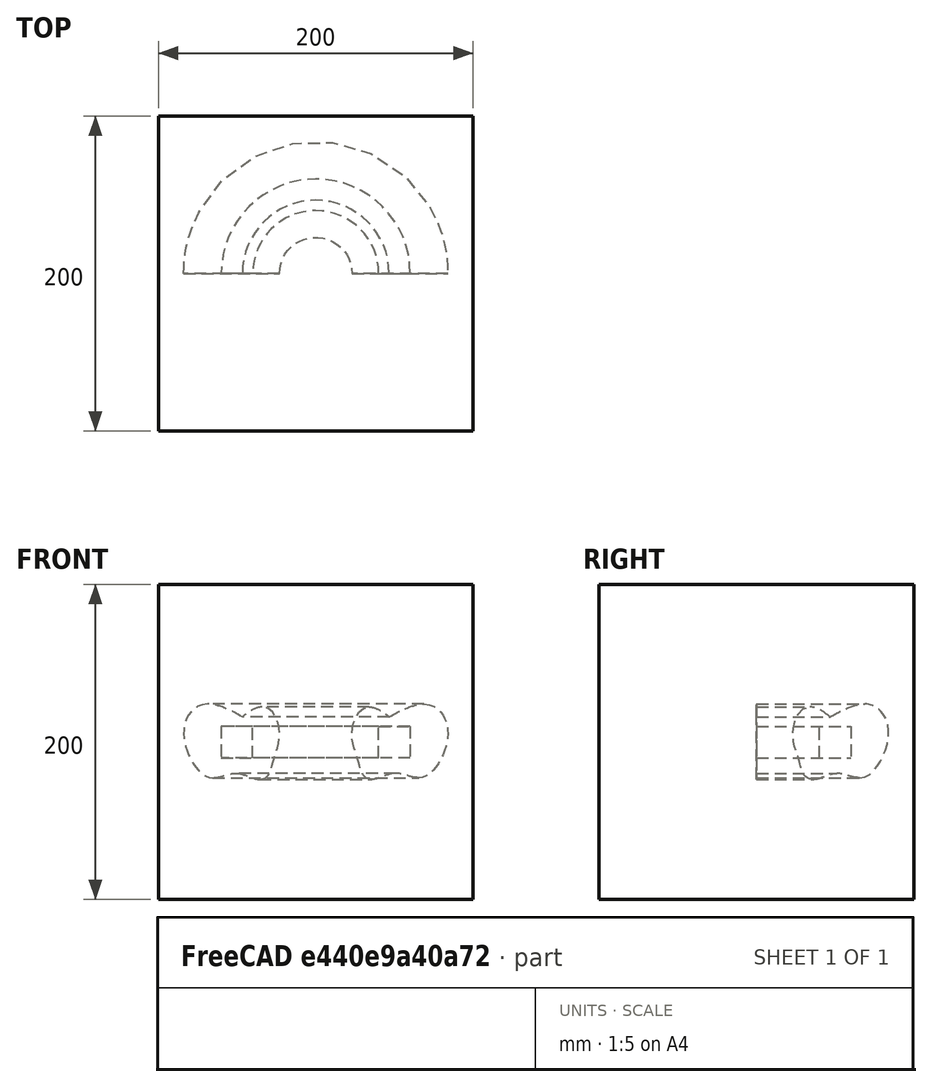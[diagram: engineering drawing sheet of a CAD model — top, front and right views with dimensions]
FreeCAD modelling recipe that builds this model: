
FCSTD DOCUMENT  (FreeCAD 0.19RUnknown)
Label: revolve
License: All rights reserved
LicenseURL: http://en.wikipedia.org/wiki/All_rights_reserved
objects: App::DocumentObjectGroupPython×1248, App::Part×2, Part::FeaturePython×1, Sketcher::SketchObject×1, Part::Revolution×1
note: 3 computed .brp shape members not serialized (recipe doc carries the construction recipe); baked Part::Feature solids carry a one-line shape summary decoded from their .brp

FEATURE [App::DocumentObjectGroupPython] HALFPI  # scripted group (container) (typed FeaturePython)
  name = HALFPI
  value = pi/2.
FEATURE [App::DocumentObjectGroupPython] PI  # scripted group (container) (typed FeaturePython)
  name = PI
  value = 1.*pi
FEATURE [App::DocumentObjectGroupPython] TWOPI  # scripted group (container) (typed FeaturePython)
  name = TWOPI
  value = 2.*pi
FEATURE [App::DocumentObjectGroupPython] Constants  # scripted group (container) (typed FeaturePython)
  Group = -> [HALFPI,PI,TWOPI]
FEATURE [App::DocumentObjectGroupPython] Variables  # scripted group (container) (typed FeaturePython)
FEATURE [App::DocumentObjectGroupPython] Quantities  # scripted group (container) (typed FeaturePython)
FEATURE [App::DocumentObjectGroupPython] Isotopes  # scripted group (container) (typed FeaturePython)
FEATURE [App::DocumentObjectGroupPython] Elements  # scripted group (container) (typed FeaturePython)
FEATURE [App::DocumentObjectGroupPython] G4Isotopes  # scripted group (container) (typed FeaturePython)
FEATURE [App::DocumentObjectGroupPython] H_element  # scripted group (container) (typed FeaturePython)
  Z = 1
  atom_value = 1.008
  formula = H
  name = H_element
FEATURE [App::DocumentObjectGroupPython] He_element  # scripted group (container) (typed FeaturePython)
  Z = 2
  atom_value = 4.0026
  formula = He
  name = He_element
FEATURE [App::DocumentObjectGroupPython] Li_element  # scripted group (container) (typed FeaturePython)
  Z = 3
  atom_value = 6.94
  formula = Li
  name = Li_element
FEATURE [App::DocumentObjectGroupPython] Be_element  # scripted group (container) (typed FeaturePython)
  Z = 4
  atom_value = 9.01218
  formula = Be
  name = Be_element
FEATURE [App::DocumentObjectGroupPython] B_element  # scripted group (container) (typed FeaturePython)
  Z = 5
  atom_value = 10.81
  formula = B
  name = B_element
FEATURE [App::DocumentObjectGroupPython] C_element  # scripted group (container) (typed FeaturePython)
  Z = 6
  atom_value = 12.011
  formula = C
  name = C_element
FEATURE [App::DocumentObjectGroupPython] N_element  # scripted group (container) (typed FeaturePython)
  Z = 7
  atom_value = 14.007
  formula = N
  name = N_element
FEATURE [App::DocumentObjectGroupPython] O_element  # scripted group (container) (typed FeaturePython)
  Z = 8
  atom_value = 15.999
  formula = O
  name = O_element
FEATURE [App::DocumentObjectGroupPython] F_element  # scripted group (container) (typed FeaturePython)
  Z = 9
  atom_value = 18.9984
  formula = F
  name = F_element
FEATURE [App::DocumentObjectGroupPython] Ne_element  # scripted group (container) (typed FeaturePython)
  Z = 10
  atom_value = 20.1797
  formula = Ne
  name = Ne_element
FEATURE [App::DocumentObjectGroupPython] Na_element  # scripted group (container) (typed FeaturePython)
  Z = 11
  atom_value = 22.9898
  formula = Na
  name = Na_element
FEATURE [App::DocumentObjectGroupPython] Mg_element  # scripted group (container) (typed FeaturePython)
  Z = 12
  atom_value = 24.305
  formula = Mg
  name = Mg_element
FEATURE [App::DocumentObjectGroupPython] Al_element  # scripted group (container) (typed FeaturePython)
  Z = 13
  atom_value = 26.9815
  formula = Al
  name = Al_element
FEATURE [App::DocumentObjectGroupPython] Si_element  # scripted group (container) (typed FeaturePython)
  Z = 14
  atom_value = 28.085
  formula = Si
  name = Si_element
FEATURE [App::DocumentObjectGroupPython] P_element  # scripted group (container) (typed FeaturePython)
  Z = 15
  atom_value = 30.9738
  formula = P
  name = P_element
FEATURE [App::DocumentObjectGroupPython] S_element  # scripted group (container) (typed FeaturePython)
  Z = 16
  atom_value = 32.06
  formula = S
  name = S_element
FEATURE [App::DocumentObjectGroupPython] Cl_element  # scripted group (container) (typed FeaturePython)
  Z = 17
  atom_value = 35.45
  formula = Cl
  name = Cl_element
FEATURE [App::DocumentObjectGroupPython] Ar_element  # scripted group (container) (typed FeaturePython)
  Z = 18
  atom_value = 39.95
  formula = Ar
  name = Ar_element
FEATURE [App::DocumentObjectGroupPython] K_element  # scripted group (container) (typed FeaturePython)
  Z = 19
  atom_value = 39.0983
  formula = K
  name = K_element
FEATURE [App::DocumentObjectGroupPython] Ca_element  # scripted group (container) (typed FeaturePython)
  Z = 20
  atom_value = 40.078
  formula = Ca
  name = Ca_element
FEATURE [App::DocumentObjectGroupPython] Sc_element  # scripted group (container) (typed FeaturePython)
  Z = 21
  atom_value = 44.9559
  formula = Sc
  name = Sc_element
FEATURE [App::DocumentObjectGroupPython] Ti_element  # scripted group (container) (typed FeaturePython)
  Z = 22
  atom_value = 47.867
  formula = Ti
  name = Ti_element
FEATURE [App::DocumentObjectGroupPython] V_element  # scripted group (container) (typed FeaturePython)
  Z = 23
  atom_value = 50.9415
  formula = V
  name = V_element
FEATURE [App::DocumentObjectGroupPython] Cr_element  # scripted group (container) (typed FeaturePython)
  Z = 24
  atom_value = 51.9961
  formula = Cr
  name = Cr_element
FEATURE [App::DocumentObjectGroupPython] Mn_element  # scripted group (container) (typed FeaturePython)
  Z = 25
  atom_value = 54.938
  formula = Mn
  name = Mn_element
FEATURE [App::DocumentObjectGroupPython] Fe_element  # scripted group (container) (typed FeaturePython)
  Z = 26
  atom_value = 55.845
  formula = Fe
  name = Fe_element
FEATURE [App::DocumentObjectGroupPython] Co_element  # scripted group (container) (typed FeaturePython)
  Z = 27
  atom_value = 58.9332
  formula = Co
  name = Co_element
FEATURE [App::DocumentObjectGroupPython] Ni_element  # scripted group (container) (typed FeaturePython)
  Z = 28
  atom_value = 58.6934
  formula = Ni
  name = Ni_element
FEATURE [App::DocumentObjectGroupPython] Cu_element  # scripted group (container) (typed FeaturePython)
  Z = 29
  atom_value = 63.546
  formula = Cu
  name = Cu_element
FEATURE [App::DocumentObjectGroupPython] Zn_element  # scripted group (container) (typed FeaturePython)
  Z = 30
  atom_value = 65.38
  formula = Zn
  name = Zn_element
FEATURE [App::DocumentObjectGroupPython] Ga_element  # scripted group (container) (typed FeaturePython)
  Z = 31
  atom_value = 69.723
  formula = Ga
  name = Ga_element
FEATURE [App::DocumentObjectGroupPython] Ge_element  # scripted group (container) (typed FeaturePython)
  Z = 32
  atom_value = 72.63
  formula = Ge
  name = Ge_element
FEATURE [App::DocumentObjectGroupPython] As_element  # scripted group (container) (typed FeaturePython)
  Z = 33
  atom_value = 74.9216
  formula = As
  name = As_element
FEATURE [App::DocumentObjectGroupPython] Se_element  # scripted group (container) (typed FeaturePython)
  Z = 34
  atom_value = 78.971
  formula = Se
  name = Se_element
FEATURE [App::DocumentObjectGroupPython] Br_element  # scripted group (container) (typed FeaturePython)
  Z = 35
  atom_value = 79.904
  formula = Br
  name = Br_element
FEATURE [App::DocumentObjectGroupPython] Kr_element  # scripted group (container) (typed FeaturePython)
  Z = 36
  atom_value = 83.798
  formula = Kr
  name = Kr_element
FEATURE [App::DocumentObjectGroupPython] Rb_element  # scripted group (container) (typed FeaturePython)
  Z = 37
  atom_value = 85.4678
  formula = Rb
  name = Rb_element
FEATURE [App::DocumentObjectGroupPython] Sr_element  # scripted group (container) (typed FeaturePython)
  Z = 38
  atom_value = 87.62
  formula = Sr
  name = Sr_element
FEATURE [App::DocumentObjectGroupPython] Y_element  # scripted group (container) (typed FeaturePython)
  Z = 39
  atom_value = 88.9058
  formula = Y
  name = Y_element
FEATURE [App::DocumentObjectGroupPython] Zr_element  # scripted group (container) (typed FeaturePython)
  Z = 40
  atom_value = 91.224
  formula = Zr
  name = Zr_element
FEATURE [App::DocumentObjectGroupPython] Nb_element  # scripted group (container) (typed FeaturePython)
  Z = 41
  atom_value = 92.9064
  formula = Nb
  name = Nb_element
FEATURE [App::DocumentObjectGroupPython] Mo_element  # scripted group (container) (typed FeaturePython)
  Z = 42
  atom_value = 95.95
  formula = Mo
  name = Mo_element
FEATURE [App::DocumentObjectGroupPython] Tc_element  # scripted group (container) (typed FeaturePython)
  Z = 43
  atom_value = 97
  formula = Tc
  name = Tc_element
FEATURE [App::DocumentObjectGroupPython] Ru_element  # scripted group (container) (typed FeaturePython)
  Z = 44
  atom_value = 101.07
  formula = Ru
  name = Ru_element
FEATURE [App::DocumentObjectGroupPython] Rh_element  # scripted group (container) (typed FeaturePython)
  Z = 45
  atom_value = 102.905
  formula = Rh
  name = Rh_element
FEATURE [App::DocumentObjectGroupPython] Pd_element  # scripted group (container) (typed FeaturePython)
  Z = 46
  atom_value = 106.42
  formula = Pd
  name = Pd_element
FEATURE [App::DocumentObjectGroupPython] Ag_element  # scripted group (container) (typed FeaturePython)
  Z = 47
  atom_value = 107.868
  formula = Ag
  name = Ag_element
FEATURE [App::DocumentObjectGroupPython] Cd_element  # scripted group (container) (typed FeaturePython)
  Z = 48
  atom_value = 112.414
  formula = Cd
  name = Cd_element
FEATURE [App::DocumentObjectGroupPython] In_element  # scripted group (container) (typed FeaturePython)
  Z = 49
  atom_value = 114.818
  formula = In
  name = In_element
FEATURE [App::DocumentObjectGroupPython] Sn_element  # scripted group (container) (typed FeaturePython)
  Z = 50
  atom_value = 118.71
  formula = Sn
  name = Sn_element
FEATURE [App::DocumentObjectGroupPython] Sb_element  # scripted group (container) (typed FeaturePython)
  Z = 51
  atom_value = 121.76
  formula = Sb
  name = Sb_element
FEATURE [App::DocumentObjectGroupPython] Te_element  # scripted group (container) (typed FeaturePython)
  Z = 52
  atom_value = 127.6
  formula = Te
  name = Te_element
FEATURE [App::DocumentObjectGroupPython] I_element  # scripted group (container) (typed FeaturePython)
  Z = 53
  atom_value = 126.904
  formula = I
  name = I_element
FEATURE [App::DocumentObjectGroupPython] Xe_element  # scripted group (container) (typed FeaturePython)
  Z = 54
  atom_value = 131.293
  formula = Xe
  name = Xe_element
FEATURE [App::DocumentObjectGroupPython] Cs_element  # scripted group (container) (typed FeaturePython)
  Z = 55
  atom_value = 132.905
  formula = Cs
  name = Cs_element
FEATURE [App::DocumentObjectGroupPython] Ba_element  # scripted group (container) (typed FeaturePython)
  Z = 56
  atom_value = 137.327
  formula = Ba
  name = Ba_element
FEATURE [App::DocumentObjectGroupPython] La_element  # scripted group (container) (typed FeaturePython)
  Z = 57
  atom_value = 138.905
  formula = La
  name = La_element
FEATURE [App::DocumentObjectGroupPython] Ce_element  # scripted group (container) (typed FeaturePython)
  Z = 58
  atom_value = 140.116
  formula = Ce
  name = Ce_element
FEATURE [App::DocumentObjectGroupPython] Pr_element  # scripted group (container) (typed FeaturePython)
  Z = 59
  atom_value = 140.908
  formula = Pr
  name = Pr_element
FEATURE [App::DocumentObjectGroupPython] Nd_element  # scripted group (container) (typed FeaturePython)
  Z = 60
  atom_value = 144.242
  formula = Nd
  name = Nd_element
FEATURE [App::DocumentObjectGroupPython] Pm_element  # scripted group (container) (typed FeaturePython)
  Z = 61
  atom_value = 145
  formula = Pm
  name = Pm_element
FEATURE [App::DocumentObjectGroupPython] Sm_element  # scripted group (container) (typed FeaturePython)
  Z = 62
  atom_value = 150.36
  formula = Sm
  name = Sm_element
FEATURE [App::DocumentObjectGroupPython] Eu_element  # scripted group (container) (typed FeaturePython)
  Z = 63
  atom_value = 151.964
  formula = Eu
  name = Eu_element
FEATURE [App::DocumentObjectGroupPython] Gd_element  # scripted group (container) (typed FeaturePython)
  Z = 64
  atom_value = 157.25
  formula = Gd
  name = Gd_element
FEATURE [App::DocumentObjectGroupPython] Tb_element  # scripted group (container) (typed FeaturePython)
  Z = 65
  atom_value = 158.925
  formula = Tb
  name = Tb_element
FEATURE [App::DocumentObjectGroupPython] Dy_element  # scripted group (container) (typed FeaturePython)
  Z = 66
  atom_value = 162.5
  formula = Dy
  name = Dy_element
FEATURE [App::DocumentObjectGroupPython] Ho_element  # scripted group (container) (typed FeaturePython)
  Z = 67
  atom_value = 164.93
  formula = Ho
  name = Ho_element
FEATURE [App::DocumentObjectGroupPython] Er_element  # scripted group (container) (typed FeaturePython)
  Z = 68
  atom_value = 167.259
  formula = Er
  name = Er_element
FEATURE [App::DocumentObjectGroupPython] Tm_element  # scripted group (container) (typed FeaturePython)
  Z = 69
  atom_value = 168.934
  formula = Tm
  name = Tm_element
FEATURE [App::DocumentObjectGroupPython] Yb_element  # scripted group (container) (typed FeaturePython)
  Z = 70
  atom_value = 173.045
  formula = Yb
  name = Yb_element
FEATURE [App::DocumentObjectGroupPython] Lu_element  # scripted group (container) (typed FeaturePython)
  Z = 71
  atom_value = 174.967
  formula = Lu
  name = Lu_element
FEATURE [App::DocumentObjectGroupPython] Hf_element  # scripted group (container) (typed FeaturePython)
  Z = 72
  atom_value = 178.49
  formula = Hf
  name = Hf_element
FEATURE [App::DocumentObjectGroupPython] Ta_element  # scripted group (container) (typed FeaturePython)
  Z = 73
  atom_value = 180.948
  formula = Ta
  name = Ta_element
FEATURE [App::DocumentObjectGroupPython] W_element  # scripted group (container) (typed FeaturePython)
  Z = 74
  atom_value = 183.84
  formula = W
  name = W_element
FEATURE [App::DocumentObjectGroupPython] Re_element  # scripted group (container) (typed FeaturePython)
  Z = 75
  atom_value = 186.207
  formula = Re
  name = Re_element
FEATURE [App::DocumentObjectGroupPython] Os_element  # scripted group (container) (typed FeaturePython)
  Z = 76
  atom_value = 190.23
  formula = Os
  name = Os_element
FEATURE [App::DocumentObjectGroupPython] Ir_element  # scripted group (container) (typed FeaturePython)
  Z = 77
  atom_value = 192.217
  formula = Ir
  name = Ir_element
FEATURE [App::DocumentObjectGroupPython] Pt_element  # scripted group (container) (typed FeaturePython)
  Z = 78
  atom_value = 195.084
  formula = Pt
  name = Pt_element
FEATURE [App::DocumentObjectGroupPython] Au_element  # scripted group (container) (typed FeaturePython)
  Z = 79
  atom_value = 196.967
  formula = Au
  name = Au_element
FEATURE [App::DocumentObjectGroupPython] Hg_element  # scripted group (container) (typed FeaturePython)
  Z = 80
  atom_value = 200.592
  formula = Hg
  name = Hg_element
FEATURE [App::DocumentObjectGroupPython] Tl_element  # scripted group (container) (typed FeaturePython)
  Z = 81
  atom_value = 204.38
  formula = Tl
  name = Tl_element
FEATURE [App::DocumentObjectGroupPython] Pb_element  # scripted group (container) (typed FeaturePython)
  Z = 82
  atom_value = 207.2
  formula = Pb
  name = Pb_element
FEATURE [App::DocumentObjectGroupPython] Bi_element  # scripted group (container) (typed FeaturePython)
  Z = 83
  atom_value = 208.98
  formula = Bi
  name = Bi_element
FEATURE [App::DocumentObjectGroupPython] Po_element  # scripted group (container) (typed FeaturePython)
  Z = 84
  atom_value = 209
  formula = Po
  name = Po_element
FEATURE [App::DocumentObjectGroupPython] At_element  # scripted group (container) (typed FeaturePython)
  Z = 85
  atom_value = 210
  formula = At
  name = At_element
FEATURE [App::DocumentObjectGroupPython] Rn_element  # scripted group (container) (typed FeaturePython)
  Z = 86
  atom_value = 222
  formula = Rn
  name = Rn_element
FEATURE [App::DocumentObjectGroupPython] Fr_element  # scripted group (container) (typed FeaturePython)
  Z = 87
  atom_value = 223
  formula = Fr
  name = Fr_element
FEATURE [App::DocumentObjectGroupPython] Ra_element  # scripted group (container) (typed FeaturePython)
  Z = 88
  atom_value = 226
  formula = Ra
  name = Ra_element
FEATURE [App::DocumentObjectGroupPython] Ac_element  # scripted group (container) (typed FeaturePython)
  Z = 89
  atom_value = 227
  formula = Ac
  name = Ac_element
FEATURE [App::DocumentObjectGroupPython] Th_element  # scripted group (container) (typed FeaturePython)
  Z = 90
  atom_value = 232.038
  formula = Th
  name = Th_element
FEATURE [App::DocumentObjectGroupPython] Pa_element  # scripted group (container) (typed FeaturePython)
  Z = 91
  atom_value = 231.036
  formula = Pa
  name = Pa_element
FEATURE [App::DocumentObjectGroupPython] U_element  # scripted group (container) (typed FeaturePython)
  Z = 92
  atom_value = 238.029
  formula = U
  name = U_element
FEATURE [App::DocumentObjectGroupPython] Np_element  # scripted group (container) (typed FeaturePython)
  Z = 93
  atom_value = 237
  formula = Np
  name = Np_element
FEATURE [App::DocumentObjectGroupPython] Pu_element  # scripted group (container) (typed FeaturePython)
  Z = 94
  atom_value = 244
  formula = Pu
  name = Pu_element
FEATURE [App::DocumentObjectGroupPython] Am_element  # scripted group (container) (typed FeaturePython)
  Z = 95
  atom_value = 243
  formula = Am
  name = Am_element
FEATURE [App::DocumentObjectGroupPython] Cm_element  # scripted group (container) (typed FeaturePython)
  Z = 96
  atom_value = 247
  formula = Cm
  name = Cm_element
FEATURE [App::DocumentObjectGroupPython] Bk_element  # scripted group (container) (typed FeaturePython)
  Z = 97
  atom_value = 247
  formula = Bk
  name = Bk_element
FEATURE [App::DocumentObjectGroupPython] Cf_element  # scripted group (container) (typed FeaturePython)
  Z = 98
  atom_value = 251
  formula = Cf
  name = Cf_element
FEATURE [App::DocumentObjectGroupPython] G4Elements  # scripted group (container) (typed FeaturePython)
  Group = -> [H_element,He_element,Li_element,Be_element,B_element,C_element,N_element,O_element,F_element,Ne_element,Na_element,Mg_element,Al_element,Si_element,P_element,S_element,Cl_element,Ar_element,K_element,Ca_element,Sc_element,Ti_element,V_element,Cr_element,Mn_element,Fe_element,Co_element,Ni_element,Cu_element,Zn_element,Ga_element,Ge_element,As_element,Se_element,Br_element,Kr_element,Rb_element,+61 more]
FEATURE [App::DocumentObjectGroupPython] H_element001  label="H_element : 0.101"  # scripted group (container) (typed FeaturePython)
  n = 0.101327
FEATURE [App::DocumentObjectGroupPython] C_element001  label="C_element : 0.775"  # scripted group (container) (typed FeaturePython)
  n = 0.7755
FEATURE [App::DocumentObjectGroupPython] N_element001  label="N_element : 0.035"  # scripted group (container) (typed FeaturePython)
  n = 0.035057
FEATURE [App::DocumentObjectGroupPython] O_element001  label="O_element : 0.052"  # scripted group (container) (typed FeaturePython)
  n = 0.0523159
FEATURE [App::DocumentObjectGroupPython] F_element001  label="F_element : 0.017"  # scripted group (container) (typed FeaturePython)
  n = 0.017422
FEATURE [App::DocumentObjectGroupPython] Ca_element001  label="Ca_element : 0.018"  # scripted group (container) (typed FeaturePython)
  n = 0.018378
FEATURE [App::DocumentObjectGroupPython] G4_A_150_TISSUE  label="G4_A-150_TISSUE"  # scripted group (container) (typed FeaturePython)
  Dunit = g/cm3
  Dvalue = 1.127
  Group = -> [H_element001,C_element001,N_element001,O_element001,F_element001,Ca_element001]
  conduct = 2
  density = 1
  expand = 3
  formula = G4_A-150_TISSUE
  name = G4_A-150_TISSUE
  specific = 4
FEATURE [App::DocumentObjectGroupPython] C_element002  label="C_element : 3"  # scripted group (container) (typed FeaturePython)
  n = 3
  ref = C_element
FEATURE [App::DocumentObjectGroupPython] H_element002  label="H_element : 6"  # scripted group (container) (typed FeaturePython)
  n = 6
  ref = H_element
FEATURE [App::DocumentObjectGroupPython] O_element002  label="O_element : 1"  # scripted group (container) (typed FeaturePython)
  n = 1
  ref = O_element
FEATURE [App::DocumentObjectGroupPython] G4_ACETONE  # scripted group (container) (typed FeaturePython)
  Dunit = g/cm3
  Dvalue = 0.7899
  Group = -> [C_element002,H_element002,O_element002]
  conduct = 2
  density = 1
  expand = 3
  formula = G4_ACETONE
  name = G4_ACETONE
  specific = 4
FEATURE [App::DocumentObjectGroupPython] C_element003  label="C_element : 2"  # scripted group (container) (typed FeaturePython)
  n = 2
  ref = C_element
FEATURE [App::DocumentObjectGroupPython] H_element003  label="H_element : 2"  # scripted group (container) (typed FeaturePython)
  n = 2
  ref = H_element
FEATURE [App::DocumentObjectGroupPython] G4_ACETYLENE  # scripted group (container) (typed FeaturePython)
  Dunit = g/cm3
  Dvalue = 0.0010967
  Group = -> [C_element003,H_element003]
  conduct = 2
  density = 1
  expand = 3
  formula = G4_ACETYLENE
  name = G4_ACETYLENE
  specific = 4
FEATURE [App::DocumentObjectGroupPython] C_element004  label="C_element : 5"  # scripted group (container) (typed FeaturePython)
  n = 5
  ref = C_element
FEATURE [App::DocumentObjectGroupPython] H_element004  label="H_element : 5"  # scripted group (container) (typed FeaturePython)
  n = 5
  ref = H_element
FEATURE [App::DocumentObjectGroupPython] N_element002  label="N_element : 5"  # scripted group (container) (typed FeaturePython)
  n = 5
  ref = N_element
FEATURE [App::DocumentObjectGroupPython] G4_ADENINE  # scripted group (container) (typed FeaturePython)
  Dunit = g/cm3
  Dvalue = 1.6
  Group = -> [C_element004,H_element004,N_element002]
  conduct = 2
  density = 1
  expand = 3
  formula = G4_ADENINE
  name = G4_ADENINE
  specific = 4
FEATURE [App::DocumentObjectGroupPython] H_element005  label="H_element : 0.114"  # scripted group (container) (typed FeaturePython)
  n = 0.114
FEATURE [App::DocumentObjectGroupPython] C_element005  label="C_element : 0.598"  # scripted group (container) (typed FeaturePython)
  n = 0.598
FEATURE [App::DocumentObjectGroupPython] N_element003  label="N_element : 0.007"  # scripted group (container) (typed FeaturePython)
  n = 0.007
FEATURE [App::DocumentObjectGroupPython] O_element003  label="O_element : 0.278"  # scripted group (container) (typed FeaturePython)
  n = 0.278
FEATURE [App::DocumentObjectGroupPython] Na_element001  label="Na_element : 0.001"  # scripted group (container) (typed FeaturePython)
  n = 0.001
FEATURE [App::DocumentObjectGroupPython] S_element001  label="S_element : 0.001"  # scripted group (container) (typed FeaturePython)
  n = 0.001
FEATURE [App::DocumentObjectGroupPython] Cl_element001  label="Cl_element : 0.001"  # scripted group (container) (typed FeaturePython)
  n = 0.001
FEATURE [App::DocumentObjectGroupPython] G4_ADIPOSE_TISSUE_ICRP  # scripted group (container) (typed FeaturePython)
  Dunit = g/cm3
  Dvalue = 0.95
  Group = -> [H_element005,C_element005,N_element003,O_element003,Na_element001,S_element001,Cl_element001]
  conduct = 2
  density = 1
  expand = 3
  formula = G4_ADIPOSE_TISSUE_ICRP
  name = G4_ADIPOSE_TISSUE_ICRP
  specific = 4
FEATURE [App::DocumentObjectGroupPython] C_element006  label="C_element : 0.000"  # scripted group (container) (typed FeaturePython)
  n = 0.000124
FEATURE [App::DocumentObjectGroupPython] N_element004  label="N_element : 0.755"  # scripted group (container) (typed FeaturePython)
  n = 0.755268
FEATURE [App::DocumentObjectGroupPython] O_element004  label="O_element : 0.232"  # scripted group (container) (typed FeaturePython)
  n = 0.231781
FEATURE [App::DocumentObjectGroupPython] Ar_element001  label="Ar_element : 0.013"  # scripted group (container) (typed FeaturePython)
  n = 0.012827
FEATURE [App::DocumentObjectGroupPython] G4_AIR  # scripted group (container) (typed FeaturePython)
  Dunit = g/cm3
  Dvalue = 0.00120479
  Group = -> [C_element006,N_element004,O_element004,Ar_element001]
  conduct = 2
  density = 1
  expand = 3
  formula = G4_AIR
  name = G4_AIR
  specific = 4
FEATURE [App::DocumentObjectGroupPython] C_element007  label="C_element : 006"  # scripted group (container) (typed FeaturePython)
  n = 3
  ref = C_element
FEATURE [App::DocumentObjectGroupPython] H_element006  label="H_element : 7"  # scripted group (container) (typed FeaturePython)
  n = 7
  ref = H_element
FEATURE [App::DocumentObjectGroupPython] N_element005  label="N_element : 1"  # scripted group (container) (typed FeaturePython)
  n = 1
  ref = N_element
FEATURE [App::DocumentObjectGroupPython] O_element005  label="O_element : 2"  # scripted group (container) (typed FeaturePython)
  n = 2
  ref = O_element
FEATURE [App::DocumentObjectGroupPython] G4_ALANINE  # scripted group (container) (typed FeaturePython)
  Dunit = g/cm3
  Dvalue = 1.42
  Group = -> [C_element007,H_element006,N_element005,O_element005]
  conduct = 2
  density = 1
  expand = 3
  formula = G4_ALANINE
  name = G4_ALANINE
  specific = 4
FEATURE [App::DocumentObjectGroupPython] Al_element001  label="Al_element : 2"  # scripted group (container) (typed FeaturePython)
  n = 2
  ref = Al_element
FEATURE [App::DocumentObjectGroupPython] O_element006  label="O_element : 3"  # scripted group (container) (typed FeaturePython)
  n = 3
  ref = O_element
FEATURE [App::DocumentObjectGroupPython] G4_ALUMINUM_OXIDE  # scripted group (container) (typed FeaturePython)
  Dunit = g/cm3
  Dvalue = 3.97
  Group = -> [Al_element001,O_element006]
  conduct = 2
  density = 1
  expand = 3
  formula = G4_ALUMINUM_OXIDE
  name = G4_ALUMINUM_OXIDE
  specific = 4
FEATURE [App::DocumentObjectGroupPython] H_element007  label="H_element : 0.106"  # scripted group (container) (typed FeaturePython)
  n = 0.10593
FEATURE [App::DocumentObjectGroupPython] C_element008  label="C_element : 0.789"  # scripted group (container) (typed FeaturePython)
  n = 0.788974
FEATURE [App::DocumentObjectGroupPython] O_element007  label="O_element : 0.105"  # scripted group (container) (typed FeaturePython)
  n = 0.105096
FEATURE [App::DocumentObjectGroupPython] G4_AMBER  # scripted group (container) (typed FeaturePython)
  Dunit = g/cm3
  Dvalue = 1.1
  Group = -> [H_element007,C_element008,O_element007]
  conduct = 2
  density = 1
  expand = 3
  formula = G4_AMBER
  name = G4_AMBER
  specific = 4
FEATURE [App::DocumentObjectGroupPython] N_element006  label="N_element : 006"  # scripted group (container) (typed FeaturePython)
  n = 1
  ref = N_element
FEATURE [App::DocumentObjectGroupPython] H_element008  label="H_element : 3"  # scripted group (container) (typed FeaturePython)
  n = 3
  ref = H_element
FEATURE [App::DocumentObjectGroupPython] G4_AMMONIA  # scripted group (container) (typed FeaturePython)
  Dunit = g/cm3
  Dvalue = 0.000826019
  Group = -> [N_element006,H_element008]
  conduct = 2
  density = 1
  expand = 3
  formula = G4_AMMONIA
  name = G4_AMMONIA
  specific = 4
FEATURE [App::DocumentObjectGroupPython] C_element009  label="C_element : 6"  # scripted group (container) (typed FeaturePython)
  n = 6
  ref = C_element
FEATURE [App::DocumentObjectGroupPython] H_element009  label="H_element : 008"  # scripted group (container) (typed FeaturePython)
  n = 7
  ref = H_element
FEATURE [App::DocumentObjectGroupPython] N_element007  label="N_element : 007"  # scripted group (container) (typed FeaturePython)
  n = 1
  ref = N_element
FEATURE [App::DocumentObjectGroupPython] G4_ANILINE  # scripted group (container) (typed FeaturePython)
  Dunit = g/cm3
  Dvalue = 1.0235
  Group = -> [C_element009,H_element009,N_element007]
  conduct = 2
  density = 1
  expand = 3
  formula = G4_ANILINE
  name = G4_ANILINE
  specific = 4
FEATURE [App::DocumentObjectGroupPython] C_element010  label="C_element : 14"  # scripted group (container) (typed FeaturePython)
  n = 14
  ref = C_element
FEATURE [App::DocumentObjectGroupPython] H_element010  label="H_element : 10"  # scripted group (container) (typed FeaturePython)
  n = 10
  ref = H_element
FEATURE [App::DocumentObjectGroupPython] G4_ANTHRACENE  # scripted group (container) (typed FeaturePython)
  Dunit = g/cm3
  Dvalue = 1.283
  Group = -> [C_element010,H_element010]
  conduct = 2
  density = 1
  expand = 3
  formula = G4_ANTHRACENE
  name = G4_ANTHRACENE
  specific = 4
FEATURE [App::DocumentObjectGroupPython] H_element011  label="H_element : 0.065"  # scripted group (container) (typed FeaturePython)
  n = 0.0654709
FEATURE [App::DocumentObjectGroupPython] C_element011  label="C_element : 0.537"  # scripted group (container) (typed FeaturePython)
  n = 0.536944
FEATURE [App::DocumentObjectGroupPython] N_element008  label="N_element : 0.021"  # scripted group (container) (typed FeaturePython)
  n = 0.0215
FEATURE [App::DocumentObjectGroupPython] O_element008  label="O_element : 0.032"  # scripted group (container) (typed FeaturePython)
  n = 0.032085
FEATURE [App::DocumentObjectGroupPython] F_element002  label="F_element : 0.167"  # scripted group (container) (typed FeaturePython)
  n = 0.167411
FEATURE [App::DocumentObjectGroupPython] Ca_element002  label="Ca_element : 0.177"  # scripted group (container) (typed FeaturePython)
  n = 0.176589
FEATURE [App::DocumentObjectGroupPython] G4_B_100_BONE  label="G4_B-100_BONE"  # scripted group (container) (typed FeaturePython)
  Dunit = g/cm3
  Dvalue = 1.45
  Group = -> [H_element011,C_element011,N_element008,O_element008,F_element002,Ca_element002]
  conduct = 2
  density = 1
  expand = 3
  formula = G4_B-100_BONE
  name = G4_B-100_BONE
  specific = 4
FEATURE [App::DocumentObjectGroupPython] H_element012  label="H_element : 0.057"  # scripted group (container) (typed FeaturePython)
  n = 0.057441
FEATURE [App::DocumentObjectGroupPython] C_element012  label="C_element : 0.790"  # scripted group (container) (typed FeaturePython)
  n = 0.774591
FEATURE [App::DocumentObjectGroupPython] O_element009  label="O_element : 0.168"  # scripted group (container) (typed FeaturePython)
  n = 0.167968
FEATURE [App::DocumentObjectGroupPython] G4_BAKELITE  # scripted group (container) (typed FeaturePython)
  Dunit = g/cm3
  Dvalue = 1.25
  Group = -> [H_element012,C_element012,O_element009]
  conduct = 2
  density = 1
  expand = 3
  formula = G4_BAKELITE
  name = G4_BAKELITE
  specific = 4
FEATURE [App::DocumentObjectGroupPython] Ba_element001  label="Ba_element : 1"  # scripted group (container) (typed FeaturePython)
  n = 1
  ref = Ba_element
FEATURE [App::DocumentObjectGroupPython] F_element003  label="F_element : 2"  # scripted group (container) (typed FeaturePython)
  n = 2
  ref = F_element
FEATURE [App::DocumentObjectGroupPython] G4_BARIUM_FLUORIDE  # scripted group (container) (typed FeaturePython)
  Dunit = g/cm3
  Dvalue = 4.89
  Group = -> [Ba_element001,F_element003]
  conduct = 2
  density = 1
  expand = 3
  formula = G4_BARIUM_FLUORIDE
  name = G4_BARIUM_FLUORIDE
  specific = 4
FEATURE [App::DocumentObjectGroupPython] Ba_element002  label="Ba_element : 002"  # scripted group (container) (typed FeaturePython)
  n = 1
  ref = Ba_element
FEATURE [App::DocumentObjectGroupPython] S_element002  label="S_element : 1"  # scripted group (container) (typed FeaturePython)
  n = 1
  ref = S_element
FEATURE [App::DocumentObjectGroupPython] O_element010  label="O_element : 4"  # scripted group (container) (typed FeaturePython)
  n = 4
  ref = O_element
FEATURE [App::DocumentObjectGroupPython] G4_BARIUM_SULFATE  # scripted group (container) (typed FeaturePython)
  Dunit = g/cm3
  Dvalue = 4.5
  Group = -> [Ba_element002,S_element002,O_element010]
  conduct = 2
  density = 1
  expand = 3
  formula = G4_BARIUM_SULFATE
  name = G4_BARIUM_SULFATE
  specific = 4
FEATURE [App::DocumentObjectGroupPython] C_element013  label="C_element : 007"  # scripted group (container) (typed FeaturePython)
  n = 6
  ref = C_element
FEATURE [App::DocumentObjectGroupPython] H_element013  label="H_element : 009"  # scripted group (container) (typed FeaturePython)
  n = 6
  ref = H_element
FEATURE [App::DocumentObjectGroupPython] G4_BENZENE  # scripted group (container) (typed FeaturePython)
  Dunit = g/cm3
  Dvalue = 0.87865
  Group = -> [C_element013,H_element013]
  conduct = 2
  density = 1
  expand = 3
  formula = G4_BENZENE
  name = G4_BENZENE
  specific = 4
FEATURE [App::DocumentObjectGroupPython] Be_element001  label="Be_element : 1"  # scripted group (container) (typed FeaturePython)
  n = 1
  ref = Be_element
FEATURE [App::DocumentObjectGroupPython] O_element011  label="O_element : 005"  # scripted group (container) (typed FeaturePython)
  n = 1
  ref = O_element
FEATURE [App::DocumentObjectGroupPython] G4_BERYLLIUM_OXIDE  # scripted group (container) (typed FeaturePython)
  Dunit = g/cm3
  Dvalue = 3.01
  Group = -> [Be_element001,O_element011]
  conduct = 2
  density = 1
  expand = 3
  formula = G4_BERYLLIUM_OXIDE
  name = G4_BERYLLIUM_OXIDE
  specific = 4
FEATURE [App::DocumentObjectGroupPython] Bi_element001  label="Bi_element : 4"  # scripted group (container) (typed FeaturePython)
  n = 4
  ref = Bi_element
FEATURE [App::DocumentObjectGroupPython] Ge_element001  label="Ge_element : 3"  # scripted group (container) (typed FeaturePython)
  n = 3
  ref = Ge_element
FEATURE [App::DocumentObjectGroupPython] O_element012  label="O_element : 12"  # scripted group (container) (typed FeaturePython)
  n = 12
  ref = O_element
FEATURE [App::DocumentObjectGroupPython] G4_BGO  # scripted group (container) (typed FeaturePython)
  Dunit = g/cm3
  Dvalue = 7.13
  Group = -> [Bi_element001,Ge_element001,O_element012]
  conduct = 2
  density = 1
  expand = 3
  formula = G4_BGO
  name = G4_BGO
  specific = 4
FEATURE [App::DocumentObjectGroupPython] H_element014  label="H_element : 0.102"  # scripted group (container) (typed FeaturePython)
  n = 0.102
FEATURE [App::DocumentObjectGroupPython] C_element014  label="C_element : 0.110"  # scripted group (container) (typed FeaturePython)
  n = 0.11
FEATURE [App::DocumentObjectGroupPython] N_element009  label="N_element : 0.033"  # scripted group (container) (typed FeaturePython)
  n = 0.033
FEATURE [App::DocumentObjectGroupPython] O_element013  label="O_element : 0.745"  # scripted group (container) (typed FeaturePython)
  n = 0.745
FEATURE [App::DocumentObjectGroupPython] Na_element002  label="Na_element : 0.002"  # scripted group (container) (typed FeaturePython)
  n = 0.001
FEATURE [App::DocumentObjectGroupPython] P_element001  label="P_element : 0.001"  # scripted group (container) (typed FeaturePython)
  n = 0.001
FEATURE [App::DocumentObjectGroupPython] S_element003  label="S_element : 0.002"  # scripted group (container) (typed FeaturePython)
  n = 0.002
FEATURE [App::DocumentObjectGroupPython] Cl_element002  label="Cl_element : 0.003"  # scripted group (container) (typed FeaturePython)
  n = 0.003
FEATURE [App::DocumentObjectGroupPython] K_element001  label="K_element : 0.002"  # scripted group (container) (typed FeaturePython)
  n = 0.002
FEATURE [App::DocumentObjectGroupPython] Fe_element001  label="Fe_element : 0.001"  # scripted group (container) (typed FeaturePython)
  n = 0.001
FEATURE [App::DocumentObjectGroupPython] G4_BLOOD_ICRP  # scripted group (container) (typed FeaturePython)
  Dunit = g/cm3
  Dvalue = 1.06
  Group = -> [H_element014,C_element014,N_element009,O_element013,Na_element002,P_element001,S_element003,Cl_element002,K_element001,Fe_element001]
  conduct = 2
  density = 1
  expand = 3
  formula = G4_BLOOD_ICRP
  name = G4_BLOOD_ICRP
  specific = 4
FEATURE [App::DocumentObjectGroupPython] H_element015  label="H_element : 0.064"  # scripted group (container) (typed FeaturePython)
  n = 0.064
FEATURE [App::DocumentObjectGroupPython] C_element015  label="C_element : 0.278"  # scripted group (container) (typed FeaturePython)
  n = 0.278
FEATURE [App::DocumentObjectGroupPython] N_element010  label="N_element : 0.027"  # scripted group (container) (typed FeaturePython)
  n = 0.027
FEATURE [App::DocumentObjectGroupPython] O_element014  label="O_element : 0.410"  # scripted group (container) (typed FeaturePython)
  n = 0.41
FEATURE [App::DocumentObjectGroupPython] Mg_element001  label="Mg_element : 0.002"  # scripted group (container) (typed FeaturePython)
  n = 0.002
FEATURE [App::DocumentObjectGroupPython] P_element002  label="P_element : 0.070"  # scripted group (container) (typed FeaturePython)
  n = 0.07
FEATURE [App::DocumentObjectGroupPython] S_element004  label="S_element : 0.003"  # scripted group (container) (typed FeaturePython)
  n = 0.002
FEATURE [App::DocumentObjectGroupPython] Ca_element003  label="Ca_element : 0.147"  # scripted group (container) (typed FeaturePython)
  n = 0.147
FEATURE [App::DocumentObjectGroupPython] G4_BONE_COMPACT_ICRU  # scripted group (container) (typed FeaturePython)
  Dunit = g/cm3
  Dvalue = 1.85
  Group = -> [H_element015,C_element015,N_element010,O_element014,Mg_element001,P_element002,S_element004,Ca_element003]
  conduct = 2
  density = 1
  expand = 3
  formula = G4_BONE_COMPACT_ICRU
  name = G4_BONE_COMPACT_ICRU
  specific = 4
FEATURE [App::DocumentObjectGroupPython] H_element016  label="H_element : 0.034"  # scripted group (container) (typed FeaturePython)
  n = 0.034
FEATURE [App::DocumentObjectGroupPython] C_element016  label="C_element : 0.155"  # scripted group (container) (typed FeaturePython)
  n = 0.155
FEATURE [App::DocumentObjectGroupPython] N_element011  label="N_element : 0.042"  # scripted group (container) (typed FeaturePython)
  n = 0.042
FEATURE [App::DocumentObjectGroupPython] O_element015  label="O_element : 0.435"  # scripted group (container) (typed FeaturePython)
  n = 0.435
FEATURE [App::DocumentObjectGroupPython] Na_element003  label="Na_element : 0.003"  # scripted group (container) (typed FeaturePython)
  n = 0.001
FEATURE [App::DocumentObjectGroupPython] Mg_element002  label="Mg_element : 0.003"  # scripted group (container) (typed FeaturePython)
  n = 0.002
FEATURE [App::DocumentObjectGroupPython] P_element003  label="P_element : 0.103"  # scripted group (container) (typed FeaturePython)
  n = 0.103
FEATURE [App::DocumentObjectGroupPython] S_element005  label="S_element : 0.004"  # scripted group (container) (typed FeaturePython)
  n = 0.003
FEATURE [App::DocumentObjectGroupPython] Ca_element004  label="Ca_element : 0.225"  # scripted group (container) (typed FeaturePython)
  n = 0.225
FEATURE [App::DocumentObjectGroupPython] G4_BONE_CORTICAL_ICRP  # scripted group (container) (typed FeaturePython)
  Dunit = g/cm3
  Dvalue = 1.92
  Group = -> [H_element016,C_element016,N_element011,O_element015,Na_element003,Mg_element002,P_element003,S_element005,Ca_element004]
  conduct = 2
  density = 1
  expand = 3
  formula = G4_BONE_CORTICAL_ICRP
  name = G4_BONE_CORTICAL_ICRP
  specific = 4
FEATURE [App::DocumentObjectGroupPython] B_element001  label="B_element : 4"  # scripted group (container) (typed FeaturePython)
  n = 4
  ref = B_element
FEATURE [App::DocumentObjectGroupPython] C_element017  label="C_element : 1"  # scripted group (container) (typed FeaturePython)
  n = 1
  ref = C_element
FEATURE [App::DocumentObjectGroupPython] G4_BORON_CARBIDE  # scripted group (container) (typed FeaturePython)
  Dunit = g/cm3
  Dvalue = 2.52
  Group = -> [B_element001,C_element017]
  conduct = 2
  density = 1
  expand = 3
  formula = G4_BORON_CARBIDE
  name = G4_BORON_CARBIDE
  specific = 4
FEATURE [App::DocumentObjectGroupPython] B_element002  label="B_element : 2"  # scripted group (container) (typed FeaturePython)
  n = 2
  ref = B_element
FEATURE [App::DocumentObjectGroupPython] O_element016  label="O_element : 006"  # scripted group (container) (typed FeaturePython)
  n = 3
  ref = O_element
FEATURE [App::DocumentObjectGroupPython] G4_BORON_OXIDE  # scripted group (container) (typed FeaturePython)
  Dunit = g/cm3
  Dvalue = 1.812
  Group = -> [B_element002,O_element016]
  conduct = 2
  density = 1
  expand = 3
  formula = G4_BORON_OXIDE
  name = G4_BORON_OXIDE
  specific = 4
FEATURE [App::DocumentObjectGroupPython] H_element017  label="H_element : 0.107"  # scripted group (container) (typed FeaturePython)
  n = 0.107
FEATURE [App::DocumentObjectGroupPython] C_element018  label="C_element : 0.145"  # scripted group (container) (typed FeaturePython)
  n = 0.145
FEATURE [App::DocumentObjectGroupPython] N_element012  label="N_element : 0.022"  # scripted group (container) (typed FeaturePython)
  n = 0.022
FEATURE [App::DocumentObjectGroupPython] O_element017  label="O_element : 0.712"  # scripted group (container) (typed FeaturePython)
  n = 0.712
FEATURE [App::DocumentObjectGroupPython] Na_element004  label="Na_element : 0.004"  # scripted group (container) (typed FeaturePython)
  n = 0.002
FEATURE [App::DocumentObjectGroupPython] P_element004  label="P_element : 0.004"  # scripted group (container) (typed FeaturePython)
  n = 0.004
FEATURE [App::DocumentObjectGroupPython] S_element006  label="S_element : 0.005"  # scripted group (container) (typed FeaturePython)
  n = 0.002
FEATURE [App::DocumentObjectGroupPython] Cl_element003  label="Cl_element : 0.004"  # scripted group (container) (typed FeaturePython)
  n = 0.003
FEATURE [App::DocumentObjectGroupPython] K_element002  label="K_element : 0.003"  # scripted group (container) (typed FeaturePython)
  n = 0.003
FEATURE [App::DocumentObjectGroupPython] G4_BRAIN_ICRP  # scripted group (container) (typed FeaturePython)
  Dunit = g/cm3
  Dvalue = 1.04
  Group = -> [H_element017,C_element018,N_element012,O_element017,Na_element004,P_element004,S_element006,Cl_element003,K_element002]
  conduct = 2
  density = 1
  expand = 3
  formula = G4_BRAIN_ICRP
  name = G4_BRAIN_ICRP
  specific = 4
FEATURE [App::DocumentObjectGroupPython] C_element019  label="C_element : 4"  # scripted group (container) (typed FeaturePython)
  n = 4
  ref = C_element
FEATURE [App::DocumentObjectGroupPython] H_element018  label="H_element : 010"  # scripted group (container) (typed FeaturePython)
  n = 10
  ref = H_element
FEATURE [App::DocumentObjectGroupPython] G4_BUTANE  # scripted group (container) (typed FeaturePython)
  Dunit = g/cm3
  Dvalue = 0.00249343
  Group = -> [C_element019,H_element018]
  conduct = 2
  density = 1
  expand = 3
  formula = G4_BUTANE
  name = G4_BUTANE
  specific = 4
FEATURE [App::DocumentObjectGroupPython] C_element020  label="C_element : 008"  # scripted group (container) (typed FeaturePython)
  n = 4
  ref = C_element
FEATURE [App::DocumentObjectGroupPython] H_element019  label="H_element : 011"  # scripted group (container) (typed FeaturePython)
  n = 10
  ref = H_element
FEATURE [App::DocumentObjectGroupPython] O_element018  label="O_element : 007"  # scripted group (container) (typed FeaturePython)
  n = 1
  ref = O_element
FEATURE [App::DocumentObjectGroupPython] G4_N_BUTYL_ALCOHOL  label="G4_N-BUTYL_ALCOHOL"  # scripted group (container) (typed FeaturePython)
  Dunit = g/cm3
  Dvalue = 0.8098
  Group = -> [C_element020,H_element019,O_element018]
  conduct = 2
  density = 1
  expand = 3
  formula = G4_N-BUTYL_ALCOHOL
  name = G4_N-BUTYL_ALCOHOL
  specific = 4
FEATURE [App::DocumentObjectGroupPython] H_element020  label="H_element : 0.025"  # scripted group (container) (typed FeaturePython)
  n = 0.02468
FEATURE [App::DocumentObjectGroupPython] C_element021  label="C_element : 0.502"  # scripted group (container) (typed FeaturePython)
  n = 0.501611
FEATURE [App::DocumentObjectGroupPython] O_element019  label="O_element : 0.005"  # scripted group (container) (typed FeaturePython)
  n = 0.004527
FEATURE [App::DocumentObjectGroupPython] F_element004  label="F_element : 0.465"  # scripted group (container) (typed FeaturePython)
  n = 0.465209
FEATURE [App::DocumentObjectGroupPython] Si_element001  label="Si_element : 0.004"  # scripted group (container) (typed FeaturePython)
  n = 0.003973
FEATURE [App::DocumentObjectGroupPython] G4_C_552  label="G4_C-552"  # scripted group (container) (typed FeaturePython)
  Dunit = g/cm3
  Dvalue = 1.76
  Group = -> [H_element020,C_element021,O_element019,F_element004,Si_element001]
  conduct = 2
  density = 1
  expand = 3
  formula = G4_C-552
  name = G4_C-552
  specific = 4
FEATURE [App::DocumentObjectGroupPython] Cd_element001  label="Cd_element : 1"  # scripted group (container) (typed FeaturePython)
  n = 1
  ref = Cd_element
FEATURE [App::DocumentObjectGroupPython] Te_element001  label="Te_element : 1"  # scripted group (container) (typed FeaturePython)
  n = 1
  ref = Te_element
FEATURE [App::DocumentObjectGroupPython] G4_CADMIUM_TELLURIDE  # scripted group (container) (typed FeaturePython)
  Dunit = g/cm3
  Dvalue = 6.2
  Group = -> [Cd_element001,Te_element001]
  conduct = 2
  density = 1
  expand = 3
  formula = G4_CADMIUM_TELLURIDE
  name = G4_CADMIUM_TELLURIDE
  specific = 4
FEATURE [App::DocumentObjectGroupPython] Cd_element002  label="Cd_element : 002"  # scripted group (container) (typed FeaturePython)
  n = 1
  ref = Cd_element
FEATURE [App::DocumentObjectGroupPython] W_element001  label="W_element : 1"  # scripted group (container) (typed FeaturePython)
  n = 1
  ref = W_element
FEATURE [App::DocumentObjectGroupPython] O_element020  label="O_element : 008"  # scripted group (container) (typed FeaturePython)
  n = 4
  ref = O_element
FEATURE [App::DocumentObjectGroupPython] G4_CADMIUM_TUNGSTATE  # scripted group (container) (typed FeaturePython)
  Dunit = g/cm3
  Dvalue = 7.9
  Group = -> [Cd_element002,W_element001,O_element020]
  conduct = 2
  density = 1
  expand = 3
  formula = G4_CADMIUM_TUNGSTATE
  name = G4_CADMIUM_TUNGSTATE
  specific = 4
FEATURE [App::DocumentObjectGroupPython] Ca_element005  label="Ca_element : 1"  # scripted group (container) (typed FeaturePython)
  n = 1
  ref = Ca_element
FEATURE [App::DocumentObjectGroupPython] C_element022  label="C_element : 009"  # scripted group (container) (typed FeaturePython)
  n = 1
  ref = C_element
FEATURE [App::DocumentObjectGroupPython] O_element021  label="O_element : 009"  # scripted group (container) (typed FeaturePython)
  n = 3
  ref = O_element
FEATURE [App::DocumentObjectGroupPython] G4_CALCIUM_CARBONATE  # scripted group (container) (typed FeaturePython)
  Dunit = g/cm3
  Dvalue = 2.8
  Group = -> [Ca_element005,C_element022,O_element021]
  conduct = 2
  density = 1
  expand = 3
  formula = G4_CALCIUM_CARBONATE
  name = G4_CALCIUM_CARBONATE
  specific = 4
FEATURE [App::DocumentObjectGroupPython] Ca_element006  label="Ca_element : 002"  # scripted group (container) (typed FeaturePython)
  n = 1
  ref = Ca_element
FEATURE [App::DocumentObjectGroupPython] F_element005  label="F_element : 003"  # scripted group (container) (typed FeaturePython)
  n = 2
  ref = F_element
FEATURE [App::DocumentObjectGroupPython] G4_CALCIUM_FLUORIDE  # scripted group (container) (typed FeaturePython)
  Dunit = g/cm3
  Dvalue = 3.18
  Group = -> [Ca_element006,F_element005]
  conduct = 2
  density = 1
  expand = 3
  formula = G4_CALCIUM_FLUORIDE
  name = G4_CALCIUM_FLUORIDE
  specific = 4
FEATURE [App::DocumentObjectGroupPython] Ca_element007  label="Ca_element : 003"  # scripted group (container) (typed FeaturePython)
  n = 1
  ref = Ca_element
FEATURE [App::DocumentObjectGroupPython] O_element022  label="O_element : 010"  # scripted group (container) (typed FeaturePython)
  n = 1
  ref = O_element
FEATURE [App::DocumentObjectGroupPython] G4_CALCIUM_OXIDE  # scripted group (container) (typed FeaturePython)
  Dunit = g/cm3
  Dvalue = 3.3
  Group = -> [Ca_element007,O_element022]
  conduct = 2
  density = 1
  expand = 3
  formula = G4_CALCIUM_OXIDE
  name = G4_CALCIUM_OXIDE
  specific = 4
FEATURE [App::DocumentObjectGroupPython] Ca_element008  label="Ca_element : 004"  # scripted group (container) (typed FeaturePython)
  n = 1
  ref = Ca_element
FEATURE [App::DocumentObjectGroupPython] S_element007  label="S_element : 002"  # scripted group (container) (typed FeaturePython)
  n = 1
  ref = S_element
FEATURE [App::DocumentObjectGroupPython] O_element023  label="O_element : 011"  # scripted group (container) (typed FeaturePython)
  n = 4
  ref = O_element
FEATURE [App::DocumentObjectGroupPython] G4_CALCIUM_SULFATE  # scripted group (container) (typed FeaturePython)
  Dunit = g/cm3
  Dvalue = 2.96
  Group = -> [Ca_element008,S_element007,O_element023]
  conduct = 2
  density = 1
  expand = 3
  formula = G4_CALCIUM_SULFATE
  name = G4_CALCIUM_SULFATE
  specific = 4
FEATURE [App::DocumentObjectGroupPython] Ca_element009  label="Ca_element : 005"  # scripted group (container) (typed FeaturePython)
  n = 1
  ref = Ca_element
FEATURE [App::DocumentObjectGroupPython] W_element002  label="W_element : 002"  # scripted group (container) (typed FeaturePython)
  n = 1
  ref = W_element
FEATURE [App::DocumentObjectGroupPython] O_element024  label="O_element : 012"  # scripted group (container) (typed FeaturePython)
  n = 4
  ref = O_element
FEATURE [App::DocumentObjectGroupPython] G4_CALCIUM_TUNGSTATE  # scripted group (container) (typed FeaturePython)
  Dunit = g/cm3
  Dvalue = 6.062
  Group = -> [Ca_element009,W_element002,O_element024]
  conduct = 2
  density = 1
  expand = 3
  formula = G4_CALCIUM_TUNGSTATE
  name = G4_CALCIUM_TUNGSTATE
  specific = 4
FEATURE [App::DocumentObjectGroupPython] C_element023  label="C_element : 010"  # scripted group (container) (typed FeaturePython)
  n = 1
  ref = C_element
FEATURE [App::DocumentObjectGroupPython] O_element025  label="O_element : 013"  # scripted group (container) (typed FeaturePython)
  n = 2
  ref = O_element
FEATURE [App::DocumentObjectGroupPython] G4_CARBON_DIOXIDE  # scripted group (container) (typed FeaturePython)
  Dunit = g/cm3
  Dvalue = 0.00184212
  Group = -> [C_element023,O_element025]
  conduct = 2
  density = 1
  expand = 3
  formula = G4_CARBON_DIOXIDE
  name = G4_CARBON_DIOXIDE
  specific = 4
FEATURE [App::DocumentObjectGroupPython] C_element024  label="C_element : 011"  # scripted group (container) (typed FeaturePython)
  n = 1
  ref = C_element
FEATURE [App::DocumentObjectGroupPython] Cl_element004  label="Cl_element : 4"  # scripted group (container) (typed FeaturePython)
  n = 4
  ref = Cl_element
FEATURE [App::DocumentObjectGroupPython] G4_CARBON_TETRACHLORIDE  # scripted group (container) (typed FeaturePython)
  Dunit = g/cm3
  Dvalue = 1.594
  Group = -> [C_element024,Cl_element004]
  conduct = 2
  density = 1
  expand = 3
  formula = G4_CARBON_TETRACHLORIDE
  name = G4_CARBON_TETRACHLORIDE
  specific = 4
FEATURE [App::DocumentObjectGroupPython] C_element025  label="C_element : 012"  # scripted group (container) (typed FeaturePython)
  n = 6
  ref = C_element
FEATURE [App::DocumentObjectGroupPython] H_element021  label="H_element : 012"  # scripted group (container) (typed FeaturePython)
  n = 10
  ref = H_element
FEATURE [App::DocumentObjectGroupPython] O_element026  label="O_element : 5"  # scripted group (container) (typed FeaturePython)
  n = 5
  ref = O_element
FEATURE [App::DocumentObjectGroupPython] G4_CELLULOSE_CELLOPHANE  # scripted group (container) (typed FeaturePython)
  Dunit = g/cm3
  Dvalue = 1.42
  Group = -> [C_element025,H_element021,O_element026]
  conduct = 2
  density = 1
  expand = 3
  formula = G4_CELLULOSE_CELLOPHANE
  name = G4_CELLULOSE_CELLOPHANE
  specific = 4
FEATURE [App::DocumentObjectGroupPython] H_element022  label="H_element : 0.067"  # scripted group (container) (typed FeaturePython)
  n = 0.067125
FEATURE [App::DocumentObjectGroupPython] C_element026  label="C_element : 0.545"  # scripted group (container) (typed FeaturePython)
  n = 0.545403
FEATURE [App::DocumentObjectGroupPython] O_element027  label="O_element : 0.387"  # scripted group (container) (typed FeaturePython)
  n = 0.387472
FEATURE [App::DocumentObjectGroupPython] G4_CELLULOSE_BUTYRATE  # scripted group (container) (typed FeaturePython)
  Dunit = g/cm3
  Dvalue = 1.2
  Group = -> [H_element022,C_element026,O_element027]
  conduct = 2
  density = 1
  expand = 3
  formula = G4_CELLULOSE_BUTYRATE
  name = G4_CELLULOSE_BUTYRATE
  specific = 4
FEATURE [App::DocumentObjectGroupPython] H_element023  label="H_element : 0.029"  # scripted group (container) (typed FeaturePython)
  n = 0.029216
FEATURE [App::DocumentObjectGroupPython] C_element027  label="C_element : 0.271"  # scripted group (container) (typed FeaturePython)
  n = 0.271296
FEATURE [App::DocumentObjectGroupPython] N_element013  label="N_element : 0.121"  # scripted group (container) (typed FeaturePython)
  n = 0.121276
FEATURE [App::DocumentObjectGroupPython] O_element028  label="O_element : 0.578"  # scripted group (container) (typed FeaturePython)
  n = 0.578212
FEATURE [App::DocumentObjectGroupPython] G4_CELLULOSE_NITRATE  # scripted group (container) (typed FeaturePython)
  Dunit = g/cm3
  Dvalue = 1.49
  Group = -> [H_element023,C_element027,N_element013,O_element028]
  conduct = 2
  density = 1
  expand = 3
  formula = G4_CELLULOSE_NITRATE
  name = G4_CELLULOSE_NITRATE
  specific = 4
FEATURE [App::DocumentObjectGroupPython] H_element024  label="H_element : 0.108"  # scripted group (container) (typed FeaturePython)
  n = 0.107596
FEATURE [App::DocumentObjectGroupPython] N_element014  label="N_element : 0.001"  # scripted group (container) (typed FeaturePython)
  n = 0.0008
FEATURE [App::DocumentObjectGroupPython] O_element029  label="O_element : 0.875"  # scripted group (container) (typed FeaturePython)
  n = 0.874976
FEATURE [App::DocumentObjectGroupPython] S_element008  label="S_element : 0.015"  # scripted group (container) (typed FeaturePython)
  n = 0.014627
FEATURE [App::DocumentObjectGroupPython] Ce_element001  label="Ce_element : 0.002"  # scripted group (container) (typed FeaturePython)
  n = 0.002001
FEATURE [App::DocumentObjectGroupPython] G4_CERIC_SULFATE  # scripted group (container) (typed FeaturePython)
  Dunit = g/cm3
  Dvalue = 1.03
  Group = -> [H_element024,N_element014,O_element029,S_element008,Ce_element001]
  conduct = 2
  density = 1
  expand = 3
  formula = G4_CERIC_SULFATE
  name = G4_CERIC_SULFATE
  specific = 4
FEATURE [App::DocumentObjectGroupPython] Cs_element001  label="Cs_element : 1"  # scripted group (container) (typed FeaturePython)
  n = 1
  ref = Cs_element
FEATURE [App::DocumentObjectGroupPython] F_element006  label="F_element : 1"  # scripted group (container) (typed FeaturePython)
  n = 1
  ref = F_element
FEATURE [App::DocumentObjectGroupPython] G4_CESIUM_FLUORIDE  # scripted group (container) (typed FeaturePython)
  Dunit = g/cm3
  Dvalue = 4.115
  Group = -> [Cs_element001,F_element006]
  conduct = 2
  density = 1
  expand = 3
  formula = G4_CESIUM_FLUORIDE
  name = G4_CESIUM_FLUORIDE
  specific = 4
FEATURE [App::DocumentObjectGroupPython] Cs_element002  label="Cs_element : 002"  # scripted group (container) (typed FeaturePython)
  n = 1
  ref = Cs_element
FEATURE [App::DocumentObjectGroupPython] I_element001  label="I_element : 1"  # scripted group (container) (typed FeaturePython)
  n = 1
  ref = I_element
FEATURE [App::DocumentObjectGroupPython] G4_CESIUM_IODIDE  # scripted group (container) (typed FeaturePython)
  Dunit = g/cm3
  Dvalue = 4.51
  Group = -> [Cs_element002,I_element001]
  conduct = 2
  density = 1
  expand = 3
  formula = G4_CESIUM_IODIDE
  name = G4_CESIUM_IODIDE
  specific = 4
FEATURE [App::DocumentObjectGroupPython] C_element028  label="C_element : 013"  # scripted group (container) (typed FeaturePython)
  n = 6
  ref = C_element
FEATURE [App::DocumentObjectGroupPython] H_element025  label="H_element : 013"  # scripted group (container) (typed FeaturePython)
  n = 5
  ref = H_element
FEATURE [App::DocumentObjectGroupPython] Cl_element005  label="Cl_element : 1"  # scripted group (container) (typed FeaturePython)
  n = 1
  ref = Cl_element
FEATURE [App::DocumentObjectGroupPython] G4_CHLOROBENZENE  # scripted group (container) (typed FeaturePython)
  Dunit = g/cm3
  Dvalue = 1.1058
  Group = -> [C_element028,H_element025,Cl_element005]
  conduct = 2
  density = 1
  expand = 3
  formula = G4_CHLOROBENZENE
  name = G4_CHLOROBENZENE
  specific = 4
FEATURE [App::DocumentObjectGroupPython] C_element029  label="C_element : 014"  # scripted group (container) (typed FeaturePython)
  n = 1
  ref = C_element
FEATURE [App::DocumentObjectGroupPython] H_element026  label="H_element : 1"  # scripted group (container) (typed FeaturePython)
  n = 1
  ref = H_element
FEATURE [App::DocumentObjectGroupPython] Cl_element006  label="Cl_element : 3"  # scripted group (container) (typed FeaturePython)
  n = 3
  ref = Cl_element
FEATURE [App::DocumentObjectGroupPython] G4_CHLOROFORM  # scripted group (container) (typed FeaturePython)
  Dunit = g/cm3
  Dvalue = 1.4832
  Group = -> [C_element029,H_element026,Cl_element006]
  conduct = 2
  density = 1
  expand = 3
  formula = G4_CHLOROFORM
  name = G4_CHLOROFORM
  specific = 4
FEATURE [App::DocumentObjectGroupPython] H_element027  label="H_element : 0.010"  # scripted group (container) (typed FeaturePython)
  n = 0.01
FEATURE [App::DocumentObjectGroupPython] C_element030  label="C_element : 0.001"  # scripted group (container) (typed FeaturePython)
  n = 0.001
FEATURE [App::DocumentObjectGroupPython] O_element030  label="O_element : 0.529"  # scripted group (container) (typed FeaturePython)
  n = 0.529107
FEATURE [App::DocumentObjectGroupPython] Na_element005  label="Na_element : 0.016"  # scripted group (container) (typed FeaturePython)
  n = 0.016
FEATURE [App::DocumentObjectGroupPython] Mg_element003  label="Mg_element : 0.004"  # scripted group (container) (typed FeaturePython)
  n = 0.002
FEATURE [App::DocumentObjectGroupPython] Al_element002  label="Al_element : 0.034"  # scripted group (container) (typed FeaturePython)
  n = 0.033872
FEATURE [App::DocumentObjectGroupPython] Si_element002  label="Si_element : 0.337"  # scripted group (container) (typed FeaturePython)
  n = 0.337021
FEATURE [App::DocumentObjectGroupPython] K_element003  label="K_element : 0.013"  # scripted group (container) (typed FeaturePython)
  n = 0.013
FEATURE [App::DocumentObjectGroupPython] Ca_element010  label="Ca_element : 0.044"  # scripted group (container) (typed FeaturePython)
  n = 0.044
FEATURE [App::DocumentObjectGroupPython] Fe_element002  label="Fe_element : 0.014"  # scripted group (container) (typed FeaturePython)
  n = 0.014
FEATURE [App::DocumentObjectGroupPython] G4_CONCRETE  # scripted group (container) (typed FeaturePython)
  Dunit = g/cm3
  Dvalue = 2.3
  Group = -> [H_element027,C_element030,O_element030,Na_element005,Mg_element003,Al_element002,Si_element002,K_element003,Ca_element010,Fe_element002]
  conduct = 2
  density = 1
  expand = 3
  formula = G4_CONCRETE
  name = G4_CONCRETE
  specific = 4
FEATURE [App::DocumentObjectGroupPython] C_element031  label="C_element : 015"  # scripted group (container) (typed FeaturePython)
  n = 6
  ref = C_element
FEATURE [App::DocumentObjectGroupPython] H_element028  label="H_element : 12"  # scripted group (container) (typed FeaturePython)
  n = 12
  ref = H_element
FEATURE [App::DocumentObjectGroupPython] G4_CYCLOHEXANE  # scripted group (container) (typed FeaturePython)
  Dunit = g/cm3
  Dvalue = 0.779
  Group = -> [C_element031,H_element028]
  conduct = 2
  density = 1
  expand = 3
  formula = G4_CYCLOHEXANE
  name = G4_CYCLOHEXANE
  specific = 4
FEATURE [App::DocumentObjectGroupPython] C_element032  label="C_element : 016"  # scripted group (container) (typed FeaturePython)
  n = 6
  ref = C_element
FEATURE [App::DocumentObjectGroupPython] H_element029  label="H_element : 4"  # scripted group (container) (typed FeaturePython)
  n = 4
  ref = H_element
FEATURE [App::DocumentObjectGroupPython] Cl_element007  label="Cl_element : 2"  # scripted group (container) (typed FeaturePython)
  n = 2
  ref = Cl_element
FEATURE [App::DocumentObjectGroupPython] G4_1_2_DICHLOROBENZENE  label="G4_1.2-DICHLOROBENZENE"  # scripted group (container) (typed FeaturePython)
  Dunit = g/cm3
  Dvalue = 1.3048
  Group = -> [C_element032,H_element029,Cl_element007]
  conduct = 2
  density = 1
  expand = 3
  formula = G4_1.2-DICHLOROBENZENE
  name = G4_1.2-DICHLOROBENZENE
  specific = 4
FEATURE [App::DocumentObjectGroupPython] C_element033  label="C_element : 017"  # scripted group (container) (typed FeaturePython)
  n = 4
  ref = C_element
FEATURE [App::DocumentObjectGroupPython] H_element030  label="H_element : 8"  # scripted group (container) (typed FeaturePython)
  n = 8
  ref = H_element
FEATURE [App::DocumentObjectGroupPython] O_element031  label="O_element : 014"  # scripted group (container) (typed FeaturePython)
  n = 1
  ref = O_element
FEATURE [App::DocumentObjectGroupPython] Cl_element008  label="Cl_element : 005"  # scripted group (container) (typed FeaturePython)
  n = 2
  ref = Cl_element
FEATURE [App::DocumentObjectGroupPython] G4_DICHLORODIETHYL_ETHER  # scripted group (container) (typed FeaturePython)
  Dunit = g/cm3
  Dvalue = 1.2199
  Group = -> [C_element033,H_element030,O_element031,Cl_element008]
  conduct = 2
  density = 1
  expand = 3
  formula = G4_DICHLORODIETHYL_ETHER
  name = G4_DICHLORODIETHYL_ETHER
  specific = 4
FEATURE [App::DocumentObjectGroupPython] C_element034  label="C_element : 018"  # scripted group (container) (typed FeaturePython)
  n = 2
  ref = C_element
FEATURE [App::DocumentObjectGroupPython] H_element031  label="H_element : 014"  # scripted group (container) (typed FeaturePython)
  n = 4
  ref = H_element
FEATURE [App::DocumentObjectGroupPython] Cl_element009  label="Cl_element : 006"  # scripted group (container) (typed FeaturePython)
  n = 2
  ref = Cl_element
FEATURE [App::DocumentObjectGroupPython] G4_1_2_DICHLOROETHANE  label="G4_1.2-DICHLOROETHANE"  # scripted group (container) (typed FeaturePython)
  Dunit = g/cm3
  Dvalue = 1.2351
  Group = -> [C_element034,H_element031,Cl_element009]
  conduct = 2
  density = 1
  expand = 3
  formula = G4_1.2-DICHLOROETHANE
  name = G4_1.2-DICHLOROETHANE
  specific = 4
FEATURE [App::DocumentObjectGroupPython] C_element035  label="C_element : 019"  # scripted group (container) (typed FeaturePython)
  n = 4
  ref = C_element
FEATURE [App::DocumentObjectGroupPython] H_element032  label="H_element : 015"  # scripted group (container) (typed FeaturePython)
  n = 10
  ref = H_element
FEATURE [App::DocumentObjectGroupPython] O_element032  label="O_element : 015"  # scripted group (container) (typed FeaturePython)
  n = 1
  ref = O_element
FEATURE [App::DocumentObjectGroupPython] G4_DIETHYL_ETHER  # scripted group (container) (typed FeaturePython)
  Dunit = g/cm3
  Dvalue = 0.71378
  Group = -> [C_element035,H_element032,O_element032]
  conduct = 2
  density = 1
  expand = 3
  formula = G4_DIETHYL_ETHER
  name = G4_DIETHYL_ETHER
  specific = 4
FEATURE [App::DocumentObjectGroupPython] C_element036  label="C_element : 020"  # scripted group (container) (typed FeaturePython)
  n = 3
  ref = C_element
FEATURE [App::DocumentObjectGroupPython] H_element033  label="H_element : 016"  # scripted group (container) (typed FeaturePython)
  n = 7
  ref = H_element
FEATURE [App::DocumentObjectGroupPython] N_element015  label="N_element : 008"  # scripted group (container) (typed FeaturePython)
  n = 1
  ref = N_element
FEATURE [App::DocumentObjectGroupPython] O_element033  label="O_element : 016"  # scripted group (container) (typed FeaturePython)
  n = 1
  ref = O_element
FEATURE [App::DocumentObjectGroupPython] G4_N_N_DIMETHYL_FORMAMIDE  label="G4_N.N-DIMETHYL_FORMAMIDE"  # scripted group (container) (typed FeaturePython)
  Dunit = g/cm3
  Dvalue = 0.9487
  Group = -> [C_element036,H_element033,N_element015,O_element033]
  conduct = 2
  density = 1
  expand = 3
  formula = G4_N.N-DIMETHYL_FORMAMIDE
  name = G4_N.N-DIMETHYL_FORMAMIDE
  specific = 4
FEATURE [App::DocumentObjectGroupPython] C_element037  label="C_element : 021"  # scripted group (container) (typed FeaturePython)
  n = 2
  ref = C_element
FEATURE [App::DocumentObjectGroupPython] H_element034  label="H_element : 017"  # scripted group (container) (typed FeaturePython)
  n = 6
  ref = H_element
FEATURE [App::DocumentObjectGroupPython] O_element034  label="O_element : 017"  # scripted group (container) (typed FeaturePython)
  n = 1
  ref = O_element
FEATURE [App::DocumentObjectGroupPython] S_element009  label="S_element : 003"  # scripted group (container) (typed FeaturePython)
  n = 1
  ref = S_element
FEATURE [App::DocumentObjectGroupPython] G4_DIMETHYL_SULFOXIDE  # scripted group (container) (typed FeaturePython)
  Dunit = g/cm3
  Dvalue = 1.1014
  Group = -> [C_element037,H_element034,O_element034,S_element009]
  conduct = 2
  density = 1
  expand = 3
  formula = G4_DIMETHYL_SULFOXIDE
  name = G4_DIMETHYL_SULFOXIDE
  specific = 4
FEATURE [App::DocumentObjectGroupPython] C_element038  label="C_element : 022"  # scripted group (container) (typed FeaturePython)
  n = 2
  ref = C_element
FEATURE [App::DocumentObjectGroupPython] H_element035  label="H_element : 018"  # scripted group (container) (typed FeaturePython)
  n = 6
  ref = H_element
FEATURE [App::DocumentObjectGroupPython] G4_ETHANE  # scripted group (container) (typed FeaturePython)
  Dunit = g/cm3
  Dvalue = 0.00125324
  Group = -> [C_element038,H_element035]
  conduct = 2
  density = 1
  expand = 3
  formula = G4_ETHANE
  name = G4_ETHANE
  specific = 4
FEATURE [App::DocumentObjectGroupPython] C_element039  label="C_element : 023"  # scripted group (container) (typed FeaturePython)
  n = 2
  ref = C_element
FEATURE [App::DocumentObjectGroupPython] H_element036  label="H_element : 019"  # scripted group (container) (typed FeaturePython)
  n = 6
  ref = H_element
FEATURE [App::DocumentObjectGroupPython] O_element035  label="O_element : 018"  # scripted group (container) (typed FeaturePython)
  n = 1
  ref = O_element
FEATURE [App::DocumentObjectGroupPython] G4_ETHYL_ALCOHOL  # scripted group (container) (typed FeaturePython)
  Dunit = g/cm3
  Dvalue = 0.7893
  Group = -> [C_element039,H_element036,O_element035]
  conduct = 2
  density = 1
  expand = 3
  formula = G4_ETHYL_ALCOHOL
  name = G4_ETHYL_ALCOHOL
  specific = 4
FEATURE [App::DocumentObjectGroupPython] H_element037  label="H_element : 0.090"  # scripted group (container) (typed FeaturePython)
  n = 0.090027
FEATURE [App::DocumentObjectGroupPython] C_element040  label="C_element : 0.585"  # scripted group (container) (typed FeaturePython)
  n = 0.585182
FEATURE [App::DocumentObjectGroupPython] O_element036  label="O_element : 0.325"  # scripted group (container) (typed FeaturePython)
  n = 0.324791
FEATURE [App::DocumentObjectGroupPython] G4_ETHYL_CELLULOSE  # scripted group (container) (typed FeaturePython)
  Dunit = g/cm3
  Dvalue = 1.13
  Group = -> [H_element037,C_element040,O_element036]
  conduct = 2
  density = 1
  expand = 3
  formula = G4_ETHYL_CELLULOSE
  name = G4_ETHYL_CELLULOSE
  specific = 4
FEATURE [App::DocumentObjectGroupPython] C_element041  label="C_element : 024"  # scripted group (container) (typed FeaturePython)
  n = 2
  ref = C_element
FEATURE [App::DocumentObjectGroupPython] H_element038  label="H_element : 020"  # scripted group (container) (typed FeaturePython)
  n = 4
  ref = H_element
FEATURE [App::DocumentObjectGroupPython] G4_ETHYLENE  # scripted group (container) (typed FeaturePython)
  Dunit = g/cm3
  Dvalue = 0.00117497
  Group = -> [C_element041,H_element038]
  conduct = 2
  density = 1
  expand = 3
  formula = G4_ETHYLENE
  name = G4_ETHYLENE
  specific = 4
FEATURE [App::DocumentObjectGroupPython] H_element039  label="H_element : 0.096"  # scripted group (container) (typed FeaturePython)
  n = 0.096
FEATURE [App::DocumentObjectGroupPython] C_element042  label="C_element : 0.195"  # scripted group (container) (typed FeaturePython)
  n = 0.195
FEATURE [App::DocumentObjectGroupPython] N_element016  label="N_element : 0.057"  # scripted group (container) (typed FeaturePython)
  n = 0.057
FEATURE [App::DocumentObjectGroupPython] O_element037  label="O_element : 0.646"  # scripted group (container) (typed FeaturePython)
  n = 0.646
FEATURE [App::DocumentObjectGroupPython] Na_element006  label="Na_element : 0.017"  # scripted group (container) (typed FeaturePython)
  n = 0.001
FEATURE [App::DocumentObjectGroupPython] P_element005  label="P_element : 0.104"  # scripted group (container) (typed FeaturePython)
  n = 0.001
FEATURE [App::DocumentObjectGroupPython] S_element010  label="S_element : 0.016"  # scripted group (container) (typed FeaturePython)
  n = 0.003
FEATURE [App::DocumentObjectGroupPython] Cl_element010  label="Cl_element : 0.005"  # scripted group (container) (typed FeaturePython)
  n = 0.001
FEATURE [App::DocumentObjectGroupPython] G4_EYE_LENS_ICRP  # scripted group (container) (typed FeaturePython)
  Dunit = g/cm3
  Dvalue = 1.07
  Group = -> [H_element039,C_element042,N_element016,O_element037,Na_element006,P_element005,S_element010,Cl_element010]
  conduct = 2
  density = 1
  expand = 3
  formula = G4_EYE_LENS_ICRP
  name = G4_EYE_LENS_ICRP
  specific = 4
FEATURE [App::DocumentObjectGroupPython] Fe_element003  label="Fe_element : 2"  # scripted group (container) (typed FeaturePython)
  n = 2
  ref = Fe_element
FEATURE [App::DocumentObjectGroupPython] O_element038  label="O_element : 019"  # scripted group (container) (typed FeaturePython)
  n = 3
  ref = O_element
FEATURE [App::DocumentObjectGroupPython] G4_FERRIC_OXIDE  # scripted group (container) (typed FeaturePython)
  Dunit = g/cm3
  Dvalue = 5.2
  Group = -> [Fe_element003,O_element038]
  conduct = 2
  density = 1
  expand = 3
  formula = G4_FERRIC_OXIDE
  name = G4_FERRIC_OXIDE
  specific = 4
FEATURE [App::DocumentObjectGroupPython] Fe_element004  label="Fe_element : 1"  # scripted group (container) (typed FeaturePython)
  n = 1
  ref = Fe_element
FEATURE [App::DocumentObjectGroupPython] B_element003  label="B_element : 1"  # scripted group (container) (typed FeaturePython)
  n = 1
  ref = B_element
FEATURE [App::DocumentObjectGroupPython] G4_FERROBORIDE  # scripted group (container) (typed FeaturePython)
  Dunit = g/cm3
  Dvalue = 7.15
  Group = -> [Fe_element004,B_element003]
  conduct = 2
  density = 1
  expand = 3
  formula = G4_FERROBORIDE
  name = G4_FERROBORIDE
  specific = 4
FEATURE [App::DocumentObjectGroupPython] Fe_element005  label="Fe_element : 003"  # scripted group (container) (typed FeaturePython)
  n = 1
  ref = Fe_element
FEATURE [App::DocumentObjectGroupPython] O_element039  label="O_element : 020"  # scripted group (container) (typed FeaturePython)
  n = 1
  ref = O_element
FEATURE [App::DocumentObjectGroupPython] G4_FERROUS_OXIDE  # scripted group (container) (typed FeaturePython)
  Dunit = g/cm3
  Dvalue = 5.7
  Group = -> [Fe_element005,O_element039]
  conduct = 2
  density = 1
  expand = 3
  formula = G4_FERROUS_OXIDE
  name = G4_FERROUS_OXIDE
  specific = 4
FEATURE [App::DocumentObjectGroupPython] H_element040  label="H_element : 0.115"  # scripted group (container) (typed FeaturePython)
  n = 0.108259
FEATURE [App::DocumentObjectGroupPython] N_element017  label="N_element : 0.000"  # scripted group (container) (typed FeaturePython)
  n = 2.7e-05
FEATURE [App::DocumentObjectGroupPython] O_element040  label="O_element : 0.879"  # scripted group (container) (typed FeaturePython)
  n = 0.878636
FEATURE [App::DocumentObjectGroupPython] Na_element007  label="Na_element : 0.000"  # scripted group (container) (typed FeaturePython)
  n = 2.2e-05
FEATURE [App::DocumentObjectGroupPython] S_element011  label="S_element : 0.013"  # scripted group (container) (typed FeaturePython)
  n = 0.012968
FEATURE [App::DocumentObjectGroupPython] Cl_element011  label="Cl_element : 0.000"  # scripted group (container) (typed FeaturePython)
  n = 3.4e-05
FEATURE [App::DocumentObjectGroupPython] Fe_element006  label="Fe_element : 0.000"  # scripted group (container) (typed FeaturePython)
  n = 5.4e-05
FEATURE [App::DocumentObjectGroupPython] G4_FERROUS_SULFATE  # scripted group (container) (typed FeaturePython)
  Dunit = g/cm3
  Dvalue = 1.024
  Group = -> [H_element040,N_element017,O_element040,Na_element007,S_element011,Cl_element011,Fe_element006]
  conduct = 2
  density = 1
  expand = 3
  formula = G4_FERROUS_SULFATE
  name = G4_FERROUS_SULFATE
  specific = 4
FEATURE [App::DocumentObjectGroupPython] C_element043  label="C_element : 0.099"  # scripted group (container) (typed FeaturePython)
  n = 0.099335
FEATURE [App::DocumentObjectGroupPython] F_element007  label="F_element : 0.314"  # scripted group (container) (typed FeaturePython)
  n = 0.314247
FEATURE [App::DocumentObjectGroupPython] Cl_element012  label="Cl_element : 0.586"  # scripted group (container) (typed FeaturePython)
  n = 0.586418
FEATURE [App::DocumentObjectGroupPython] G4_FREON_12  label="G4_FREON-12"  # scripted group (container) (typed FeaturePython)
  Dunit = g/cm3
  Dvalue = 1.12
  Group = -> [C_element043,F_element007,Cl_element012]
  conduct = 2
  density = 1
  expand = 3
  formula = G4_FREON-12
  name = G4_FREON-12
  specific = 4
FEATURE [App::DocumentObjectGroupPython] C_element044  label="C_element : 0.057"  # scripted group (container) (typed FeaturePython)
  n = 0.057245
FEATURE [App::DocumentObjectGroupPython] F_element008  label="F_element : 0.181"  # scripted group (container) (typed FeaturePython)
  n = 0.181096
FEATURE [App::DocumentObjectGroupPython] Br_element001  label="Br_element : 0.762"  # scripted group (container) (typed FeaturePython)
  n = 0.761659
FEATURE [App::DocumentObjectGroupPython] G4_FREON_12B2  label="G4_FREON-12B2"  # scripted group (container) (typed FeaturePython)
  Dunit = g/cm3
  Dvalue = 1.8
  Group = -> [C_element044,F_element008,Br_element001]
  conduct = 2
  density = 1
  expand = 3
  formula = G4_FREON-12B2
  name = G4_FREON-12B2
  specific = 4
FEATURE [App::DocumentObjectGroupPython] C_element045  label="C_element : 0.115"  # scripted group (container) (typed FeaturePython)
  n = 0.114983
FEATURE [App::DocumentObjectGroupPython] F_element009  label="F_element : 0.546"  # scripted group (container) (typed FeaturePython)
  n = 0.545621
FEATURE [App::DocumentObjectGroupPython] Cl_element013  label="Cl_element : 0.339"  # scripted group (container) (typed FeaturePython)
  n = 0.339396
FEATURE [App::DocumentObjectGroupPython] G4_FREON_13  label="G4_FREON-13"  # scripted group (container) (typed FeaturePython)
  Dunit = g/cm3
  Dvalue = 0.95
  Group = -> [C_element045,F_element009,Cl_element013]
  conduct = 2
  density = 1
  expand = 3
  formula = G4_FREON-13
  name = G4_FREON-13
  specific = 4
FEATURE [App::DocumentObjectGroupPython] C_element046  label="C_element : 025"  # scripted group (container) (typed FeaturePython)
  n = 1
  ref = C_element
FEATURE [App::DocumentObjectGroupPython] F_element010  label="F_element : 3"  # scripted group (container) (typed FeaturePython)
  n = 3
  ref = F_element
FEATURE [App::DocumentObjectGroupPython] Br_element002  label="Br_element : 1"  # scripted group (container) (typed FeaturePython)
  n = 1
  ref = Br_element
FEATURE [App::DocumentObjectGroupPython] G4_FREON_13B1  label="G4_FREON-13B1"  # scripted group (container) (typed FeaturePython)
  Dunit = g/cm3
  Dvalue = 1.5
  Group = -> [C_element046,F_element010,Br_element002]
  conduct = 2
  density = 1
  expand = 3
  formula = G4_FREON-13B1
  name = G4_FREON-13B1
  specific = 4
FEATURE [App::DocumentObjectGroupPython] C_element047  label="C_element : 0.061"  # scripted group (container) (typed FeaturePython)
  n = 0.061309
FEATURE [App::DocumentObjectGroupPython] F_element011  label="F_element : 0.291"  # scripted group (container) (typed FeaturePython)
  n = 0.290924
FEATURE [App::DocumentObjectGroupPython] I_element002  label="I_element : 0.648"  # scripted group (container) (typed FeaturePython)
  n = 0.647767
FEATURE [App::DocumentObjectGroupPython] G4_FREON_13I1  label="G4_FREON-13I1"  # scripted group (container) (typed FeaturePython)
  Dunit = g/cm3
  Dvalue = 1.8
  Group = -> [C_element047,F_element011,I_element002]
  conduct = 2
  density = 1
  expand = 3
  formula = G4_FREON-13I1
  name = G4_FREON-13I1
  specific = 4
FEATURE [App::DocumentObjectGroupPython] Gd_element001  label="Gd_element : 2"  # scripted group (container) (typed FeaturePython)
  n = 2
  ref = Gd_element
FEATURE [App::DocumentObjectGroupPython] O_element041  label="O_element : 021"  # scripted group (container) (typed FeaturePython)
  n = 2
  ref = O_element
FEATURE [App::DocumentObjectGroupPython] S_element012  label="S_element : 004"  # scripted group (container) (typed FeaturePython)
  n = 1
  ref = S_element
FEATURE [App::DocumentObjectGroupPython] G4_GADOLINIUM_OXYSULFIDE  # scripted group (container) (typed FeaturePython)
  Dunit = g/cm3
  Dvalue = 7.44
  Group = -> [Gd_element001,O_element041,S_element012]
  conduct = 2
  density = 1
  expand = 3
  formula = G4_GADOLINIUM_OXYSULFIDE
  name = G4_GADOLINIUM_OXYSULFIDE
  specific = 4
FEATURE [App::DocumentObjectGroupPython] Ga_element001  label="Ga_element : 1"  # scripted group (container) (typed FeaturePython)
  n = 1
  ref = Ga_element
FEATURE [App::DocumentObjectGroupPython] As_element001  label="As_element : 1"  # scripted group (container) (typed FeaturePython)
  n = 1
  ref = As_element
FEATURE [App::DocumentObjectGroupPython] G4_GALLIUM_ARSENIDE  # scripted group (container) (typed FeaturePython)
  Dunit = g/cm3
  Dvalue = 5.31
  Group = -> [Ga_element001,As_element001]
  conduct = 2
  density = 1
  expand = 3
  formula = G4_GALLIUM_ARSENIDE
  name = G4_GALLIUM_ARSENIDE
  specific = 4
FEATURE [App::DocumentObjectGroupPython] H_element041  label="H_element : 0.081"  # scripted group (container) (typed FeaturePython)
  n = 0.08118
FEATURE [App::DocumentObjectGroupPython] C_element048  label="C_element : 0.416"  # scripted group (container) (typed FeaturePython)
  n = 0.41606
FEATURE [App::DocumentObjectGroupPython] N_element018  label="N_element : 0.111"  # scripted group (container) (typed FeaturePython)
  n = 0.11124
FEATURE [App::DocumentObjectGroupPython] O_element042  label="O_element : 0.381"  # scripted group (container) (typed FeaturePython)
  n = 0.38064
FEATURE [App::DocumentObjectGroupPython] S_element013  label="S_element : 0.011"  # scripted group (container) (typed FeaturePython)
  n = 0.01088
FEATURE [App::DocumentObjectGroupPython] G4_GEL_PHOTO_EMULSION  # scripted group (container) (typed FeaturePython)
  Dunit = g/cm3
  Dvalue = 1.2914
  Group = -> [H_element041,C_element048,N_element018,O_element042,S_element013]
  conduct = 2
  density = 1
  expand = 3
  formula = G4_GEL_PHOTO_EMULSION
  name = G4_GEL_PHOTO_EMULSION
  specific = 4
FEATURE [App::DocumentObjectGroupPython] B_element004  label="B_element : 0.040"  # scripted group (container) (typed FeaturePython)
  n = 0.0400639
FEATURE [App::DocumentObjectGroupPython] O_element043  label="O_element : 0.540"  # scripted group (container) (typed FeaturePython)
  n = 0.539561
FEATURE [App::DocumentObjectGroupPython] Na_element008  label="Na_element : 0.028"  # scripted group (container) (typed FeaturePython)
  n = 0.0281909
FEATURE [App::DocumentObjectGroupPython] Al_element003  label="Al_element : 0.012"  # scripted group (container) (typed FeaturePython)
  n = 0.011644
FEATURE [App::DocumentObjectGroupPython] Si_element003  label="Si_element : 0.377"  # scripted group (container) (typed FeaturePython)
  n = 0.377219
FEATURE [App::DocumentObjectGroupPython] K_element004  label="K_element : 0.014"  # scripted group (container) (typed FeaturePython)
  n = 0.00332099
FEATURE [App::DocumentObjectGroupPython] G4_Pyrex_Glass  # scripted group (container) (typed FeaturePython)
  Dunit = g/cm3
  Dvalue = 2.23
  Group = -> [B_element004,O_element043,Na_element008,Al_element003,Si_element003,K_element004]
  conduct = 2
  density = 1
  expand = 3
  formula = G4_Pyrex_Glass
  name = G4_Pyrex_Glass
  specific = 4
FEATURE [App::DocumentObjectGroupPython] O_element044  label="O_element : 0.156"  # scripted group (container) (typed FeaturePython)
  n = 0.156453
FEATURE [App::DocumentObjectGroupPython] Si_element004  label="Si_element : 0.081"  # scripted group (container) (typed FeaturePython)
  n = 0.080866
FEATURE [App::DocumentObjectGroupPython] Ti_element001  label="Ti_element : 0.008"  # scripted group (container) (typed FeaturePython)
  n = 0.008092
FEATURE [App::DocumentObjectGroupPython] As_element002  label="As_element : 0.003"  # scripted group (container) (typed FeaturePython)
  n = 0.002651
FEATURE [App::DocumentObjectGroupPython] Pb_element001  label="Pb_element : 0.752"  # scripted group (container) (typed FeaturePython)
  n = 0.751938
FEATURE [App::DocumentObjectGroupPython] G4_GLASS_LEAD  # scripted group (container) (typed FeaturePython)
  Dunit = g/cm3
  Dvalue = 6.22
  Group = -> [O_element044,Si_element004,Ti_element001,As_element002,Pb_element001]
  conduct = 2
  density = 1
  expand = 3
  formula = G4_GLASS_LEAD
  name = G4_GLASS_LEAD
  specific = 4
FEATURE [App::DocumentObjectGroupPython] O_element045  label="O_element : 0.460"  # scripted group (container) (typed FeaturePython)
  n = 0.4598
FEATURE [App::DocumentObjectGroupPython] Na_element009  label="Na_element : 0.096"  # scripted group (container) (typed FeaturePython)
  n = 0.0964411
FEATURE [App::DocumentObjectGroupPython] Si_element005  label="Si_element : 0.378"  # scripted group (container) (typed FeaturePython)
  n = 0.336553
FEATURE [App::DocumentObjectGroupPython] Ca_element011  label="Ca_element : 0.107"  # scripted group (container) (typed FeaturePython)
  n = 0.107205
FEATURE [App::DocumentObjectGroupPython] G4_GLASS_PLATE  # scripted group (container) (typed FeaturePython)
  Dunit = g/cm3
  Dvalue = 2.4
  Group = -> [O_element045,Na_element009,Si_element005,Ca_element011]
  conduct = 2
  density = 1
  expand = 3
  formula = G4_GLASS_PLATE
  name = G4_GLASS_PLATE
  specific = 4
FEATURE [App::DocumentObjectGroupPython] C_element049  label="C_element : 026"  # scripted group (container) (typed FeaturePython)
  n = 5
  ref = C_element
FEATURE [App::DocumentObjectGroupPython] H_element042  label="H_element : 021"  # scripted group (container) (typed FeaturePython)
  n = 10
  ref = H_element
FEATURE [App::DocumentObjectGroupPython] N_element019  label="N_element : 2"  # scripted group (container) (typed FeaturePython)
  n = 2
  ref = N_element
FEATURE [App::DocumentObjectGroupPython] O_element046  label="O_element : 022"  # scripted group (container) (typed FeaturePython)
  n = 3
  ref = O_element
FEATURE [App::DocumentObjectGroupPython] G4_GLUTAMINE  # scripted group (container) (typed FeaturePython)
  Dunit = g/cm3
  Dvalue = 1.46
  Group = -> [C_element049,H_element042,N_element019,O_element046]
  conduct = 2
  density = 1
  expand = 3
  formula = G4_GLUTAMINE
  name = G4_GLUTAMINE
  specific = 4
FEATURE [App::DocumentObjectGroupPython] C_element050  label="C_element : 027"  # scripted group (container) (typed FeaturePython)
  n = 3
  ref = C_element
FEATURE [App::DocumentObjectGroupPython] H_element043  label="H_element : 022"  # scripted group (container) (typed FeaturePython)
  n = 8
  ref = H_element
FEATURE [App::DocumentObjectGroupPython] O_element047  label="O_element : 023"  # scripted group (container) (typed FeaturePython)
  n = 3
  ref = O_element
FEATURE [App::DocumentObjectGroupPython] G4_GLYCEROL  # scripted group (container) (typed FeaturePython)
  Dunit = g/cm3
  Dvalue = 1.2613
  Group = -> [C_element050,H_element043,O_element047]
  conduct = 2
  density = 1
  expand = 3
  formula = G4_GLYCEROL
  name = G4_GLYCEROL
  specific = 4
FEATURE [App::DocumentObjectGroupPython] C_element051  label="C_element : 028"  # scripted group (container) (typed FeaturePython)
  n = 5
  ref = C_element
FEATURE [App::DocumentObjectGroupPython] H_element044  label="H_element : 023"  # scripted group (container) (typed FeaturePython)
  n = 5
  ref = H_element
FEATURE [App::DocumentObjectGroupPython] N_element020  label="N_element : 009"  # scripted group (container) (typed FeaturePython)
  n = 5
  ref = N_element
FEATURE [App::DocumentObjectGroupPython] O_element048  label="O_element : 024"  # scripted group (container) (typed FeaturePython)
  n = 1
  ref = O_element
FEATURE [App::DocumentObjectGroupPython] G4_GUANINE  # scripted group (container) (typed FeaturePython)
  Dunit = g/cm3
  Dvalue = 2.2
  Group = -> [C_element051,H_element044,N_element020,O_element048]
  conduct = 2
  density = 1
  expand = 3
  formula = G4_GUANINE
  name = G4_GUANINE
  specific = 4
FEATURE [App::DocumentObjectGroupPython] Ca_element012  label="Ca_element : 006"  # scripted group (container) (typed FeaturePython)
  n = 1
  ref = Ca_element
FEATURE [App::DocumentObjectGroupPython] S_element014  label="S_element : 005"  # scripted group (container) (typed FeaturePython)
  n = 1
  ref = S_element
FEATURE [App::DocumentObjectGroupPython] O_element049  label="O_element : 6"  # scripted group (container) (typed FeaturePython)
  n = 6
  ref = O_element
FEATURE [App::DocumentObjectGroupPython] H_element045  label="H_element : 024"  # scripted group (container) (typed FeaturePython)
  n = 4
  ref = H_element
FEATURE [App::DocumentObjectGroupPython] G4_GYPSUM  # scripted group (container) (typed FeaturePython)
  Dunit = g/cm3
  Dvalue = 2.32
  Group = -> [Ca_element012,S_element014,O_element049,H_element045]
  conduct = 2
  density = 1
  expand = 3
  formula = G4_GYPSUM
  name = G4_GYPSUM
  specific = 4
FEATURE [App::DocumentObjectGroupPython] C_element052  label="C_element : 7"  # scripted group (container) (typed FeaturePython)
  n = 7
  ref = C_element
FEATURE [App::DocumentObjectGroupPython] H_element046  label="H_element : 16"  # scripted group (container) (typed FeaturePython)
  n = 16
  ref = H_element
FEATURE [App::DocumentObjectGroupPython] G4_N_HEPTANE  label="G4_N-HEPTANE"  # scripted group (container) (typed FeaturePython)
  Dunit = g/cm3
  Dvalue = 0.68376
  Group = -> [C_element052,H_element046]
  conduct = 2
  density = 1
  expand = 3
  formula = G4_N-HEPTANE
  name = G4_N-HEPTANE
  specific = 4
FEATURE [App::DocumentObjectGroupPython] C_element053  label="C_element : 029"  # scripted group (container) (typed FeaturePython)
  n = 6
  ref = C_element
FEATURE [App::DocumentObjectGroupPython] H_element047  label="H_element : 14"  # scripted group (container) (typed FeaturePython)
  n = 14
  ref = H_element
FEATURE [App::DocumentObjectGroupPython] G4_N_HEXANE  label="G4_N-HEXANE"  # scripted group (container) (typed FeaturePython)
  Dunit = g/cm3
  Dvalue = 0.6603
  Group = -> [C_element053,H_element047]
  conduct = 2
  density = 1
  expand = 3
  formula = G4_N-HEXANE
  name = G4_N-HEXANE
  specific = 4
FEATURE [App::DocumentObjectGroupPython] C_element054  label="C_element : 22"  # scripted group (container) (typed FeaturePython)
  n = 22
  ref = C_element
FEATURE [App::DocumentObjectGroupPython] H_element048  label="H_element : 025"  # scripted group (container) (typed FeaturePython)
  n = 10
  ref = H_element
FEATURE [App::DocumentObjectGroupPython] N_element021  label="N_element : 010"  # scripted group (container) (typed FeaturePython)
  n = 2
  ref = N_element
FEATURE [App::DocumentObjectGroupPython] O_element050  label="O_element : 025"  # scripted group (container) (typed FeaturePython)
  n = 5
  ref = O_element
FEATURE [App::DocumentObjectGroupPython] G4_KAPTON  # scripted group (container) (typed FeaturePython)
  Dunit = g/cm3
  Dvalue = 1.42
  Group = -> [C_element054,H_element048,N_element021,O_element050]
  conduct = 2
  density = 1
  expand = 3
  formula = G4_KAPTON
  name = G4_KAPTON
  specific = 4
FEATURE [App::DocumentObjectGroupPython] La_element001  label="La_element : 1"  # scripted group (container) (typed FeaturePython)
  n = 1
  ref = La_element
FEATURE [App::DocumentObjectGroupPython] Br_element003  label="Br_element : 002"  # scripted group (container) (typed FeaturePython)
  n = 1
  ref = Br_element
FEATURE [App::DocumentObjectGroupPython] O_element051  label="O_element : 026"  # scripted group (container) (typed FeaturePython)
  n = 1
  ref = O_element
FEATURE [App::DocumentObjectGroupPython] G4_LANTHANUM_OXYBROMIDE  # scripted group (container) (typed FeaturePython)
  Dunit = g/cm3
  Dvalue = 6.28
  Group = -> [La_element001,Br_element003,O_element051]
  conduct = 2
  density = 1
  expand = 3
  formula = G4_LANTHANUM_OXYBROMIDE
  name = G4_LANTHANUM_OXYBROMIDE
  specific = 4
FEATURE [App::DocumentObjectGroupPython] La_element002  label="La_element : 2"  # scripted group (container) (typed FeaturePython)
  n = 2
  ref = La_element
FEATURE [App::DocumentObjectGroupPython] O_element052  label="O_element : 027"  # scripted group (container) (typed FeaturePython)
  n = 2
  ref = O_element
FEATURE [App::DocumentObjectGroupPython] S_element015  label="S_element : 006"  # scripted group (container) (typed FeaturePython)
  n = 1
  ref = S_element
FEATURE [App::DocumentObjectGroupPython] G4_LANTHANUM_OXYSULFIDE  # scripted group (container) (typed FeaturePython)
  Dunit = g/cm3
  Dvalue = 5.86
  Group = -> [La_element002,O_element052,S_element015]
  conduct = 2
  density = 1
  expand = 3
  formula = G4_LANTHANUM_OXYSULFIDE
  name = G4_LANTHANUM_OXYSULFIDE
  specific = 4
FEATURE [App::DocumentObjectGroupPython] O_element053  label="O_element : 0.072"  # scripted group (container) (typed FeaturePython)
  n = 0.071682
FEATURE [App::DocumentObjectGroupPython] Pb_element002  label="Pb_element : 0.928"  # scripted group (container) (typed FeaturePython)
  n = 0.928318
FEATURE [App::DocumentObjectGroupPython] G4_LEAD_OXIDE  # scripted group (container) (typed FeaturePython)
  Dunit = g/cm3
  Dvalue = 9.53
  Group = -> [O_element053,Pb_element002]
  conduct = 2
  density = 1
  expand = 3
  formula = G4_LEAD_OXIDE
  name = G4_LEAD_OXIDE
  specific = 4
FEATURE [App::DocumentObjectGroupPython] Li_element001  label="Li_element : 1"  # scripted group (container) (typed FeaturePython)
  n = 1
  ref = Li_element
FEATURE [App::DocumentObjectGroupPython] N_element022  label="N_element : 011"  # scripted group (container) (typed FeaturePython)
  n = 1
  ref = N_element
FEATURE [App::DocumentObjectGroupPython] H_element049  label="H_element : 026"  # scripted group (container) (typed FeaturePython)
  n = 2
  ref = H_element
FEATURE [App::DocumentObjectGroupPython] G4_LITHIUM_AMIDE  # scripted group (container) (typed FeaturePython)
  Dunit = g/cm3
  Dvalue = 1.178
  Group = -> [Li_element001,N_element022,H_element049]
  conduct = 2
  density = 1
  expand = 3
  formula = G4_LITHIUM_AMIDE
  name = G4_LITHIUM_AMIDE
  specific = 4
FEATURE [App::DocumentObjectGroupPython] Li_element002  label="Li_element : 2"  # scripted group (container) (typed FeaturePython)
  n = 2
  ref = Li_element
FEATURE [App::DocumentObjectGroupPython] C_element055  label="C_element : 030"  # scripted group (container) (typed FeaturePython)
  n = 1
  ref = C_element
FEATURE [App::DocumentObjectGroupPython] O_element054  label="O_element : 028"  # scripted group (container) (typed FeaturePython)
  n = 3
  ref = O_element
FEATURE [App::DocumentObjectGroupPython] G4_LITHIUM_CARBONATE  # scripted group (container) (typed FeaturePython)
  Dunit = g/cm3
  Dvalue = 2.11
  Group = -> [Li_element002,C_element055,O_element054]
  conduct = 2
  density = 1
  expand = 3
  formula = G4_LITHIUM_CARBONATE
  name = G4_LITHIUM_CARBONATE
  specific = 4
FEATURE [App::DocumentObjectGroupPython] Li_element003  label="Li_element : 003"  # scripted group (container) (typed FeaturePython)
  n = 1
  ref = Li_element
FEATURE [App::DocumentObjectGroupPython] F_element012  label="F_element : 004"  # scripted group (container) (typed FeaturePython)
  n = 1
  ref = F_element
FEATURE [App::DocumentObjectGroupPython] G4_LITHIUM_FLUORIDE  # scripted group (container) (typed FeaturePython)
  Dunit = g/cm3
  Dvalue = 2.635
  Group = -> [Li_element003,F_element012]
  conduct = 2
  density = 1
  expand = 3
  formula = G4_LITHIUM_FLUORIDE
  name = G4_LITHIUM_FLUORIDE
  specific = 4
FEATURE [App::DocumentObjectGroupPython] Li_element004  label="Li_element : 004"  # scripted group (container) (typed FeaturePython)
  n = 1
  ref = Li_element
FEATURE [App::DocumentObjectGroupPython] H_element050  label="H_element : 027"  # scripted group (container) (typed FeaturePython)
  n = 1
  ref = H_element
FEATURE [App::DocumentObjectGroupPython] G4_LITHIUM_HYDRIDE  # scripted group (container) (typed FeaturePython)
  Dunit = g/cm3
  Dvalue = 0.82
  Group = -> [Li_element004,H_element050]
  conduct = 2
  density = 1
  expand = 3
  formula = G4_LITHIUM_HYDRIDE
  name = G4_LITHIUM_HYDRIDE
  specific = 4
FEATURE [App::DocumentObjectGroupPython] Li_element005  label="Li_element : 005"  # scripted group (container) (typed FeaturePython)
  n = 1
  ref = Li_element
FEATURE [App::DocumentObjectGroupPython] I_element003  label="I_element : 002"  # scripted group (container) (typed FeaturePython)
  n = 1
  ref = I_element
FEATURE [App::DocumentObjectGroupPython] G4_LITHIUM_IODIDE  # scripted group (container) (typed FeaturePython)
  Dunit = g/cm3
  Dvalue = 3.494
  Group = -> [Li_element005,I_element003]
  conduct = 2
  density = 1
  expand = 3
  formula = G4_LITHIUM_IODIDE
  name = G4_LITHIUM_IODIDE
  specific = 4
FEATURE [App::DocumentObjectGroupPython] Li_element006  label="Li_element : 006"  # scripted group (container) (typed FeaturePython)
  n = 2
  ref = Li_element
FEATURE [App::DocumentObjectGroupPython] O_element055  label="O_element : 029"  # scripted group (container) (typed FeaturePython)
  n = 1
  ref = O_element
FEATURE [App::DocumentObjectGroupPython] G4_LITHIUM_OXIDE  # scripted group (container) (typed FeaturePython)
  Dunit = g/cm3
  Dvalue = 2.013
  Group = -> [Li_element006,O_element055]
  conduct = 2
  density = 1
  expand = 3
  formula = G4_LITHIUM_OXIDE
  name = G4_LITHIUM_OXIDE
  specific = 4
FEATURE [App::DocumentObjectGroupPython] Li_element007  label="Li_element : 007"  # scripted group (container) (typed FeaturePython)
  n = 2
  ref = Li_element
FEATURE [App::DocumentObjectGroupPython] B_element005  label="B_element : 005"  # scripted group (container) (typed FeaturePython)
  n = 4
  ref = B_element
FEATURE [App::DocumentObjectGroupPython] O_element056  label="O_element : 7"  # scripted group (container) (typed FeaturePython)
  n = 7
  ref = O_element
FEATURE [App::DocumentObjectGroupPython] G4_LITHIUM_TETRABORATE  # scripted group (container) (typed FeaturePython)
  Dunit = g/cm3
  Dvalue = 2.44
  Group = -> [Li_element007,B_element005,O_element056]
  conduct = 2
  density = 1
  expand = 3
  formula = G4_LITHIUM_TETRABORATE
  name = G4_LITHIUM_TETRABORATE
  specific = 4
FEATURE [App::DocumentObjectGroupPython] H_element051  label="H_element : 0.105"  # scripted group (container) (typed FeaturePython)
  n = 0.105
FEATURE [App::DocumentObjectGroupPython] C_element056  label="C_element : 0.083"  # scripted group (container) (typed FeaturePython)
  n = 0.083
FEATURE [App::DocumentObjectGroupPython] N_element023  label="N_element : 0.023"  # scripted group (container) (typed FeaturePython)
  n = 0.023
FEATURE [App::DocumentObjectGroupPython] O_element057  label="O_element : 0.779"  # scripted group (container) (typed FeaturePython)
  n = 0.779
FEATURE [App::DocumentObjectGroupPython] Na_element010  label="Na_element : 0.097"  # scripted group (container) (typed FeaturePython)
  n = 0.002
FEATURE [App::DocumentObjectGroupPython] P_element006  label="P_element : 0.105"  # scripted group (container) (typed FeaturePython)
  n = 0.001
FEATURE [App::DocumentObjectGroupPython] S_element016  label="S_element : 0.017"  # scripted group (container) (typed FeaturePython)
  n = 0.002
FEATURE [App::DocumentObjectGroupPython] Cl_element014  label="Cl_element : 0.587"  # scripted group (container) (typed FeaturePython)
  n = 0.003
FEATURE [App::DocumentObjectGroupPython] K_element005  label="K_element : 0.015"  # scripted group (container) (typed FeaturePython)
  n = 0.002
FEATURE [App::DocumentObjectGroupPython] G4_LUNG_ICRP  # scripted group (container) (typed FeaturePython)
  Dunit = g/cm3
  Dvalue = 1.04
  Group = -> [H_element051,C_element056,N_element023,O_element057,Na_element010,P_element006,S_element016,Cl_element014,K_element005]
  conduct = 2
  density = 1
  expand = 3
  formula = G4_LUNG_ICRP
  name = G4_LUNG_ICRP
  specific = 4
FEATURE [App::DocumentObjectGroupPython] H_element052  label="H_element : 0.116"  # scripted group (container) (typed FeaturePython)
  n = 0.114318
FEATURE [App::DocumentObjectGroupPython] C_element057  label="C_element : 0.656"  # scripted group (container) (typed FeaturePython)
  n = 0.655824
FEATURE [App::DocumentObjectGroupPython] O_element058  label="O_element : 0.092"  # scripted group (container) (typed FeaturePython)
  n = 0.0921831
FEATURE [App::DocumentObjectGroupPython] Mg_element004  label="Mg_element : 0.135"  # scripted group (container) (typed FeaturePython)
  n = 0.134792
FEATURE [App::DocumentObjectGroupPython] Ca_element013  label="Ca_element : 0.003"  # scripted group (container) (typed FeaturePython)
  n = 0.002883
FEATURE [App::DocumentObjectGroupPython] G4_M3_WAX  # scripted group (container) (typed FeaturePython)
  Dunit = g/cm3
  Dvalue = 1.05
  Group = -> [H_element052,C_element057,O_element058,Mg_element004,Ca_element013]
  conduct = 2
  density = 1
  expand = 3
  formula = G4_M3_WAX
  name = G4_M3_WAX
  specific = 4
FEATURE [App::DocumentObjectGroupPython] Mg_element005  label="Mg_element : 1"  # scripted group (container) (typed FeaturePython)
  n = 1
  ref = Mg_element
FEATURE [App::DocumentObjectGroupPython] C_element058  label="C_element : 031"  # scripted group (container) (typed FeaturePython)
  n = 1
  ref = C_element
FEATURE [App::DocumentObjectGroupPython] O_element059  label="O_element : 030"  # scripted group (container) (typed FeaturePython)
  n = 3
  ref = O_element
FEATURE [App::DocumentObjectGroupPython] G4_MAGNESIUM_CARBONATE  # scripted group (container) (typed FeaturePython)
  Dunit = g/cm3
  Dvalue = 2.958
  Group = -> [Mg_element005,C_element058,O_element059]
  conduct = 2
  density = 1
  expand = 3
  formula = G4_MAGNESIUM_CARBONATE
  name = G4_MAGNESIUM_CARBONATE
  specific = 4
FEATURE [App::DocumentObjectGroupPython] Mg_element006  label="Mg_element : 002"  # scripted group (container) (typed FeaturePython)
  n = 1
  ref = Mg_element
FEATURE [App::DocumentObjectGroupPython] F_element013  label="F_element : 005"  # scripted group (container) (typed FeaturePython)
  n = 2
  ref = F_element
FEATURE [App::DocumentObjectGroupPython] G4_MAGNESIUM_FLUORIDE  # scripted group (container) (typed FeaturePython)
  Dunit = g/cm3
  Dvalue = 3
  Group = -> [Mg_element006,F_element013]
  conduct = 2
  density = 1
  expand = 3
  formula = G4_MAGNESIUM_FLUORIDE
  name = G4_MAGNESIUM_FLUORIDE
  specific = 4
FEATURE [App::DocumentObjectGroupPython] Mg_element007  label="Mg_element : 003"  # scripted group (container) (typed FeaturePython)
  n = 1
  ref = Mg_element
FEATURE [App::DocumentObjectGroupPython] O_element060  label="O_element : 031"  # scripted group (container) (typed FeaturePython)
  n = 1
  ref = O_element
FEATURE [App::DocumentObjectGroupPython] G4_MAGNESIUM_OXIDE  # scripted group (container) (typed FeaturePython)
  Dunit = g/cm3
  Dvalue = 3.58
  Group = -> [Mg_element007,O_element060]
  conduct = 2
  density = 1
  expand = 3
  formula = G4_MAGNESIUM_OXIDE
  name = G4_MAGNESIUM_OXIDE
  specific = 4
FEATURE [App::DocumentObjectGroupPython] Mg_element008  label="Mg_element : 004"  # scripted group (container) (typed FeaturePython)
  n = 1
  ref = Mg_element
FEATURE [App::DocumentObjectGroupPython] B_element006  label="B_element : 006"  # scripted group (container) (typed FeaturePython)
  n = 4
  ref = B_element
FEATURE [App::DocumentObjectGroupPython] O_element061  label="O_element : 032"  # scripted group (container) (typed FeaturePython)
  n = 7
  ref = O_element
FEATURE [App::DocumentObjectGroupPython] G4_MAGNESIUM_TETRABORATE  # scripted group (container) (typed FeaturePython)
  Dunit = g/cm3
  Dvalue = 2.53
  Group = -> [Mg_element008,B_element006,O_element061]
  conduct = 2
  density = 1
  expand = 3
  formula = G4_MAGNESIUM_TETRABORATE
  name = G4_MAGNESIUM_TETRABORATE
  specific = 4
FEATURE [App::DocumentObjectGroupPython] Hg_element001  label="Hg_element : 1"  # scripted group (container) (typed FeaturePython)
  n = 1
  ref = Hg_element
FEATURE [App::DocumentObjectGroupPython] I_element004  label="I_element : 2"  # scripted group (container) (typed FeaturePython)
  n = 2
  ref = I_element
FEATURE [App::DocumentObjectGroupPython] G4_MERCURIC_IODIDE  # scripted group (container) (typed FeaturePython)
  Dunit = g/cm3
  Dvalue = 6.36
  Group = -> [Hg_element001,I_element004]
  conduct = 2
  density = 1
  expand = 3
  formula = G4_MERCURIC_IODIDE
  name = G4_MERCURIC_IODIDE
  specific = 4
FEATURE [App::DocumentObjectGroupPython] C_element059  label="C_element : 032"  # scripted group (container) (typed FeaturePython)
  n = 1
  ref = C_element
FEATURE [App::DocumentObjectGroupPython] H_element053  label="H_element : 028"  # scripted group (container) (typed FeaturePython)
  n = 4
  ref = H_element
FEATURE [App::DocumentObjectGroupPython] G4_METHANE  # scripted group (container) (typed FeaturePython)
  Dunit = g/cm3
  Dvalue = 0.000667151
  Group = -> [C_element059,H_element053]
  conduct = 2
  density = 1
  expand = 3
  formula = G4_METHANE
  name = G4_METHANE
  specific = 4
FEATURE [App::DocumentObjectGroupPython] C_element060  label="C_element : 033"  # scripted group (container) (typed FeaturePython)
  n = 1
  ref = C_element
FEATURE [App::DocumentObjectGroupPython] H_element054  label="H_element : 029"  # scripted group (container) (typed FeaturePython)
  n = 4
  ref = H_element
FEATURE [App::DocumentObjectGroupPython] O_element062  label="O_element : 033"  # scripted group (container) (typed FeaturePython)
  n = 1
  ref = O_element
FEATURE [App::DocumentObjectGroupPython] G4_METHANOL  # scripted group (container) (typed FeaturePython)
  Dunit = g/cm3
  Dvalue = 0.7914
  Group = -> [C_element060,H_element054,O_element062]
  conduct = 2
  density = 1
  expand = 3
  formula = G4_METHANOL
  name = G4_METHANOL
  specific = 4
FEATURE [App::DocumentObjectGroupPython] H_element055  label="H_element : 0.134"  # scripted group (container) (typed FeaturePython)
  n = 0.13404
FEATURE [App::DocumentObjectGroupPython] C_element061  label="C_element : 0.778"  # scripted group (container) (typed FeaturePython)
  n = 0.77796
FEATURE [App::DocumentObjectGroupPython] O_element063  label="O_element : 0.035"  # scripted group (container) (typed FeaturePython)
  n = 0.03502
FEATURE [App::DocumentObjectGroupPython] Mg_element009  label="Mg_element : 0.039"  # scripted group (container) (typed FeaturePython)
  n = 0.038594
FEATURE [App::DocumentObjectGroupPython] Ti_element002  label="Ti_element : 0.014"  # scripted group (container) (typed FeaturePython)
  n = 0.014386
FEATURE [App::DocumentObjectGroupPython] G4_MIX_D_WAX  # scripted group (container) (typed FeaturePython)
  Dunit = g/cm3
  Dvalue = 0.99
  Group = -> [H_element055,C_element061,O_element063,Mg_element009,Ti_element002]
  conduct = 2
  density = 1
  expand = 3
  formula = G4_MIX_D_WAX
  name = G4_MIX_D_WAX
  specific = 4
FEATURE [App::DocumentObjectGroupPython] H_element056  label="H_element : 0.135"  # scripted group (container) (typed FeaturePython)
  n = 0.081192
FEATURE [App::DocumentObjectGroupPython] C_element062  label="C_element : 0.583"  # scripted group (container) (typed FeaturePython)
  n = 0.583442
FEATURE [App::DocumentObjectGroupPython] N_element024  label="N_element : 0.018"  # scripted group (container) (typed FeaturePython)
  n = 0.017798
FEATURE [App::DocumentObjectGroupPython] O_element064  label="O_element : 0.186"  # scripted group (container) (typed FeaturePython)
  n = 0.186381
FEATURE [App::DocumentObjectGroupPython] Mg_element010  label="Mg_element : 0.130"  # scripted group (container) (typed FeaturePython)
  n = 0.130287
FEATURE [App::DocumentObjectGroupPython] Cl_element015  label="Cl_element : 0.588"  # scripted group (container) (typed FeaturePython)
  n = 0.0009
FEATURE [App::DocumentObjectGroupPython] G4_MS20_TISSUE  # scripted group (container) (typed FeaturePython)
  Dunit = g/cm3
  Dvalue = 1
  Group = -> [H_element056,C_element062,N_element024,O_element064,Mg_element010,Cl_element015]
  conduct = 2
  density = 1
  expand = 3
  formula = G4_MS20_TISSUE
  name = G4_MS20_TISSUE
  specific = 4
FEATURE [App::DocumentObjectGroupPython] H_element057  label="H_element : 0.136"  # scripted group (container) (typed FeaturePython)
  n = 0.102
FEATURE [App::DocumentObjectGroupPython] C_element063  label="C_element : 0.143"  # scripted group (container) (typed FeaturePython)
  n = 0.143
FEATURE [App::DocumentObjectGroupPython] N_element025  label="N_element : 0.034"  # scripted group (container) (typed FeaturePython)
  n = 0.034
FEATURE [App::DocumentObjectGroupPython] O_element065  label="O_element : 0.710"  # scripted group (container) (typed FeaturePython)
  n = 0.71
FEATURE [App::DocumentObjectGroupPython] Na_element011  label="Na_element : 0.098"  # scripted group (container) (typed FeaturePython)
  n = 0.001
FEATURE [App::DocumentObjectGroupPython] P_element007  label="P_element : 0.002"  # scripted group (container) (typed FeaturePython)
  n = 0.002
FEATURE [App::DocumentObjectGroupPython] S_element017  label="S_element : 0.018"  # scripted group (container) (typed FeaturePython)
  n = 0.003
FEATURE [App::DocumentObjectGroupPython] Cl_element016  label="Cl_element : 0.589"  # scripted group (container) (typed FeaturePython)
  n = 0.001
FEATURE [App::DocumentObjectGroupPython] K_element006  label="K_element : 0.004"  # scripted group (container) (typed FeaturePython)
  n = 0.004
FEATURE [App::DocumentObjectGroupPython] G4_MUSCLE_SKELETAL_ICRP  # scripted group (container) (typed FeaturePython)
  Dunit = g/cm3
  Dvalue = 1.05
  Group = -> [H_element057,C_element063,N_element025,O_element065,Na_element011,P_element007,S_element017,Cl_element016,K_element006]
  conduct = 2
  density = 1
  expand = 3
  formula = G4_MUSCLE_SKELETAL_ICRP
  name = G4_MUSCLE_SKELETAL_ICRP
  specific = 4
FEATURE [App::DocumentObjectGroupPython] H_element058  label="H_element : 0.137"  # scripted group (container) (typed FeaturePython)
  n = 0.102102
FEATURE [App::DocumentObjectGroupPython] C_element064  label="C_element : 0.123"  # scripted group (container) (typed FeaturePython)
  n = 0.123123
FEATURE [App::DocumentObjectGroupPython] N_element026  label="N_element : 0.756"  # scripted group (container) (typed FeaturePython)
  n = 0.035035
FEATURE [App::DocumentObjectGroupPython] O_element066  label="O_element : 0.730"  # scripted group (container) (typed FeaturePython)
  n = 0.72973
FEATURE [App::DocumentObjectGroupPython] Na_element012  label="Na_element : 0.099"  # scripted group (container) (typed FeaturePython)
  n = 0.001001
FEATURE [App::DocumentObjectGroupPython] P_element008  label="P_element : 0.106"  # scripted group (container) (typed FeaturePython)
  n = 0.002002
FEATURE [App::DocumentObjectGroupPython] S_element018  label="S_element : 0.019"  # scripted group (container) (typed FeaturePython)
  n = 0.004004
FEATURE [App::DocumentObjectGroupPython] K_element007  label="K_element : 0.016"  # scripted group (container) (typed FeaturePython)
  n = 0.003003
FEATURE [App::DocumentObjectGroupPython] G4_MUSCLE_STRIATED_ICRU  # scripted group (container) (typed FeaturePython)
  Dunit = g/cm3
  Dvalue = 1.04
  Group = -> [H_element058,C_element064,N_element026,O_element066,Na_element012,P_element008,S_element018,K_element007]
  conduct = 2
  density = 1
  expand = 3
  formula = G4_MUSCLE_STRIATED_ICRU
  name = G4_MUSCLE_STRIATED_ICRU
  specific = 4
FEATURE [App::DocumentObjectGroupPython] H_element059  label="H_element : 0.098"  # scripted group (container) (typed FeaturePython)
  n = 0.0982341
FEATURE [App::DocumentObjectGroupPython] C_element065  label="C_element : 0.156"  # scripted group (container) (typed FeaturePython)
  n = 0.156214
FEATURE [App::DocumentObjectGroupPython] N_element027  label="N_element : 0.757"  # scripted group (container) (typed FeaturePython)
  n = 0.035451
FEATURE [App::DocumentObjectGroupPython] O_element067  label="O_element : 0.880"  # scripted group (container) (typed FeaturePython)
  n = 0.710101
FEATURE [App::DocumentObjectGroupPython] G4_MUSCLE_WITH_SUCROSE  # scripted group (container) (typed FeaturePython)
  Dunit = g/cm3
  Dvalue = 1.11
  Group = -> [H_element059,C_element065,N_element027,O_element067]
  conduct = 2
  density = 1
  expand = 3
  formula = G4_MUSCLE_WITH_SUCROSE
  name = G4_MUSCLE_WITH_SUCROSE
  specific = 4
FEATURE [App::DocumentObjectGroupPython] H_element060  label="H_element : 0.138"  # scripted group (container) (typed FeaturePython)
  n = 0.101969
FEATURE [App::DocumentObjectGroupPython] C_element066  label="C_element : 0.120"  # scripted group (container) (typed FeaturePython)
  n = 0.120058
FEATURE [App::DocumentObjectGroupPython] N_element028  label="N_element : 0.758"  # scripted group (container) (typed FeaturePython)
  n = 0.035451
FEATURE [App::DocumentObjectGroupPython] O_element068  label="O_element : 0.743"  # scripted group (container) (typed FeaturePython)
  n = 0.742522
FEATURE [App::DocumentObjectGroupPython] G4_MUSCLE_WITHOUT_SUCROSE  # scripted group (container) (typed FeaturePython)
  Dunit = g/cm3
  Dvalue = 1.07
  Group = -> [H_element060,C_element066,N_element028,O_element068]
  conduct = 2
  density = 1
  expand = 3
  formula = G4_MUSCLE_WITHOUT_SUCROSE
  name = G4_MUSCLE_WITHOUT_SUCROSE
  specific = 4
FEATURE [App::DocumentObjectGroupPython] C_element067  label="C_element : 10"  # scripted group (container) (typed FeaturePython)
  n = 10
  ref = C_element
FEATURE [App::DocumentObjectGroupPython] H_element061  label="H_element : 030"  # scripted group (container) (typed FeaturePython)
  n = 8
  ref = H_element
FEATURE [App::DocumentObjectGroupPython] G4_NAPHTHALENE  # scripted group (container) (typed FeaturePython)
  Dunit = g/cm3
  Dvalue = 1.145
  Group = -> [C_element067,H_element061]
  conduct = 2
  density = 1
  expand = 3
  formula = G4_NAPHTHALENE
  name = G4_NAPHTHALENE
  specific = 4
FEATURE [App::DocumentObjectGroupPython] C_element068  label="C_element : 034"  # scripted group (container) (typed FeaturePython)
  n = 6
  ref = C_element
FEATURE [App::DocumentObjectGroupPython] H_element062  label="H_element : 031"  # scripted group (container) (typed FeaturePython)
  n = 5
  ref = H_element
FEATURE [App::DocumentObjectGroupPython] N_element029  label="N_element : 012"  # scripted group (container) (typed FeaturePython)
  n = 1
  ref = N_element
FEATURE [App::DocumentObjectGroupPython] O_element069  label="O_element : 034"  # scripted group (container) (typed FeaturePython)
  n = 2
  ref = O_element
FEATURE [App::DocumentObjectGroupPython] G4_NITROBENZENE  # scripted group (container) (typed FeaturePython)
  Dunit = g/cm3
  Dvalue = 1.19867
  Group = -> [C_element068,H_element062,N_element029,O_element069]
  conduct = 2
  density = 1
  expand = 3
  formula = G4_NITROBENZENE
  name = G4_NITROBENZENE
  specific = 4
FEATURE [App::DocumentObjectGroupPython] N_element030  label="N_element : 013"  # scripted group (container) (typed FeaturePython)
  n = 2
  ref = N_element
FEATURE [App::DocumentObjectGroupPython] O_element070  label="O_element : 035"  # scripted group (container) (typed FeaturePython)
  n = 1
  ref = O_element
FEATURE [App::DocumentObjectGroupPython] G4_NITROUS_OXIDE  # scripted group (container) (typed FeaturePython)
  Dunit = g/cm3
  Dvalue = 0.00183094
  Group = -> [N_element030,O_element070]
  conduct = 2
  density = 1
  expand = 3
  formula = G4_NITROUS_OXIDE
  name = G4_NITROUS_OXIDE
  specific = 4
FEATURE [App::DocumentObjectGroupPython] H_element063  label="H_element : 0.104"  # scripted group (container) (typed FeaturePython)
  n = 0.103509
FEATURE [App::DocumentObjectGroupPython] C_element069  label="C_element : 0.648"  # scripted group (container) (typed FeaturePython)
  n = 0.648416
FEATURE [App::DocumentObjectGroupPython] N_element031  label="N_element : 0.100"  # scripted group (container) (typed FeaturePython)
  n = 0.0995361
FEATURE [App::DocumentObjectGroupPython] O_element071  label="O_element : 0.149"  # scripted group (container) (typed FeaturePython)
  n = 0.148539
FEATURE [App::DocumentObjectGroupPython] G4_NYLON_8062  label="G4_NYLON-8062"  # scripted group (container) (typed FeaturePython)
  Dunit = g/cm3
  Dvalue = 1.08
  Group = -> [H_element063,C_element069,N_element031,O_element071]
  conduct = 2
  density = 1
  expand = 3
  formula = G4_NYLON-8062
  name = G4_NYLON-8062
  specific = 4
FEATURE [App::DocumentObjectGroupPython] C_element070  label="C_element : 035"  # scripted group (container) (typed FeaturePython)
  n = 6
  ref = C_element
FEATURE [App::DocumentObjectGroupPython] H_element064  label="H_element : 11"  # scripted group (container) (typed FeaturePython)
  n = 11
  ref = H_element
FEATURE [App::DocumentObjectGroupPython] N_element032  label="N_element : 014"  # scripted group (container) (typed FeaturePython)
  n = 1
  ref = N_element
FEATURE [App::DocumentObjectGroupPython] O_element072  label="O_element : 036"  # scripted group (container) (typed FeaturePython)
  n = 1
  ref = O_element
FEATURE [App::DocumentObjectGroupPython] G4_NYLON_6_6  label="G4_NYLON-6-6"  # scripted group (container) (typed FeaturePython)
  Dunit = g/cm3
  Dvalue = 1.14
  Group = -> [C_element070,H_element064,N_element032,O_element072]
  conduct = 2
  density = 1
  expand = 3
  formula = G4_NYLON-6-6
  name = G4_NYLON-6-6
  specific = 4
FEATURE [App::DocumentObjectGroupPython] H_element065  label="H_element : 0.139"  # scripted group (container) (typed FeaturePython)
  n = 0.107062
FEATURE [App::DocumentObjectGroupPython] C_element071  label="C_element : 0.680"  # scripted group (container) (typed FeaturePython)
  n = 0.680449
FEATURE [App::DocumentObjectGroupPython] N_element033  label="N_element : 0.099"  # scripted group (container) (typed FeaturePython)
  n = 0.099189
FEATURE [App::DocumentObjectGroupPython] O_element073  label="O_element : 0.113"  # scripted group (container) (typed FeaturePython)
  n = 0.1133
FEATURE [App::DocumentObjectGroupPython] G4_NYLON_6_10  label="G4_NYLON-6-10"  # scripted group (container) (typed FeaturePython)
  Dunit = g/cm3
  Dvalue = 1.14
  Group = -> [H_element065,C_element071,N_element033,O_element073]
  conduct = 2
  density = 1
  expand = 3
  formula = G4_NYLON-6-10
  name = G4_NYLON-6-10
  specific = 4
FEATURE [App::DocumentObjectGroupPython] H_element066  label="H_element : 0.140"  # scripted group (container) (typed FeaturePython)
  n = 0.115476
FEATURE [App::DocumentObjectGroupPython] C_element072  label="C_element : 0.721"  # scripted group (container) (typed FeaturePython)
  n = 0.720818
FEATURE [App::DocumentObjectGroupPython] N_element034  label="N_element : 0.076"  # scripted group (container) (typed FeaturePython)
  n = 0.0764169
FEATURE [App::DocumentObjectGroupPython] O_element074  label="O_element : 0.087"  # scripted group (container) (typed FeaturePython)
  n = 0.0872889
FEATURE [App::DocumentObjectGroupPython] G4_NYLON_11_RILSAN  label="G4_NYLON-11_RILSAN"  # scripted group (container) (typed FeaturePython)
  Dunit = g/cm3
  Dvalue = 1.425
  Group = -> [H_element066,C_element072,N_element034,O_element074]
  conduct = 2
  density = 1
  expand = 3
  formula = G4_NYLON-11_RILSAN
  name = G4_NYLON-11_RILSAN
  specific = 4
FEATURE [App::DocumentObjectGroupPython] C_element073  label="C_element : 8"  # scripted group (container) (typed FeaturePython)
  n = 8
  ref = C_element
FEATURE [App::DocumentObjectGroupPython] H_element067  label="H_element : 18"  # scripted group (container) (typed FeaturePython)
  n = 18
  ref = H_element
FEATURE [App::DocumentObjectGroupPython] G4_OCTANE  # scripted group (container) (typed FeaturePython)
  Dunit = g/cm3
  Dvalue = 0.7026
  Group = -> [C_element073,H_element067]
  conduct = 2
  density = 1
  expand = 3
  formula = G4_OCTANE
  name = G4_OCTANE
  specific = 4
FEATURE [App::DocumentObjectGroupPython] C_element074  label="C_element : 25"  # scripted group (container) (typed FeaturePython)
  n = 25
  ref = C_element
FEATURE [App::DocumentObjectGroupPython] H_element068  label="H_element : 52"  # scripted group (container) (typed FeaturePython)
  n = 52
  ref = H_element
FEATURE [App::DocumentObjectGroupPython] G4_PARAFFIN  # scripted group (container) (typed FeaturePython)
  Dunit = g/cm3
  Dvalue = 0.93
  Group = -> [C_element074,H_element068]
  conduct = 2
  density = 1
  expand = 3
  formula = G4_PARAFFIN
  name = G4_PARAFFIN
  specific = 4
FEATURE [App::DocumentObjectGroupPython] C_element075  label="C_element : 036"  # scripted group (container) (typed FeaturePython)
  n = 5
  ref = C_element
FEATURE [App::DocumentObjectGroupPython] H_element069  label="H_element : 032"  # scripted group (container) (typed FeaturePython)
  n = 12
  ref = H_element
FEATURE [App::DocumentObjectGroupPython] G4_N_PENTANE  label="G4_N-PENTANE"  # scripted group (container) (typed FeaturePython)
  Dunit = g/cm3
  Dvalue = 0.6262
  Group = -> [C_element075,H_element069]
  conduct = 2
  density = 1
  expand = 3
  formula = G4_N-PENTANE
  name = G4_N-PENTANE
  specific = 4
FEATURE [App::DocumentObjectGroupPython] H_element070  label="H_element : 0.014"  # scripted group (container) (typed FeaturePython)
  n = 0.0141
FEATURE [App::DocumentObjectGroupPython] C_element076  label="C_element : 0.072"  # scripted group (container) (typed FeaturePython)
  n = 0.072261
FEATURE [App::DocumentObjectGroupPython] N_element035  label="N_element : 0.019"  # scripted group (container) (typed FeaturePython)
  n = 0.01932
FEATURE [App::DocumentObjectGroupPython] O_element075  label="O_element : 0.066"  # scripted group (container) (typed FeaturePython)
  n = 0.066101
FEATURE [App::DocumentObjectGroupPython] S_element019  label="S_element : 0.020"  # scripted group (container) (typed FeaturePython)
  n = 0.00189
FEATURE [App::DocumentObjectGroupPython] Br_element004  label="Br_element : 0.349"  # scripted group (container) (typed FeaturePython)
  n = 0.349103
FEATURE [App::DocumentObjectGroupPython] Ag_element001  label="Ag_element : 0.474"  # scripted group (container) (typed FeaturePython)
  n = 0.474105
FEATURE [App::DocumentObjectGroupPython] I_element005  label="I_element : 0.003"  # scripted group (container) (typed FeaturePython)
  n = 0.00312
FEATURE [App::DocumentObjectGroupPython] G4_PHOTO_EMULSION  # scripted group (container) (typed FeaturePython)
  Dunit = g/cm3
  Dvalue = 3.815
  Group = -> [H_element070,C_element076,N_element035,O_element075,S_element019,Br_element004,Ag_element001,I_element005]
  conduct = 2
  density = 1
  expand = 3
  formula = G4_PHOTO_EMULSION
  name = G4_PHOTO_EMULSION
  specific = 4
FEATURE [App::DocumentObjectGroupPython] C_element077  label="C_element : 9"  # scripted group (container) (typed FeaturePython)
  n = 9
  ref = C_element
FEATURE [App::DocumentObjectGroupPython] H_element071  label="H_element : 033"  # scripted group (container) (typed FeaturePython)
  n = 10
  ref = H_element
FEATURE [App::DocumentObjectGroupPython] G4_PLASTIC_SC_VINYLTOLUENE  # scripted group (container) (typed FeaturePython)
  Dunit = g/cm3
  Dvalue = 1.032
  Group = -> [C_element077,H_element071]
  conduct = 2
  density = 1
  expand = 3
  formula = G4_PLASTIC_SC_VINYLTOLUENE
  name = G4_PLASTIC_SC_VINYLTOLUENE
  specific = 4
FEATURE [App::DocumentObjectGroupPython] Pu_element001  label="Pu_element : 1"  # scripted group (container) (typed FeaturePython)
  n = 1
  ref = Pu_element
FEATURE [App::DocumentObjectGroupPython] O_element076  label="O_element : 037"  # scripted group (container) (typed FeaturePython)
  n = 2
  ref = O_element
FEATURE [App::DocumentObjectGroupPython] G4_PLUTONIUM_DIOXIDE  # scripted group (container) (typed FeaturePython)
  Dunit = g/cm3
  Dvalue = 11.46
  Group = -> [Pu_element001,O_element076]
  conduct = 2
  density = 1
  expand = 3
  formula = G4_PLUTONIUM_DIOXIDE
  name = G4_PLUTONIUM_DIOXIDE
  specific = 4
FEATURE [App::DocumentObjectGroupPython] C_element078  label="C_element : 037"  # scripted group (container) (typed FeaturePython)
  n = 3
  ref = C_element
FEATURE [App::DocumentObjectGroupPython] H_element072  label="H_element : 034"  # scripted group (container) (typed FeaturePython)
  n = 3
  ref = H_element
FEATURE [App::DocumentObjectGroupPython] N_element036  label="N_element : 015"  # scripted group (container) (typed FeaturePython)
  n = 1
  ref = N_element
FEATURE [App::DocumentObjectGroupPython] G4_POLYACRYLONITRILE  # scripted group (container) (typed FeaturePython)
  Dunit = g/cm3
  Dvalue = 1.17
  Group = -> [C_element078,H_element072,N_element036]
  conduct = 2
  density = 1
  expand = 3
  formula = G4_POLYACRYLONITRILE
  name = G4_POLYACRYLONITRILE
  specific = 4
FEATURE [App::DocumentObjectGroupPython] C_element079  label="C_element : 16"  # scripted group (container) (typed FeaturePython)
  n = 16
  ref = C_element
FEATURE [App::DocumentObjectGroupPython] H_element073  label="H_element : 035"  # scripted group (container) (typed FeaturePython)
  n = 14
  ref = H_element
FEATURE [App::DocumentObjectGroupPython] O_element077  label="O_element : 038"  # scripted group (container) (typed FeaturePython)
  n = 3
  ref = O_element
FEATURE [App::DocumentObjectGroupPython] G4_POLYCARBONATE  # scripted group (container) (typed FeaturePython)
  Dunit = g/cm3
  Dvalue = 1.2
  Group = -> [C_element079,H_element073,O_element077]
  conduct = 2
  density = 1
  expand = 3
  formula = G4_POLYCARBONATE
  name = G4_POLYCARBONATE
  specific = 4
FEATURE [App::DocumentObjectGroupPython] C_element080  label="C_element : 038"  # scripted group (container) (typed FeaturePython)
  n = 8
  ref = C_element
FEATURE [App::DocumentObjectGroupPython] H_element074  label="H_element : 036"  # scripted group (container) (typed FeaturePython)
  n = 7
  ref = H_element
FEATURE [App::DocumentObjectGroupPython] Cl_element017  label="Cl_element : 007"  # scripted group (container) (typed FeaturePython)
  n = 1
  ref = Cl_element
FEATURE [App::DocumentObjectGroupPython] G4_POLYCHLOROSTYRENE  # scripted group (container) (typed FeaturePython)
  Dunit = g/cm3
  Dvalue = 1.3
  Group = -> [C_element080,H_element074,Cl_element017]
  conduct = 2
  density = 1
  expand = 3
  formula = G4_POLYCHLOROSTYRENE
  name = G4_POLYCHLOROSTYRENE
  specific = 4
FEATURE [App::DocumentObjectGroupPython] C_element081  label="C_element : 039"  # scripted group (container) (typed FeaturePython)
  n = 1
  ref = C_element
FEATURE [App::DocumentObjectGroupPython] H_element075  label="H_element : 037"  # scripted group (container) (typed FeaturePython)
  n = 2
  ref = H_element
FEATURE [App::DocumentObjectGroupPython] G4_POLYETHYLENE  # scripted group (container) (typed FeaturePython)
  Dunit = g/cm3
  Dvalue = 0.94
  Group = -> [C_element081,H_element075]
  conduct = 2
  density = 1
  expand = 3
  formula = G4_POLYETHYLENE
  name = G4_POLYETHYLENE
  specific = 4
FEATURE [App::DocumentObjectGroupPython] C_element082  label="C_element : 040"  # scripted group (container) (typed FeaturePython)
  n = 10
  ref = C_element
FEATURE [App::DocumentObjectGroupPython] H_element076  label="H_element : 038"  # scripted group (container) (typed FeaturePython)
  n = 8
  ref = H_element
FEATURE [App::DocumentObjectGroupPython] O_element078  label="O_element : 039"  # scripted group (container) (typed FeaturePython)
  n = 4
  ref = O_element
FEATURE [App::DocumentObjectGroupPython] G4_MYLAR  # scripted group (container) (typed FeaturePython)
  Dunit = g/cm3
  Dvalue = 1.4
  Group = -> [C_element082,H_element076,O_element078]
  conduct = 2
  density = 1
  expand = 3
  formula = G4_MYLAR
  name = G4_MYLAR
  specific = 4
FEATURE [App::DocumentObjectGroupPython] C_element083  label="C_element : 041"  # scripted group (container) (typed FeaturePython)
  n = 5
  ref = C_element
FEATURE [App::DocumentObjectGroupPython] H_element077  label="H_element : 039"  # scripted group (container) (typed FeaturePython)
  n = 8
  ref = H_element
FEATURE [App::DocumentObjectGroupPython] O_element079  label="O_element : 040"  # scripted group (container) (typed FeaturePython)
  n = 2
  ref = O_element
FEATURE [App::DocumentObjectGroupPython] G4_PLEXIGLASS  # scripted group (container) (typed FeaturePython)
  Dunit = g/cm3
  Dvalue = 1.19
  Group = -> [C_element083,H_element077,O_element079]
  conduct = 2
  density = 1
  expand = 3
  formula = G4_PLEXIGLASS
  name = G4_PLEXIGLASS
  specific = 4
FEATURE [App::DocumentObjectGroupPython] C_element084  label="C_element : 042"  # scripted group (container) (typed FeaturePython)
  n = 1
  ref = C_element
FEATURE [App::DocumentObjectGroupPython] H_element078  label="H_element : 040"  # scripted group (container) (typed FeaturePython)
  n = 2
  ref = H_element
FEATURE [App::DocumentObjectGroupPython] O_element080  label="O_element : 041"  # scripted group (container) (typed FeaturePython)
  n = 1
  ref = O_element
FEATURE [App::DocumentObjectGroupPython] G4_POLYOXYMETHYLENE  # scripted group (container) (typed FeaturePython)
  Dunit = g/cm3
  Dvalue = 1.425
  Group = -> [C_element084,H_element078,O_element080]
  conduct = 2
  density = 1
  expand = 3
  formula = G4_POLYOXYMETHYLENE
  name = G4_POLYOXYMETHYLENE
  specific = 4
FEATURE [App::DocumentObjectGroupPython] C_element085  label="C_element : 043"  # scripted group (container) (typed FeaturePython)
  n = 2
  ref = C_element
FEATURE [App::DocumentObjectGroupPython] H_element079  label="H_element : 041"  # scripted group (container) (typed FeaturePython)
  n = 4
  ref = H_element
FEATURE [App::DocumentObjectGroupPython] G4_POLYPROPYLENE  # scripted group (container) (typed FeaturePython)
  Dunit = g/cm3
  Dvalue = 0.9
  Group = -> [C_element085,H_element079]
  conduct = 2
  density = 1
  expand = 3
  formula = G4_POLYPROPYLENE
  name = G4_POLYPROPYLENE
  specific = 4
FEATURE [App::DocumentObjectGroupPython] C_element086  label="C_element : 044"  # scripted group (container) (typed FeaturePython)
  n = 8
  ref = C_element
FEATURE [App::DocumentObjectGroupPython] H_element080  label="H_element : 042"  # scripted group (container) (typed FeaturePython)
  n = 8
  ref = H_element
FEATURE [App::DocumentObjectGroupPython] G4_POLYSTYRENE  # scripted group (container) (typed FeaturePython)
  Dunit = g/cm3
  Dvalue = 1.06
  Group = -> [C_element086,H_element080]
  conduct = 2
  density = 1
  expand = 3
  formula = G4_POLYSTYRENE
  name = G4_POLYSTYRENE
  specific = 4
FEATURE [App::DocumentObjectGroupPython] C_element087  label="C_element : 045"  # scripted group (container) (typed FeaturePython)
  n = 2
  ref = C_element
FEATURE [App::DocumentObjectGroupPython] F_element014  label="F_element : 4"  # scripted group (container) (typed FeaturePython)
  n = 4
  ref = F_element
FEATURE [App::DocumentObjectGroupPython] G4_TEFLON  # scripted group (container) (typed FeaturePython)
  Dunit = g/cm3
  Dvalue = 2.2
  Group = -> [C_element087,F_element014]
  conduct = 2
  density = 1
  expand = 3
  formula = G4_TEFLON
  name = G4_TEFLON
  specific = 4
FEATURE [App::DocumentObjectGroupPython] C_element088  label="C_element : 046"  # scripted group (container) (typed FeaturePython)
  n = 2
  ref = C_element
FEATURE [App::DocumentObjectGroupPython] F_element015  label="F_element : 006"  # scripted group (container) (typed FeaturePython)
  n = 3
  ref = F_element
FEATURE [App::DocumentObjectGroupPython] Cl_element018  label="Cl_element : 008"  # scripted group (container) (typed FeaturePython)
  n = 1
  ref = Cl_element
FEATURE [App::DocumentObjectGroupPython] G4_POLYTRIFLUOROCHLOROETHYLENE  # scripted group (container) (typed FeaturePython)
  Dunit = g/cm3
  Dvalue = 2.1
  Group = -> [C_element088,F_element015,Cl_element018]
  conduct = 2
  density = 1
  expand = 3
  formula = G4_POLYTRIFLUOROCHLOROETHYLENE
  name = G4_POLYTRIFLUOROCHLOROETHYLENE
  specific = 4
FEATURE [App::DocumentObjectGroupPython] C_element089  label="C_element : 047"  # scripted group (container) (typed FeaturePython)
  n = 4
  ref = C_element
FEATURE [App::DocumentObjectGroupPython] H_element081  label="H_element : 043"  # scripted group (container) (typed FeaturePython)
  n = 6
  ref = H_element
FEATURE [App::DocumentObjectGroupPython] O_element081  label="O_element : 042"  # scripted group (container) (typed FeaturePython)
  n = 2
  ref = O_element
FEATURE [App::DocumentObjectGroupPython] G4_POLYVINYL_ACETATE  # scripted group (container) (typed FeaturePython)
  Dunit = g/cm3
  Dvalue = 1.19
  Group = -> [C_element089,H_element081,O_element081]
  conduct = 2
  density = 1
  expand = 3
  formula = G4_POLYVINYL_ACETATE
  name = G4_POLYVINYL_ACETATE
  specific = 4
FEATURE [App::DocumentObjectGroupPython] C_element090  label="C_element : 048"  # scripted group (container) (typed FeaturePython)
  n = 2
  ref = C_element
FEATURE [App::DocumentObjectGroupPython] H_element082  label="H_element : 044"  # scripted group (container) (typed FeaturePython)
  n = 4
  ref = H_element
FEATURE [App::DocumentObjectGroupPython] O_element082  label="O_element : 043"  # scripted group (container) (typed FeaturePython)
  n = 1
  ref = O_element
FEATURE [App::DocumentObjectGroupPython] G4_POLYVINYL_ALCOHOL  # scripted group (container) (typed FeaturePython)
  Dunit = g/cm3
  Dvalue = 1.3
  Group = -> [C_element090,H_element082,O_element082]
  conduct = 2
  density = 1
  expand = 3
  formula = G4_POLYVINYL_ALCOHOL
  name = G4_POLYVINYL_ALCOHOL
  specific = 4
FEATURE [App::DocumentObjectGroupPython] C_element091  label="C_element : 049"  # scripted group (container) (typed FeaturePython)
  n = 8
  ref = C_element
FEATURE [App::DocumentObjectGroupPython] H_element083  label="H_element : 045"  # scripted group (container) (typed FeaturePython)
  n = 14
  ref = H_element
FEATURE [App::DocumentObjectGroupPython] O_element083  label="O_element : 044"  # scripted group (container) (typed FeaturePython)
  n = 2
  ref = O_element
FEATURE [App::DocumentObjectGroupPython] G4_POLYVINYL_BUTYRAL  # scripted group (container) (typed FeaturePython)
  Dunit = g/cm3
  Dvalue = 1.12
  Group = -> [C_element091,H_element083,O_element083]
  conduct = 2
  density = 1
  expand = 3
  formula = G4_POLYVINYL_BUTYRAL
  name = G4_POLYVINYL_BUTYRAL
  specific = 4
FEATURE [App::DocumentObjectGroupPython] C_element092  label="C_element : 050"  # scripted group (container) (typed FeaturePython)
  n = 2
  ref = C_element
FEATURE [App::DocumentObjectGroupPython] H_element084  label="H_element : 046"  # scripted group (container) (typed FeaturePython)
  n = 3
  ref = H_element
FEATURE [App::DocumentObjectGroupPython] Cl_element019  label="Cl_element : 009"  # scripted group (container) (typed FeaturePython)
  n = 1
  ref = Cl_element
FEATURE [App::DocumentObjectGroupPython] G4_POLYVINYL_CHLORIDE  # scripted group (container) (typed FeaturePython)
  Dunit = g/cm3
  Dvalue = 1.3
  Group = -> [C_element092,H_element084,Cl_element019]
  conduct = 2
  density = 1
  expand = 3
  formula = G4_POLYVINYL_CHLORIDE
  name = G4_POLYVINYL_CHLORIDE
  specific = 4
FEATURE [App::DocumentObjectGroupPython] C_element093  label="C_element : 051"  # scripted group (container) (typed FeaturePython)
  n = 2
  ref = C_element
FEATURE [App::DocumentObjectGroupPython] H_element085  label="H_element : 047"  # scripted group (container) (typed FeaturePython)
  n = 2
  ref = H_element
FEATURE [App::DocumentObjectGroupPython] Cl_element020  label="Cl_element : 010"  # scripted group (container) (typed FeaturePython)
  n = 2
  ref = Cl_element
FEATURE [App::DocumentObjectGroupPython] G4_POLYVINYLIDENE_CHLORIDE  # scripted group (container) (typed FeaturePython)
  Dunit = g/cm3
  Dvalue = 1.7
  Group = -> [C_element093,H_element085,Cl_element020]
  conduct = 2
  density = 1
  expand = 3
  formula = G4_POLYVINYLIDENE_CHLORIDE
  name = G4_POLYVINYLIDENE_CHLORIDE
  specific = 4
FEATURE [App::DocumentObjectGroupPython] C_element094  label="C_element : 052"  # scripted group (container) (typed FeaturePython)
  n = 2
  ref = C_element
FEATURE [App::DocumentObjectGroupPython] H_element086  label="H_element : 048"  # scripted group (container) (typed FeaturePython)
  n = 2
  ref = H_element
FEATURE [App::DocumentObjectGroupPython] F_element016  label="F_element : 007"  # scripted group (container) (typed FeaturePython)
  n = 2
  ref = F_element
FEATURE [App::DocumentObjectGroupPython] G4_POLYVINYLIDENE_FLUORIDE  # scripted group (container) (typed FeaturePython)
  Dunit = g/cm3
  Dvalue = 1.76
  Group = -> [C_element094,H_element086,F_element016]
  conduct = 2
  density = 1
  expand = 3
  formula = G4_POLYVINYLIDENE_FLUORIDE
  name = G4_POLYVINYLIDENE_FLUORIDE
  specific = 4
FEATURE [App::DocumentObjectGroupPython] C_element095  label="C_element : 053"  # scripted group (container) (typed FeaturePython)
  n = 6
  ref = C_element
FEATURE [App::DocumentObjectGroupPython] H_element087  label="H_element : 9"  # scripted group (container) (typed FeaturePython)
  n = 9
  ref = H_element
FEATURE [App::DocumentObjectGroupPython] N_element037  label="N_element : 016"  # scripted group (container) (typed FeaturePython)
  n = 1
  ref = N_element
FEATURE [App::DocumentObjectGroupPython] O_element084  label="O_element : 045"  # scripted group (container) (typed FeaturePython)
  n = 1
  ref = O_element
FEATURE [App::DocumentObjectGroupPython] G4_POLYVINYL_PYRROLIDONE  # scripted group (container) (typed FeaturePython)
  Dunit = g/cm3
  Dvalue = 1.25
  Group = -> [C_element095,H_element087,N_element037,O_element084]
  conduct = 2
  density = 1
  expand = 3
  formula = G4_POLYVINYL_PYRROLIDONE
  name = G4_POLYVINYL_PYRROLIDONE
  specific = 4
FEATURE [App::DocumentObjectGroupPython] K_element008  label="K_element : 1"  # scripted group (container) (typed FeaturePython)
  n = 1
  ref = K_element
FEATURE [App::DocumentObjectGroupPython] I_element006  label="I_element : 003"  # scripted group (container) (typed FeaturePython)
  n = 1
  ref = I_element
FEATURE [App::DocumentObjectGroupPython] G4_POTASSIUM_IODIDE  # scripted group (container) (typed FeaturePython)
  Dunit = g/cm3
  Dvalue = 3.13
  Group = -> [K_element008,I_element006]
  conduct = 2
  density = 1
  expand = 3
  formula = G4_POTASSIUM_IODIDE
  name = G4_POTASSIUM_IODIDE
  specific = 4
FEATURE [App::DocumentObjectGroupPython] K_element009  label="K_element : 2"  # scripted group (container) (typed FeaturePython)
  n = 2
  ref = K_element
FEATURE [App::DocumentObjectGroupPython] O_element085  label="O_element : 046"  # scripted group (container) (typed FeaturePython)
  n = 1
  ref = O_element
FEATURE [App::DocumentObjectGroupPython] G4_POTASSIUM_OXIDE  # scripted group (container) (typed FeaturePython)
  Dunit = g/cm3
  Dvalue = 2.32
  Group = -> [K_element009,O_element085]
  conduct = 2
  density = 1
  expand = 3
  formula = G4_POTASSIUM_OXIDE
  name = G4_POTASSIUM_OXIDE
  specific = 4
FEATURE [App::DocumentObjectGroupPython] C_element096  label="C_element : 054"  # scripted group (container) (typed FeaturePython)
  n = 3
  ref = C_element
FEATURE [App::DocumentObjectGroupPython] H_element088  label="H_element : 049"  # scripted group (container) (typed FeaturePython)
  n = 8
  ref = H_element
FEATURE [App::DocumentObjectGroupPython] G4_PROPANE  # scripted group (container) (typed FeaturePython)
  Dunit = g/cm3
  Dvalue = 0.00187939
  Group = -> [C_element096,H_element088]
  conduct = 2
  density = 1
  expand = 3
  formula = G4_PROPANE
  name = G4_PROPANE
  specific = 4
FEATURE [App::DocumentObjectGroupPython] C_element097  label="C_element : 055"  # scripted group (container) (typed FeaturePython)
  n = 3
  ref = C_element
FEATURE [App::DocumentObjectGroupPython] H_element089  label="H_element : 050"  # scripted group (container) (typed FeaturePython)
  n = 8
  ref = H_element
FEATURE [App::DocumentObjectGroupPython] G4_lPROPANE  # scripted group (container) (typed FeaturePython)
  Dunit = g/cm3
  Dvalue = 0.43
  Group = -> [C_element097,H_element089]
  conduct = 2
  density = 1
  expand = 3
  formula = G4_lPROPANE
  name = G4_lPROPANE
  specific = 4
FEATURE [App::DocumentObjectGroupPython] C_element098  label="C_element : 056"  # scripted group (container) (typed FeaturePython)
  n = 3
  ref = C_element
FEATURE [App::DocumentObjectGroupPython] H_element090  label="H_element : 051"  # scripted group (container) (typed FeaturePython)
  n = 8
  ref = H_element
FEATURE [App::DocumentObjectGroupPython] O_element086  label="O_element : 047"  # scripted group (container) (typed FeaturePython)
  n = 1
  ref = O_element
FEATURE [App::DocumentObjectGroupPython] G4_N_PROPYL_ALCOHOL  label="G4_N-PROPYL_ALCOHOL"  # scripted group (container) (typed FeaturePython)
  Dunit = g/cm3
  Dvalue = 0.8035
  Group = -> [C_element098,H_element090,O_element086]
  conduct = 2
  density = 1
  expand = 3
  formula = G4_N-PROPYL_ALCOHOL
  name = G4_N-PROPYL_ALCOHOL
  specific = 4
FEATURE [App::DocumentObjectGroupPython] C_element099  label="C_element : 057"  # scripted group (container) (typed FeaturePython)
  n = 5
  ref = C_element
FEATURE [App::DocumentObjectGroupPython] H_element091  label="H_element : 052"  # scripted group (container) (typed FeaturePython)
  n = 5
  ref = H_element
FEATURE [App::DocumentObjectGroupPython] N_element038  label="N_element : 017"  # scripted group (container) (typed FeaturePython)
  n = 1
  ref = N_element
FEATURE [App::DocumentObjectGroupPython] G4_PYRIDINE  # scripted group (container) (typed FeaturePython)
  Dunit = g/cm3
  Dvalue = 0.9819
  Group = -> [C_element099,H_element091,N_element038]
  conduct = 2
  density = 1
  expand = 3
  formula = G4_PYRIDINE
  name = G4_PYRIDINE
  specific = 4
FEATURE [App::DocumentObjectGroupPython] H_element092  label="H_element : 0.144"  # scripted group (container) (typed FeaturePython)
  n = 0.143711
FEATURE [App::DocumentObjectGroupPython] C_element100  label="C_element : 0.856"  # scripted group (container) (typed FeaturePython)
  n = 0.856289
FEATURE [App::DocumentObjectGroupPython] G4_RUBBER_BUTYL  # scripted group (container) (typed FeaturePython)
  Dunit = g/cm3
  Dvalue = 0.92
  Group = -> [H_element092,C_element100]
  conduct = 2
  density = 1
  expand = 3
  formula = G4_RUBBER_BUTYL
  name = G4_RUBBER_BUTYL
  specific = 4
FEATURE [App::DocumentObjectGroupPython] H_element093  label="H_element : 0.118"  # scripted group (container) (typed FeaturePython)
  n = 0.118371
FEATURE [App::DocumentObjectGroupPython] C_element101  label="C_element : 0.882"  # scripted group (container) (typed FeaturePython)
  n = 0.881629
FEATURE [App::DocumentObjectGroupPython] G4_RUBBER_NATURAL  # scripted group (container) (typed FeaturePython)
  Dunit = g/cm3
  Dvalue = 0.92
  Group = -> [H_element093,C_element101]
  conduct = 2
  density = 1
  expand = 3
  formula = G4_RUBBER_NATURAL
  name = G4_RUBBER_NATURAL
  specific = 4
FEATURE [App::DocumentObjectGroupPython] H_element094  label="H_element : 0.145"  # scripted group (container) (typed FeaturePython)
  n = 0.05692
FEATURE [App::DocumentObjectGroupPython] C_element102  label="C_element : 0.543"  # scripted group (container) (typed FeaturePython)
  n = 0.542646
FEATURE [App::DocumentObjectGroupPython] Cl_element021  label="Cl_element : 0.400"  # scripted group (container) (typed FeaturePython)
  n = 0.400434
FEATURE [App::DocumentObjectGroupPython] G4_RUBBER_NEOPRENE  # scripted group (container) (typed FeaturePython)
  Dunit = g/cm3
  Dvalue = 1.23
  Group = -> [H_element094,C_element102,Cl_element021]
  conduct = 2
  density = 1
  expand = 3
  formula = G4_RUBBER_NEOPRENE
  name = G4_RUBBER_NEOPRENE
  specific = 4
FEATURE [App::DocumentObjectGroupPython] Si_element006  label="Si_element : 1"  # scripted group (container) (typed FeaturePython)
  n = 1
  ref = Si_element
FEATURE [App::DocumentObjectGroupPython] O_element087  label="O_element : 048"  # scripted group (container) (typed FeaturePython)
  n = 2
  ref = O_element
FEATURE [App::DocumentObjectGroupPython] G4_SILICON_DIOXIDE  # scripted group (container) (typed FeaturePython)
  Dunit = g/cm3
  Dvalue = 2.32
  Group = -> [Si_element006,O_element087]
  conduct = 2
  density = 1
  expand = 3
  formula = G4_SILICON_DIOXIDE
  name = G4_SILICON_DIOXIDE
  specific = 4
FEATURE [App::DocumentObjectGroupPython] Ag_element002  label="Ag_element : 1"  # scripted group (container) (typed FeaturePython)
  n = 1
  ref = Ag_element
FEATURE [App::DocumentObjectGroupPython] Br_element005  label="Br_element : 003"  # scripted group (container) (typed FeaturePython)
  n = 1
  ref = Br_element
FEATURE [App::DocumentObjectGroupPython] G4_SILVER_BROMIDE  # scripted group (container) (typed FeaturePython)
  Dunit = g/cm3
  Dvalue = 6.473
  Group = -> [Ag_element002,Br_element005]
  conduct = 2
  density = 1
  expand = 3
  formula = G4_SILVER_BROMIDE
  name = G4_SILVER_BROMIDE
  specific = 4
FEATURE [App::DocumentObjectGroupPython] Ag_element003  label="Ag_element : 002"  # scripted group (container) (typed FeaturePython)
  n = 1
  ref = Ag_element
FEATURE [App::DocumentObjectGroupPython] Cl_element022  label="Cl_element : 011"  # scripted group (container) (typed FeaturePython)
  n = 1
  ref = Cl_element
FEATURE [App::DocumentObjectGroupPython] G4_SILVER_CHLORIDE  # scripted group (container) (typed FeaturePython)
  Dunit = g/cm3
  Dvalue = 5.56
  Group = -> [Ag_element003,Cl_element022]
  conduct = 2
  density = 1
  expand = 3
  formula = G4_SILVER_CHLORIDE
  name = G4_SILVER_CHLORIDE
  specific = 4
FEATURE [App::DocumentObjectGroupPython] Br_element006  label="Br_element : 0.423"  # scripted group (container) (typed FeaturePython)
  n = 0.422895
FEATURE [App::DocumentObjectGroupPython] Ag_element004  label="Ag_element : 0.574"  # scripted group (container) (typed FeaturePython)
  n = 0.573748
FEATURE [App::DocumentObjectGroupPython] I_element007  label="I_element : 0.649"  # scripted group (container) (typed FeaturePython)
  n = 0.003357
FEATURE [App::DocumentObjectGroupPython] G4_SILVER_HALIDES  # scripted group (container) (typed FeaturePython)
  Dunit = g/cm3
  Dvalue = 6.47
  Group = -> [Br_element006,Ag_element004,I_element007]
  conduct = 2
  density = 1
  expand = 3
  formula = G4_SILVER_HALIDES
  name = G4_SILVER_HALIDES
  specific = 4
FEATURE [App::DocumentObjectGroupPython] Ag_element005  label="Ag_element : 003"  # scripted group (container) (typed FeaturePython)
  n = 1
  ref = Ag_element
FEATURE [App::DocumentObjectGroupPython] I_element008  label="I_element : 004"  # scripted group (container) (typed FeaturePython)
  n = 1
  ref = I_element
FEATURE [App::DocumentObjectGroupPython] G4_SILVER_IODIDE  # scripted group (container) (typed FeaturePython)
  Dunit = g/cm3
  Dvalue = 6.01
  Group = -> [Ag_element005,I_element008]
  conduct = 2
  density = 1
  expand = 3
  formula = G4_SILVER_IODIDE
  name = G4_SILVER_IODIDE
  specific = 4
FEATURE [App::DocumentObjectGroupPython] H_element095  label="H_element : 0.100"  # scripted group (container) (typed FeaturePython)
  n = 0.1
FEATURE [App::DocumentObjectGroupPython] C_element103  label="C_element : 0.204"  # scripted group (container) (typed FeaturePython)
  n = 0.204
FEATURE [App::DocumentObjectGroupPython] N_element039  label="N_element : 0.759"  # scripted group (container) (typed FeaturePython)
  n = 0.042
FEATURE [App::DocumentObjectGroupPython] O_element088  label="O_element : 0.645"  # scripted group (container) (typed FeaturePython)
  n = 0.645
FEATURE [App::DocumentObjectGroupPython] Na_element013  label="Na_element : 0.100"  # scripted group (container) (typed FeaturePython)
  n = 0.002
FEATURE [App::DocumentObjectGroupPython] P_element009  label="P_element : 0.107"  # scripted group (container) (typed FeaturePython)
  n = 0.001
FEATURE [App::DocumentObjectGroupPython] S_element020  label="S_element : 0.021"  # scripted group (container) (typed FeaturePython)
  n = 0.002
FEATURE [App::DocumentObjectGroupPython] Cl_element023  label="Cl_element : 0.590"  # scripted group (container) (typed FeaturePython)
  n = 0.003
FEATURE [App::DocumentObjectGroupPython] K_element010  label="K_element : 0.001"  # scripted group (container) (typed FeaturePython)
  n = 0.001
FEATURE [App::DocumentObjectGroupPython] G4_SKIN_ICRP  # scripted group (container) (typed FeaturePython)
  Dunit = g/cm3
  Dvalue = 1.09
  Group = -> [H_element095,C_element103,N_element039,O_element088,Na_element013,P_element009,S_element020,Cl_element023,K_element010]
  conduct = 2
  density = 1
  expand = 3
  formula = G4_SKIN_ICRP
  name = G4_SKIN_ICRP
  specific = 4
FEATURE [App::DocumentObjectGroupPython] Na_element014  label="Na_element : 2"  # scripted group (container) (typed FeaturePython)
  n = 2
  ref = Na_element
FEATURE [App::DocumentObjectGroupPython] C_element104  label="C_element : 058"  # scripted group (container) (typed FeaturePython)
  n = 1
  ref = C_element
FEATURE [App::DocumentObjectGroupPython] O_element089  label="O_element : 049"  # scripted group (container) (typed FeaturePython)
  n = 3
  ref = O_element
FEATURE [App::DocumentObjectGroupPython] G4_SODIUM_CARBONATE  # scripted group (container) (typed FeaturePython)
  Dunit = g/cm3
  Dvalue = 2.532
  Group = -> [Na_element014,C_element104,O_element089]
  conduct = 2
  density = 1
  expand = 3
  formula = G4_SODIUM_CARBONATE
  name = G4_SODIUM_CARBONATE
  specific = 4
FEATURE [App::DocumentObjectGroupPython] Na_element015  label="Na_element : 1"  # scripted group (container) (typed FeaturePython)
  n = 1
  ref = Na_element
FEATURE [App::DocumentObjectGroupPython] I_element009  label="I_element : 005"  # scripted group (container) (typed FeaturePython)
  n = 1
  ref = I_element
FEATURE [App::DocumentObjectGroupPython] G4_SODIUM_IODIDE  # scripted group (container) (typed FeaturePython)
  Dunit = g/cm3
  Dvalue = 3.667
  Group = -> [Na_element015,I_element009]
  conduct = 2
  density = 1
  expand = 3
  formula = G4_SODIUM_IODIDE
  name = G4_SODIUM_IODIDE
  specific = 4
FEATURE [App::DocumentObjectGroupPython] Na_element016  label="Na_element : 003"  # scripted group (container) (typed FeaturePython)
  n = 2
  ref = Na_element
FEATURE [App::DocumentObjectGroupPython] O_element090  label="O_element : 050"  # scripted group (container) (typed FeaturePython)
  n = 1
  ref = O_element
FEATURE [App::DocumentObjectGroupPython] G4_SODIUM_MONOXIDE  # scripted group (container) (typed FeaturePython)
  Dunit = g/cm3
  Dvalue = 2.27
  Group = -> [Na_element016,O_element090]
  conduct = 2
  density = 1
  expand = 3
  formula = G4_SODIUM_MONOXIDE
  name = G4_SODIUM_MONOXIDE
  specific = 4
FEATURE [App::DocumentObjectGroupPython] Na_element017  label="Na_element : 004"  # scripted group (container) (typed FeaturePython)
  n = 1
  ref = Na_element
FEATURE [App::DocumentObjectGroupPython] N_element040  label="N_element : 018"  # scripted group (container) (typed FeaturePython)
  n = 1
  ref = N_element
FEATURE [App::DocumentObjectGroupPython] O_element091  label="O_element : 051"  # scripted group (container) (typed FeaturePython)
  n = 3
  ref = O_element
FEATURE [App::DocumentObjectGroupPython] G4_SODIUM_NITRATE  # scripted group (container) (typed FeaturePython)
  Dunit = g/cm3
  Dvalue = 2.261
  Group = -> [Na_element017,N_element040,O_element091]
  conduct = 2
  density = 1
  expand = 3
  formula = G4_SODIUM_NITRATE
  name = G4_SODIUM_NITRATE
  specific = 4
FEATURE [App::DocumentObjectGroupPython] C_element105  label="C_element : 059"  # scripted group (container) (typed FeaturePython)
  n = 14
  ref = C_element
FEATURE [App::DocumentObjectGroupPython] H_element096  label="H_element : 053"  # scripted group (container) (typed FeaturePython)
  n = 12
  ref = H_element
FEATURE [App::DocumentObjectGroupPython] G4_STILBENE  # scripted group (container) (typed FeaturePython)
  Dunit = g/cm3
  Dvalue = 0.9707
  Group = -> [C_element105,H_element096]
  conduct = 2
  density = 1
  expand = 3
  formula = G4_STILBENE
  name = G4_STILBENE
  specific = 4
FEATURE [App::DocumentObjectGroupPython] C_element106  label="C_element : 12"  # scripted group (container) (typed FeaturePython)
  n = 12
  ref = C_element
FEATURE [App::DocumentObjectGroupPython] H_element097  label="H_element : 22"  # scripted group (container) (typed FeaturePython)
  n = 22
  ref = H_element
FEATURE [App::DocumentObjectGroupPython] O_element092  label="O_element : 11"  # scripted group (container) (typed FeaturePython)
  n = 11
  ref = O_element
FEATURE [App::DocumentObjectGroupPython] G4_SUCROSE  # scripted group (container) (typed FeaturePython)
  Dunit = g/cm3
  Dvalue = 1.5805
  Group = -> [C_element106,H_element097,O_element092]
  conduct = 2
  density = 1
  expand = 3
  formula = G4_SUCROSE
  name = G4_SUCROSE
  specific = 4
FEATURE [App::DocumentObjectGroupPython] C_element107  label="C_element : 18"  # scripted group (container) (typed FeaturePython)
  n = 18
  ref = C_element
FEATURE [App::DocumentObjectGroupPython] H_element098  label="H_element : 054"  # scripted group (container) (typed FeaturePython)
  n = 14
  ref = H_element
FEATURE [App::DocumentObjectGroupPython] G4_TERPHENYL  # scripted group (container) (typed FeaturePython)
  Dunit = g/cm3
  Dvalue = 1.24
  Group = -> [C_element107,H_element098]
  conduct = 2
  density = 1
  expand = 3
  formula = G4_TERPHENYL
  name = G4_TERPHENYL
  specific = 4
FEATURE [App::DocumentObjectGroupPython] H_element099  label="H_element : 0.146"  # scripted group (container) (typed FeaturePython)
  n = 0.106
FEATURE [App::DocumentObjectGroupPython] C_element108  label="C_element : 0.883"  # scripted group (container) (typed FeaturePython)
  n = 0.099
FEATURE [App::DocumentObjectGroupPython] N_element041  label="N_element : 0.020"  # scripted group (container) (typed FeaturePython)
  n = 0.02
FEATURE [App::DocumentObjectGroupPython] O_element093  label="O_element : 0.766"  # scripted group (container) (typed FeaturePython)
  n = 0.766
FEATURE [App::DocumentObjectGroupPython] Na_element018  label="Na_element : 0.101"  # scripted group (container) (typed FeaturePython)
  n = 0.002
FEATURE [App::DocumentObjectGroupPython] P_element010  label="P_element : 0.108"  # scripted group (container) (typed FeaturePython)
  n = 0.001
FEATURE [App::DocumentObjectGroupPython] S_element021  label="S_element : 0.022"  # scripted group (container) (typed FeaturePython)
  n = 0.002
FEATURE [App::DocumentObjectGroupPython] Cl_element024  label="Cl_element : 0.002"  # scripted group (container) (typed FeaturePython)
  n = 0.002
FEATURE [App::DocumentObjectGroupPython] K_element011  label="K_element : 0.017"  # scripted group (container) (typed FeaturePython)
  n = 0.002
FEATURE [App::DocumentObjectGroupPython] G4_TESTIS_ICRP  # scripted group (container) (typed FeaturePython)
  Dunit = g/cm3
  Dvalue = 1.04
  Group = -> [H_element099,C_element108,N_element041,O_element093,Na_element018,P_element010,S_element021,Cl_element024,K_element011]
  conduct = 2
  density = 1
  expand = 3
  formula = G4_TESTIS_ICRP
  name = G4_TESTIS_ICRP
  specific = 4
FEATURE [App::DocumentObjectGroupPython] C_element109  label="C_element : 060"  # scripted group (container) (typed FeaturePython)
  n = 2
  ref = C_element
FEATURE [App::DocumentObjectGroupPython] Cl_element025  label="Cl_element : 012"  # scripted group (container) (typed FeaturePython)
  n = 4
  ref = Cl_element
FEATURE [App::DocumentObjectGroupPython] G4_TETRACHLOROETHYLENE  # scripted group (container) (typed FeaturePython)
  Dunit = g/cm3
  Dvalue = 1.625
  Group = -> [C_element109,Cl_element025]
  conduct = 2
  density = 1
  expand = 3
  formula = G4_TETRACHLOROETHYLENE
  name = G4_TETRACHLOROETHYLENE
  specific = 4
FEATURE [App::DocumentObjectGroupPython] Tl_element001  label="Tl_element : 1"  # scripted group (container) (typed FeaturePython)
  n = 1
  ref = Tl_element
FEATURE [App::DocumentObjectGroupPython] Cl_element026  label="Cl_element : 013"  # scripted group (container) (typed FeaturePython)
  n = 1
  ref = Cl_element
FEATURE [App::DocumentObjectGroupPython] G4_THALLIUM_CHLORIDE  # scripted group (container) (typed FeaturePython)
  Dunit = g/cm3
  Dvalue = 7.004
  Group = -> [Tl_element001,Cl_element026]
  conduct = 2
  density = 1
  expand = 3
  formula = G4_THALLIUM_CHLORIDE
  name = G4_THALLIUM_CHLORIDE
  specific = 4
FEATURE [App::DocumentObjectGroupPython] H_element100  label="H_element : 0.147"  # scripted group (container) (typed FeaturePython)
  n = 0.105
FEATURE [App::DocumentObjectGroupPython] C_element110  label="C_element : 0.256"  # scripted group (container) (typed FeaturePython)
  n = 0.256
FEATURE [App::DocumentObjectGroupPython] N_element042  label="N_element : 0.760"  # scripted group (container) (typed FeaturePython)
  n = 0.027
FEATURE [App::DocumentObjectGroupPython] O_element094  label="O_element : 0.602"  # scripted group (container) (typed FeaturePython)
  n = 0.602
FEATURE [App::DocumentObjectGroupPython] Na_element019  label="Na_element : 0.102"  # scripted group (container) (typed FeaturePython)
  n = 0.001
FEATURE [App::DocumentObjectGroupPython] P_element011  label="P_element : 0.109"  # scripted group (container) (typed FeaturePython)
  n = 0.002
FEATURE [App::DocumentObjectGroupPython] S_element022  label="S_element : 0.023"  # scripted group (container) (typed FeaturePython)
  n = 0.003
FEATURE [App::DocumentObjectGroupPython] Cl_element027  label="Cl_element : 0.591"  # scripted group (container) (typed FeaturePython)
  n = 0.002
FEATURE [App::DocumentObjectGroupPython] K_element012  label="K_element : 0.018"  # scripted group (container) (typed FeaturePython)
  n = 0.002
FEATURE [App::DocumentObjectGroupPython] G4_TISSUE_SOFT_ICRP  # scripted group (container) (typed FeaturePython)
  Dunit = g/cm3
  Dvalue = 1.03
  Group = -> [H_element100,C_element110,N_element042,O_element094,Na_element019,P_element011,S_element022,Cl_element027,K_element012]
  conduct = 2
  density = 1
  expand = 3
  formula = G4_TISSUE_SOFT_ICRP
  name = G4_TISSUE_SOFT_ICRP
  specific = 4
FEATURE [App::DocumentObjectGroupPython] H_element101  label="H_element : 0.148"  # scripted group (container) (typed FeaturePython)
  n = 0.101
FEATURE [App::DocumentObjectGroupPython] C_element111  label="C_element : 0.111"  # scripted group (container) (typed FeaturePython)
  n = 0.111
FEATURE [App::DocumentObjectGroupPython] N_element043  label="N_element : 0.026"  # scripted group (container) (typed FeaturePython)
  n = 0.026
FEATURE [App::DocumentObjectGroupPython] O_element095  label="O_element : 0.762"  # scripted group (container) (typed FeaturePython)
  n = 0.762
FEATURE [App::DocumentObjectGroupPython] G4_TISSUE_SOFT_ICRU_4  label="G4_TISSUE_SOFT_ICRU-4"  # scripted group (container) (typed FeaturePython)
  Dunit = g/cm3
  Dvalue = 1
  Group = -> [H_element101,C_element111,N_element043,O_element095]
  conduct = 2
  density = 1
  expand = 3
  formula = G4_TISSUE_SOFT_ICRU-4
  name = G4_TISSUE_SOFT_ICRU-4
  specific = 4
FEATURE [App::DocumentObjectGroupPython] H_element102  label="H_element : 0.149"  # scripted group (container) (typed FeaturePython)
  n = 0.101869
FEATURE [App::DocumentObjectGroupPython] C_element112  label="C_element : 0.456"  # scripted group (container) (typed FeaturePython)
  n = 0.456179
FEATURE [App::DocumentObjectGroupPython] N_element044  label="N_element : 0.761"  # scripted group (container) (typed FeaturePython)
  n = 0.035172
FEATURE [App::DocumentObjectGroupPython] O_element096  label="O_element : 0.407"  # scripted group (container) (typed FeaturePython)
  n = 0.40678
FEATURE [App::DocumentObjectGroupPython] G4_TISSUE_METHANE  label="G4_TISSUE-METHANE"  # scripted group (container) (typed FeaturePython)
  Dunit = g/cm3
  Dvalue = 0.00106409
  Group = -> [H_element102,C_element112,N_element044,O_element096]
  conduct = 2
  density = 1
  expand = 3
  formula = G4_TISSUE-METHANE
  name = G4_TISSUE-METHANE
  specific = 4
FEATURE [App::DocumentObjectGroupPython] H_element103  label="H_element : 0.103"  # scripted group (container) (typed FeaturePython)
  n = 0.102672
FEATURE [App::DocumentObjectGroupPython] C_element113  label="C_element : 0.569"  # scripted group (container) (typed FeaturePython)
  n = 0.56894
FEATURE [App::DocumentObjectGroupPython] N_element045  label="N_element : 0.762"  # scripted group (container) (typed FeaturePython)
  n = 0.035022
FEATURE [App::DocumentObjectGroupPython] O_element097  label="O_element : 0.293"  # scripted group (container) (typed FeaturePython)
  n = 0.293366
FEATURE [App::DocumentObjectGroupPython] G4_TISSUE_PROPANE  label="G4_TISSUE-PROPANE"  # scripted group (container) (typed FeaturePython)
  Dunit = g/cm3
  Dvalue = 0.00182628
  Group = -> [H_element103,C_element113,N_element045,O_element097]
  conduct = 2
  density = 1
  expand = 3
  formula = G4_TISSUE-PROPANE
  name = G4_TISSUE-PROPANE
  specific = 4
FEATURE [App::DocumentObjectGroupPython] Ti_element003  label="Ti_element : 1"  # scripted group (container) (typed FeaturePython)
  n = 1
  ref = Ti_element
FEATURE [App::DocumentObjectGroupPython] O_element098  label="O_element : 052"  # scripted group (container) (typed FeaturePython)
  n = 2
  ref = O_element
FEATURE [App::DocumentObjectGroupPython] G4_TITANIUM_DIOXIDE  # scripted group (container) (typed FeaturePython)
  Dunit = g/cm3
  Dvalue = 4.26
  Group = -> [Ti_element003,O_element098]
  conduct = 2
  density = 1
  expand = 3
  formula = G4_TITANIUM_DIOXIDE
  name = G4_TITANIUM_DIOXIDE
  specific = 4
FEATURE [App::DocumentObjectGroupPython] C_element114  label="C_element : 061"  # scripted group (container) (typed FeaturePython)
  n = 7
  ref = C_element
FEATURE [App::DocumentObjectGroupPython] H_element104  label="H_element : 055"  # scripted group (container) (typed FeaturePython)
  n = 8
  ref = H_element
FEATURE [App::DocumentObjectGroupPython] G4_TOLUENE  # scripted group (container) (typed FeaturePython)
  Dunit = g/cm3
  Dvalue = 0.8669
  Group = -> [C_element114,H_element104]
  conduct = 2
  density = 1
  expand = 3
  formula = G4_TOLUENE
  name = G4_TOLUENE
  specific = 4
FEATURE [App::DocumentObjectGroupPython] C_element115  label="C_element : 062"  # scripted group (container) (typed FeaturePython)
  n = 2
  ref = C_element
FEATURE [App::DocumentObjectGroupPython] H_element105  label="H_element : 056"  # scripted group (container) (typed FeaturePython)
  n = 1
  ref = H_element
FEATURE [App::DocumentObjectGroupPython] Cl_element028  label="Cl_element : 014"  # scripted group (container) (typed FeaturePython)
  n = 3
  ref = Cl_element
FEATURE [App::DocumentObjectGroupPython] G4_TRICHLOROETHYLENE  # scripted group (container) (typed FeaturePython)
  Dunit = g/cm3
  Dvalue = 1.46
  Group = -> [C_element115,H_element105,Cl_element028]
  conduct = 2
  density = 1
  expand = 3
  formula = G4_TRICHLOROETHYLENE
  name = G4_TRICHLOROETHYLENE
  specific = 4
FEATURE [App::DocumentObjectGroupPython] C_element116  label="C_element : 063"  # scripted group (container) (typed FeaturePython)
  n = 6
  ref = C_element
FEATURE [App::DocumentObjectGroupPython] H_element106  label="H_element : 15"  # scripted group (container) (typed FeaturePython)
  n = 15
  ref = H_element
FEATURE [App::DocumentObjectGroupPython] O_element099  label="O_element : 053"  # scripted group (container) (typed FeaturePython)
  n = 4
  ref = O_element
FEATURE [App::DocumentObjectGroupPython] P_element012  label="P_element : 1"  # scripted group (container) (typed FeaturePython)
  n = 1
  ref = P_element
FEATURE [App::DocumentObjectGroupPython] G4_TRIETHYL_PHOSPHATE  # scripted group (container) (typed FeaturePython)
  Dunit = g/cm3
  Dvalue = 1.07
  Group = -> [C_element116,H_element106,O_element099,P_element012]
  conduct = 2
  density = 1
  expand = 3
  formula = G4_TRIETHYL_PHOSPHATE
  name = G4_TRIETHYL_PHOSPHATE
  specific = 4
FEATURE [App::DocumentObjectGroupPython] W_element003  label="W_element : 003"  # scripted group (container) (typed FeaturePython)
  n = 1
  ref = W_element
FEATURE [App::DocumentObjectGroupPython] F_element017  label="F_element : 6"  # scripted group (container) (typed FeaturePython)
  n = 6
  ref = F_element
FEATURE [App::DocumentObjectGroupPython] G4_TUNGSTEN_HEXAFLUORIDE  # scripted group (container) (typed FeaturePython)
  Dunit = g/cm3
  Dvalue = 2.4
  Group = -> [W_element003,F_element017]
  conduct = 2
  density = 1
  expand = 3
  formula = G4_TUNGSTEN_HEXAFLUORIDE
  name = G4_TUNGSTEN_HEXAFLUORIDE
  specific = 4
FEATURE [App::DocumentObjectGroupPython] U_element001  label="U_element : 1"  # scripted group (container) (typed FeaturePython)
  n = 1
  ref = U_element
FEATURE [App::DocumentObjectGroupPython] C_element117  label="C_element : 064"  # scripted group (container) (typed FeaturePython)
  n = 2
  ref = C_element
FEATURE [App::DocumentObjectGroupPython] G4_URANIUM_DICARBIDE  # scripted group (container) (typed FeaturePython)
  Dunit = g/cm3
  Dvalue = 11.28
  Group = -> [U_element001,C_element117]
  conduct = 2
  density = 1
  expand = 3
  formula = G4_URANIUM_DICARBIDE
  name = G4_URANIUM_DICARBIDE
  specific = 4
FEATURE [App::DocumentObjectGroupPython] U_element002  label="U_element : 002"  # scripted group (container) (typed FeaturePython)
  n = 1
  ref = U_element
FEATURE [App::DocumentObjectGroupPython] C_element118  label="C_element : 065"  # scripted group (container) (typed FeaturePython)
  n = 1
  ref = C_element
FEATURE [App::DocumentObjectGroupPython] G4_URANIUM_MONOCARBIDE  # scripted group (container) (typed FeaturePython)
  Dunit = g/cm3
  Dvalue = 13.63
  Group = -> [U_element002,C_element118]
  conduct = 2
  density = 1
  expand = 3
  formula = G4_URANIUM_MONOCARBIDE
  name = G4_URANIUM_MONOCARBIDE
  specific = 4
FEATURE [App::DocumentObjectGroupPython] U_element003  label="U_element : 003"  # scripted group (container) (typed FeaturePython)
  n = 1
  ref = U_element
FEATURE [App::DocumentObjectGroupPython] O_element100  label="O_element : 054"  # scripted group (container) (typed FeaturePython)
  n = 2
  ref = O_element
FEATURE [App::DocumentObjectGroupPython] G4_URANIUM_OXIDE  # scripted group (container) (typed FeaturePython)
  Dunit = g/cm3
  Dvalue = 10.96
  Group = -> [U_element003,O_element100]
  conduct = 2
  density = 1
  expand = 3
  formula = G4_URANIUM_OXIDE
  name = G4_URANIUM_OXIDE
  specific = 4
FEATURE [App::DocumentObjectGroupPython] C_element119  label="C_element : 066"  # scripted group (container) (typed FeaturePython)
  n = 1
  ref = C_element
FEATURE [App::DocumentObjectGroupPython] H_element107  label="H_element : 057"  # scripted group (container) (typed FeaturePython)
  n = 4
  ref = H_element
FEATURE [App::DocumentObjectGroupPython] N_element046  label="N_element : 019"  # scripted group (container) (typed FeaturePython)
  n = 2
  ref = N_element
FEATURE [App::DocumentObjectGroupPython] O_element101  label="O_element : 055"  # scripted group (container) (typed FeaturePython)
  n = 1
  ref = O_element
FEATURE [App::DocumentObjectGroupPython] G4_UREA  # scripted group (container) (typed FeaturePython)
  Dunit = g/cm3
  Dvalue = 1.323
  Group = -> [C_element119,H_element107,N_element046,O_element101]
  conduct = 2
  density = 1
  expand = 3
  formula = G4_UREA
  name = G4_UREA
  specific = 4
FEATURE [App::DocumentObjectGroupPython] C_element120  label="C_element : 067"  # scripted group (container) (typed FeaturePython)
  n = 5
  ref = C_element
FEATURE [App::DocumentObjectGroupPython] H_element108  label="H_element : 058"  # scripted group (container) (typed FeaturePython)
  n = 11
  ref = H_element
FEATURE [App::DocumentObjectGroupPython] N_element047  label="N_element : 020"  # scripted group (container) (typed FeaturePython)
  n = 1
  ref = N_element
FEATURE [App::DocumentObjectGroupPython] O_element102  label="O_element : 056"  # scripted group (container) (typed FeaturePython)
  n = 2
  ref = O_element
FEATURE [App::DocumentObjectGroupPython] G4_VALINE  # scripted group (container) (typed FeaturePython)
  Dunit = g/cm3
  Dvalue = 1.23
  Group = -> [C_element120,H_element108,N_element047,O_element102]
  conduct = 2
  density = 1
  expand = 3
  formula = G4_VALINE
  name = G4_VALINE
  specific = 4
FEATURE [App::DocumentObjectGroupPython] H_element109  label="H_element : 0.009"  # scripted group (container) (typed FeaturePython)
  n = 0.009417
FEATURE [App::DocumentObjectGroupPython] C_element121  label="C_element : 0.281"  # scripted group (container) (typed FeaturePython)
  n = 0.280555
FEATURE [App::DocumentObjectGroupPython] F_element018  label="F_element : 0.710"  # scripted group (container) (typed FeaturePython)
  n = 0.710028
FEATURE [App::DocumentObjectGroupPython] G4_VITON  # scripted group (container) (typed FeaturePython)
  Dunit = g/cm3
  Dvalue = 1.8
  Group = -> [H_element109,C_element121,F_element018]
  conduct = 2
  density = 1
  expand = 3
  formula = G4_VITON
  name = G4_VITON
  specific = 4
FEATURE [App::DocumentObjectGroupPython] H_element110  label="H_element : 059"  # scripted group (container) (typed FeaturePython)
  n = 2
  ref = H_element
FEATURE [App::DocumentObjectGroupPython] O_element103  label="O_element : 057"  # scripted group (container) (typed FeaturePython)
  n = 1
  ref = O_element
FEATURE [App::DocumentObjectGroupPython] G4_WATER  # scripted group (container) (typed FeaturePython)
  Dunit = g/cm3
  Dvalue = 1
  Group = -> [H_element110,O_element103]
  conduct = 2
  density = 1
  expand = 3
  formula = G4_WATER
  name = G4_WATER
  specific = 4
FEATURE [App::DocumentObjectGroupPython] H_element111  label="H_element : 060"  # scripted group (container) (typed FeaturePython)
  n = 2
  ref = H_element
FEATURE [App::DocumentObjectGroupPython] O_element104  label="O_element : 058"  # scripted group (container) (typed FeaturePython)
  n = 1
  ref = O_element
FEATURE [App::DocumentObjectGroupPython] G4_WATER_VAPOR  # scripted group (container) (typed FeaturePython)
  Dunit = g/cm3
  Dvalue = 0.000756182
  Group = -> [H_element111,O_element104]
  conduct = 2
  density = 1
  expand = 3
  formula = G4_WATER_VAPOR
  name = G4_WATER_VAPOR
  specific = 4
FEATURE [App::DocumentObjectGroupPython] C_element122  label="C_element : 068"  # scripted group (container) (typed FeaturePython)
  n = 8
  ref = C_element
FEATURE [App::DocumentObjectGroupPython] H_element112  label="H_element : 061"  # scripted group (container) (typed FeaturePython)
  n = 10
  ref = H_element
FEATURE [App::DocumentObjectGroupPython] G4_XYLENE  # scripted group (container) (typed FeaturePython)
  Dunit = g/cm3
  Dvalue = 0.87
  Group = -> [C_element122,H_element112]
  conduct = 2
  density = 1
  expand = 3
  formula = G4_XYLENE
  name = G4_XYLENE
  specific = 4
FEATURE [App::DocumentObjectGroupPython] C_element123  label="C_element : 069"  # scripted group (container) (typed FeaturePython)
  n = 1
  ref = C_element
FEATURE [App::DocumentObjectGroupPython] G4_GRAPHITE  # scripted group (container) (typed FeaturePython)
  Dunit = g/cm3
  Dvalue = 2.21
  Group = -> [C_element123]
  conduct = 2
  density = 1
  expand = 3
  formula = G4_GRAPHITE
  name = G4_GRAPHITE
  specific = 4
FEATURE [App::DocumentObjectGroupPython] NIST  # scripted group (container) (typed FeaturePython)
  Group = -> [G4_A_150_TISSUE,G4_ACETONE,G4_ACETYLENE,G4_ADENINE,G4_ADIPOSE_TISSUE_ICRP,G4_AIR,G4_ALANINE,G4_ALUMINUM_OXIDE,G4_AMBER,G4_AMMONIA,G4_ANILINE,G4_ANTHRACENE,G4_B_100_BONE,G4_BAKELITE,G4_BARIUM_FLUORIDE,G4_BARIUM_SULFATE,G4_BENZENE,G4_BERYLLIUM_OXIDE,G4_BGO,G4_BLOOD_ICRP,G4_BONE_COMPACT_ICRU,G4_BONE_CORTICAL_ICRP,G4_BORON_CARBIDE,G4_BORON_OXIDE,G4_BRAIN_ICRP,G4_BUTANE,G4_N_BUTYL_ALCOHOL,G4_C_552,+152 more]
FEATURE [App::DocumentObjectGroupPython] H_element113  label="H_element : 062"  # scripted group (container) (typed FeaturePython)
  n = 1
  ref = H_element
FEATURE [App::DocumentObjectGroupPython] G4_H  # scripted group (container) (typed FeaturePython)
  Dunit = g/cm3
  Dvalue = 8.3748e-05
  Group = -> [H_element113]
  conduct = 2
  density = 1
  expand = 3
  formula = H
  name = G4_H
  specific = 4
FEATURE [App::DocumentObjectGroupPython] He_element001  label="He_element : 1"  # scripted group (container) (typed FeaturePython)
  n = 1
  ref = He_element
FEATURE [App::DocumentObjectGroupPython] G4_He  # scripted group (container) (typed FeaturePython)
  Dunit = g/cm3
  Dvalue = 0.000166322
  Group = -> [He_element001]
  conduct = 2
  density = 1
  expand = 3
  formula = He
  name = G4_He
  specific = 4
FEATURE [App::DocumentObjectGroupPython] Li_element008  label="Li_element : 008"  # scripted group (container) (typed FeaturePython)
  n = 1
  ref = Li_element
FEATURE [App::DocumentObjectGroupPython] G4_Li  # scripted group (container) (typed FeaturePython)
  Dunit = g/cm3
  Dvalue = 0.534
  Group = -> [Li_element008]
  conduct = 2
  density = 1
  expand = 3
  formula = Li
  name = G4_Li
  specific = 4
FEATURE [App::DocumentObjectGroupPython] Be_element002  label="Be_element : 002"  # scripted group (container) (typed FeaturePython)
  n = 1
  ref = Be_element
FEATURE [App::DocumentObjectGroupPython] G4_Be  # scripted group (container) (typed FeaturePython)
  Dunit = g/cm3
  Dvalue = 1.848
  Group = -> [Be_element002]
  conduct = 2
  density = 1
  expand = 3
  formula = Be
  name = G4_Be
  specific = 4
FEATURE [App::DocumentObjectGroupPython] B_element007  label="B_element : 007"  # scripted group (container) (typed FeaturePython)
  n = 1
  ref = B_element
FEATURE [App::DocumentObjectGroupPython] G4_B  # scripted group (container) (typed FeaturePython)
  Dunit = g/cm3
  Dvalue = 2.37
  Group = -> [B_element007]
  conduct = 2
  density = 1
  expand = 3
  formula = B
  name = G4_B
  specific = 4
FEATURE [App::DocumentObjectGroupPython] C_element124  label="C_element : 070"  # scripted group (container) (typed FeaturePython)
  n = 1
  ref = C_element
FEATURE [App::DocumentObjectGroupPython] G4_C  # scripted group (container) (typed FeaturePython)
  Dunit = g/cm3
  Dvalue = 2
  Group = -> [C_element124]
  conduct = 2
  density = 1
  expand = 3
  formula = C
  name = G4_C
  specific = 4
FEATURE [App::DocumentObjectGroupPython] N_element048  label="N_element : 021"  # scripted group (container) (typed FeaturePython)
  n = 1
  ref = N_element
FEATURE [App::DocumentObjectGroupPython] G4_N  # scripted group (container) (typed FeaturePython)
  Dunit = g/cm3
  Dvalue = 0.0011652
  Group = -> [N_element048]
  conduct = 2
  density = 1
  expand = 3
  formula = N
  name = G4_N
  specific = 4
FEATURE [App::DocumentObjectGroupPython] O_element105  label="O_element : 059"  # scripted group (container) (typed FeaturePython)
  n = 1
  ref = O_element
FEATURE [App::DocumentObjectGroupPython] G4_O  # scripted group (container) (typed FeaturePython)
  Dunit = g/cm3
  Dvalue = 0.00133151
  Group = -> [O_element105]
  conduct = 2
  density = 1
  expand = 3
  formula = O
  name = G4_O
  specific = 4
FEATURE [App::DocumentObjectGroupPython] F_element019  label="F_element : 008"  # scripted group (container) (typed FeaturePython)
  n = 1
  ref = F_element
FEATURE [App::DocumentObjectGroupPython] G4_F  # scripted group (container) (typed FeaturePython)
  Dunit = g/cm3
  Dvalue = 0.00158029
  Group = -> [F_element019]
  conduct = 2
  density = 1
  expand = 3
  formula = F
  name = G4_F
  specific = 4
FEATURE [App::DocumentObjectGroupPython] Ne_element001  label="Ne_element : 1"  # scripted group (container) (typed FeaturePython)
  n = 1
  ref = Ne_element
FEATURE [App::DocumentObjectGroupPython] G4_Ne  # scripted group (container) (typed FeaturePython)
  Dunit = g/cm3
  Dvalue = 0.000838505
  Group = -> [Ne_element001]
  conduct = 2
  density = 1
  expand = 3
  formula = Ne
  name = G4_Ne
  specific = 4
FEATURE [App::DocumentObjectGroupPython] Na_element020  label="Na_element : 005"  # scripted group (container) (typed FeaturePython)
  n = 1
  ref = Na_element
FEATURE [App::DocumentObjectGroupPython] G4_Na  # scripted group (container) (typed FeaturePython)
  Dunit = g/cm3
  Dvalue = 0.971
  Group = -> [Na_element020]
  conduct = 2
  density = 1
  expand = 3
  formula = Na
  name = G4_Na
  specific = 4
FEATURE [App::DocumentObjectGroupPython] Mg_element011  label="Mg_element : 005"  # scripted group (container) (typed FeaturePython)
  n = 1
  ref = Mg_element
FEATURE [App::DocumentObjectGroupPython] G4_Mg  # scripted group (container) (typed FeaturePython)
  Dunit = g/cm3
  Dvalue = 1.74
  Group = -> [Mg_element011]
  conduct = 2
  density = 1
  expand = 3
  formula = Mg
  name = G4_Mg
  specific = 4
FEATURE [App::DocumentObjectGroupPython] Al_element004  label="Al_element : 1"  # scripted group (container) (typed FeaturePython)
  n = 1
  ref = Al_element
FEATURE [App::DocumentObjectGroupPython] G4_Al  # scripted group (container) (typed FeaturePython)
  Dunit = g/cm3
  Dvalue = 2.699
  Group = -> [Al_element004]
  conduct = 2
  density = 1
  expand = 3
  formula = Al
  name = G4_Al
  specific = 4
FEATURE [App::DocumentObjectGroupPython] Si_element007  label="Si_element : 002"  # scripted group (container) (typed FeaturePython)
  n = 1
  ref = Si_element
FEATURE [App::DocumentObjectGroupPython] G4_Si  # scripted group (container) (typed FeaturePython)
  Dunit = g/cm3
  Dvalue = 2.33
  Group = -> [Si_element007]
  conduct = 2
  density = 1
  expand = 3
  formula = Si
  name = G4_Si
  specific = 4
FEATURE [App::DocumentObjectGroupPython] P_element013  label="P_element : 002"  # scripted group (container) (typed FeaturePython)
  n = 1
  ref = P_element
FEATURE [App::DocumentObjectGroupPython] G4_P  # scripted group (container) (typed FeaturePython)
  Dunit = g/cm3
  Dvalue = 2.2
  Group = -> [P_element013]
  conduct = 2
  density = 1
  expand = 3
  formula = P
  name = G4_P
  specific = 4
FEATURE [App::DocumentObjectGroupPython] S_element023  label="S_element : 007"  # scripted group (container) (typed FeaturePython)
  n = 1
  ref = S_element
FEATURE [App::DocumentObjectGroupPython] G4_S  # scripted group (container) (typed FeaturePython)
  Dunit = g/cm3
  Dvalue = 2
  Group = -> [S_element023]
  conduct = 2
  density = 1
  expand = 3
  formula = S
  name = G4_S
  specific = 4
FEATURE [App::DocumentObjectGroupPython] Cl_element029  label="Cl_element : 015"  # scripted group (container) (typed FeaturePython)
  n = 1
  ref = Cl_element
FEATURE [App::DocumentObjectGroupPython] G4_Cl  # scripted group (container) (typed FeaturePython)
  Dunit = g/cm3
  Dvalue = 0.00299473
  Group = -> [Cl_element029]
  conduct = 2
  density = 1
  expand = 3
  formula = Cl
  name = G4_Cl
  specific = 4
FEATURE [App::DocumentObjectGroupPython] Ar_element002  label="Ar_element : 1"  # scripted group (container) (typed FeaturePython)
  n = 1
  ref = Ar_element
FEATURE [App::DocumentObjectGroupPython] G4_Ar  # scripted group (container) (typed FeaturePython)
  Dunit = g/cm3
  Dvalue = 0.00166201
  Group = -> [Ar_element002]
  conduct = 2
  density = 1
  expand = 3
  formula = Ar
  name = G4_Ar
  specific = 4
FEATURE [App::DocumentObjectGroupPython] K_element013  label="K_element : 003"  # scripted group (container) (typed FeaturePython)
  n = 1
  ref = K_element
FEATURE [App::DocumentObjectGroupPython] G4_K  # scripted group (container) (typed FeaturePython)
  Dunit = g/cm3
  Dvalue = 0.862
  Group = -> [K_element013]
  conduct = 2
  density = 1
  expand = 3
  formula = K
  name = G4_K
  specific = 4
FEATURE [App::DocumentObjectGroupPython] Ca_element014  label="Ca_element : 007"  # scripted group (container) (typed FeaturePython)
  n = 1
  ref = Ca_element
FEATURE [App::DocumentObjectGroupPython] G4_Ca  # scripted group (container) (typed FeaturePython)
  Dunit = g/cm3
  Dvalue = 1.55
  Group = -> [Ca_element014]
  conduct = 2
  density = 1
  expand = 3
  formula = Ca
  name = G4_Ca
  specific = 4
FEATURE [App::DocumentObjectGroupPython] Sc_element001  label="Sc_element : 1"  # scripted group (container) (typed FeaturePython)
  n = 1
  ref = Sc_element
FEATURE [App::DocumentObjectGroupPython] G4_Sc  # scripted group (container) (typed FeaturePython)
  Dunit = g/cm3
  Dvalue = 2.989
  Group = -> [Sc_element001]
  conduct = 2
  density = 1
  expand = 3
  formula = Sc
  name = G4_Sc
  specific = 4
FEATURE [App::DocumentObjectGroupPython] Ti_element004  label="Ti_element : 002"  # scripted group (container) (typed FeaturePython)
  n = 1
  ref = Ti_element
FEATURE [App::DocumentObjectGroupPython] G4_Ti  # scripted group (container) (typed FeaturePython)
  Dunit = g/cm3
  Dvalue = 4.54
  Group = -> [Ti_element004]
  conduct = 2
  density = 1
  expand = 3
  formula = Ti
  name = G4_Ti
  specific = 4
FEATURE [App::DocumentObjectGroupPython] V_element001  label="V_element : 1"  # scripted group (container) (typed FeaturePython)
  n = 1
  ref = V_element
FEATURE [App::DocumentObjectGroupPython] G4_V  # scripted group (container) (typed FeaturePython)
  Dunit = g/cm3
  Dvalue = 6.11
  Group = -> [V_element001]
  conduct = 2
  density = 1
  expand = 3
  formula = V
  name = G4_V
  specific = 4
FEATURE [App::DocumentObjectGroupPython] Cr_element001  label="Cr_element : 1"  # scripted group (container) (typed FeaturePython)
  n = 1
  ref = Cr_element
FEATURE [App::DocumentObjectGroupPython] G4_Cr  # scripted group (container) (typed FeaturePython)
  Dunit = g/cm3
  Dvalue = 7.18
  Group = -> [Cr_element001]
  conduct = 2
  density = 1
  expand = 3
  formula = Cr
  name = G4_Cr
  specific = 4
FEATURE [App::DocumentObjectGroupPython] Mn_element001  label="Mn_element : 1"  # scripted group (container) (typed FeaturePython)
  n = 1
  ref = Mn_element
FEATURE [App::DocumentObjectGroupPython] G4_Mn  # scripted group (container) (typed FeaturePython)
  Dunit = g/cm3
  Dvalue = 7.44
  Group = -> [Mn_element001]
  conduct = 2
  density = 1
  expand = 3
  formula = Mn
  name = G4_Mn
  specific = 4
FEATURE [App::DocumentObjectGroupPython] Fe_element007  label="Fe_element : 004"  # scripted group (container) (typed FeaturePython)
  n = 1
  ref = Fe_element
FEATURE [App::DocumentObjectGroupPython] G4_Fe  # scripted group (container) (typed FeaturePython)
  Dunit = g/cm3
  Dvalue = 7.874
  Group = -> [Fe_element007]
  conduct = 2
  density = 1
  expand = 3
  formula = Fe
  name = G4_Fe
  specific = 4
FEATURE [App::DocumentObjectGroupPython] Co_element001  label="Co_element : 1"  # scripted group (container) (typed FeaturePython)
  n = 1
  ref = Co_element
FEATURE [App::DocumentObjectGroupPython] G4_Co  # scripted group (container) (typed FeaturePython)
  Dunit = g/cm3
  Dvalue = 8.9
  Group = -> [Co_element001]
  conduct = 2
  density = 1
  expand = 3
  formula = Co
  name = G4_Co
  specific = 4
FEATURE [App::DocumentObjectGroupPython] Ni_element001  label="Ni_element : 1"  # scripted group (container) (typed FeaturePython)
  n = 1
  ref = Ni_element
FEATURE [App::DocumentObjectGroupPython] G4_Ni  # scripted group (container) (typed FeaturePython)
  Dunit = g/cm3
  Dvalue = 8.902
  Group = -> [Ni_element001]
  conduct = 2
  density = 1
  expand = 3
  formula = Ni
  name = G4_Ni
  specific = 4
FEATURE [App::DocumentObjectGroupPython] Cu_element001  label="Cu_element : 1"  # scripted group (container) (typed FeaturePython)
  n = 1
  ref = Cu_element
FEATURE [App::DocumentObjectGroupPython] G4_Cu  # scripted group (container) (typed FeaturePython)
  Dunit = g/cm3
  Dvalue = 8.96
  Group = -> [Cu_element001]
  conduct = 2
  density = 1
  expand = 3
  formula = Cu
  name = G4_Cu
  specific = 4
FEATURE [App::DocumentObjectGroupPython] Zn_element001  label="Zn_element : 1"  # scripted group (container) (typed FeaturePython)
  n = 1
  ref = Zn_element
FEATURE [App::DocumentObjectGroupPython] G4_Zn  # scripted group (container) (typed FeaturePython)
  Dunit = g/cm3
  Dvalue = 7.133
  Group = -> [Zn_element001]
  conduct = 2
  density = 1
  expand = 3
  formula = Zn
  name = G4_Zn
  specific = 4
FEATURE [App::DocumentObjectGroupPython] Ga_element002  label="Ga_element : 002"  # scripted group (container) (typed FeaturePython)
  n = 1
  ref = Ga_element
FEATURE [App::DocumentObjectGroupPython] G4_Ga  # scripted group (container) (typed FeaturePython)
  Dunit = g/cm3
  Dvalue = 5.904
  Group = -> [Ga_element002]
  conduct = 2
  density = 1
  expand = 3
  formula = Ga
  name = G4_Ga
  specific = 4
FEATURE [App::DocumentObjectGroupPython] Ge_element002  label="Ge_element : 1"  # scripted group (container) (typed FeaturePython)
  n = 1
  ref = Ge_element
FEATURE [App::DocumentObjectGroupPython] G4_Ge  # scripted group (container) (typed FeaturePython)
  Dunit = g/cm3
  Dvalue = 5.323
  Group = -> [Ge_element002]
  conduct = 2
  density = 1
  expand = 3
  formula = Ge
  name = G4_Ge
  specific = 4
FEATURE [App::DocumentObjectGroupPython] As_element003  label="As_element : 002"  # scripted group (container) (typed FeaturePython)
  n = 1
  ref = As_element
FEATURE [App::DocumentObjectGroupPython] G4_As  # scripted group (container) (typed FeaturePython)
  Dunit = g/cm3
  Dvalue = 5.73
  Group = -> [As_element003]
  conduct = 2
  density = 1
  expand = 3
  formula = As
  name = G4_As
  specific = 4
FEATURE [App::DocumentObjectGroupPython] Se_element001  label="Se_element : 1"  # scripted group (container) (typed FeaturePython)
  n = 1
  ref = Se_element
FEATURE [App::DocumentObjectGroupPython] G4_Se  # scripted group (container) (typed FeaturePython)
  Dunit = g/cm3
  Dvalue = 4.5
  Group = -> [Se_element001]
  conduct = 2
  density = 1
  expand = 3
  formula = Se
  name = G4_Se
  specific = 4
FEATURE [App::DocumentObjectGroupPython] Br_element007  label="Br_element : 004"  # scripted group (container) (typed FeaturePython)
  n = 1
  ref = Br_element
FEATURE [App::DocumentObjectGroupPython] G4_Br  # scripted group (container) (typed FeaturePython)
  Dunit = g/cm3
  Dvalue = 0.0070721
  Group = -> [Br_element007]
  conduct = 2
  density = 1
  expand = 3
  formula = Br
  name = G4_Br
  specific = 4
FEATURE [App::DocumentObjectGroupPython] Kr_element001  label="Kr_element : 1"  # scripted group (container) (typed FeaturePython)
  n = 1
  ref = Kr_element
FEATURE [App::DocumentObjectGroupPython] G4_Kr  # scripted group (container) (typed FeaturePython)
  Dunit = g/cm3
  Dvalue = 0.00347832
  Group = -> [Kr_element001]
  conduct = 2
  density = 1
  expand = 3
  formula = Kr
  name = G4_Kr
  specific = 4
FEATURE [App::DocumentObjectGroupPython] Rb_element001  label="Rb_element : 1"  # scripted group (container) (typed FeaturePython)
  n = 1
  ref = Rb_element
FEATURE [App::DocumentObjectGroupPython] G4_Rb  # scripted group (container) (typed FeaturePython)
  Dunit = g/cm3
  Dvalue = 1.532
  Group = -> [Rb_element001]
  conduct = 2
  density = 1
  expand = 3
  formula = Rb
  name = G4_Rb
  specific = 4
FEATURE [App::DocumentObjectGroupPython] Sr_element001  label="Sr_element : 1"  # scripted group (container) (typed FeaturePython)
  n = 1
  ref = Sr_element
FEATURE [App::DocumentObjectGroupPython] G4_Sr  # scripted group (container) (typed FeaturePython)
  Dunit = g/cm3
  Dvalue = 2.54
  Group = -> [Sr_element001]
  conduct = 2
  density = 1
  expand = 3
  formula = Sr
  name = G4_Sr
  specific = 4
FEATURE [App::DocumentObjectGroupPython] Y_element001  label="Y_element : 1"  # scripted group (container) (typed FeaturePython)
  n = 1
  ref = Y_element
FEATURE [App::DocumentObjectGroupPython] G4_Y  # scripted group (container) (typed FeaturePython)
  Dunit = g/cm3
  Dvalue = 4.469
  Group = -> [Y_element001]
  conduct = 2
  density = 1
  expand = 3
  formula = Y
  name = G4_Y
  specific = 4
FEATURE [App::DocumentObjectGroupPython] Zr_element001  label="Zr_element : 1"  # scripted group (container) (typed FeaturePython)
  n = 1
  ref = Zr_element
FEATURE [App::DocumentObjectGroupPython] G4_Zr  # scripted group (container) (typed FeaturePython)
  Dunit = g/cm3
  Dvalue = 6.506
  Group = -> [Zr_element001]
  conduct = 2
  density = 1
  expand = 3
  formula = Zr
  name = G4_Zr
  specific = 4
FEATURE [App::DocumentObjectGroupPython] Nb_element001  label="Nb_element : 1"  # scripted group (container) (typed FeaturePython)
  n = 1
  ref = Nb_element
FEATURE [App::DocumentObjectGroupPython] G4_Nb  # scripted group (container) (typed FeaturePython)
  Dunit = g/cm3
  Dvalue = 8.57
  Group = -> [Nb_element001]
  conduct = 2
  density = 1
  expand = 3
  formula = Nb
  name = G4_Nb
  specific = 4
FEATURE [App::DocumentObjectGroupPython] Mo_element001  label="Mo_element : 1"  # scripted group (container) (typed FeaturePython)
  n = 1
  ref = Mo_element
FEATURE [App::DocumentObjectGroupPython] G4_Mo  # scripted group (container) (typed FeaturePython)
  Dunit = g/cm3
  Dvalue = 10.22
  Group = -> [Mo_element001]
  conduct = 2
  density = 1
  expand = 3
  formula = Mo
  name = G4_Mo
  specific = 4
FEATURE [App::DocumentObjectGroupPython] Tc_element001  label="Tc_element : 1"  # scripted group (container) (typed FeaturePython)
  n = 1
  ref = Tc_element
FEATURE [App::DocumentObjectGroupPython] G4_Tc  # scripted group (container) (typed FeaturePython)
  Dunit = g/cm3
  Dvalue = 11.5
  Group = -> [Tc_element001]
  conduct = 2
  density = 1
  expand = 3
  formula = Tc
  name = G4_Tc
  specific = 4
FEATURE [App::DocumentObjectGroupPython] Ru_element001  label="Ru_element : 1"  # scripted group (container) (typed FeaturePython)
  n = 1
  ref = Ru_element
FEATURE [App::DocumentObjectGroupPython] G4_Ru  # scripted group (container) (typed FeaturePython)
  Dunit = g/cm3
  Dvalue = 12.41
  Group = -> [Ru_element001]
  conduct = 2
  density = 1
  expand = 3
  formula = Ru
  name = G4_Ru
  specific = 4
FEATURE [App::DocumentObjectGroupPython] Rh_element001  label="Rh_element : 1"  # scripted group (container) (typed FeaturePython)
  n = 1
  ref = Rh_element
FEATURE [App::DocumentObjectGroupPython] G4_Rh  # scripted group (container) (typed FeaturePython)
  Dunit = g/cm3
  Dvalue = 12.41
  Group = -> [Rh_element001]
  conduct = 2
  density = 1
  expand = 3
  formula = Rh
  name = G4_Rh
  specific = 4
FEATURE [App::DocumentObjectGroupPython] Pd_element001  label="Pd_element : 1"  # scripted group (container) (typed FeaturePython)
  n = 1
  ref = Pd_element
FEATURE [App::DocumentObjectGroupPython] G4_Pd  # scripted group (container) (typed FeaturePython)
  Dunit = g/cm3
  Dvalue = 12.02
  Group = -> [Pd_element001]
  conduct = 2
  density = 1
  expand = 3
  formula = Pd
  name = G4_Pd
  specific = 4
FEATURE [App::DocumentObjectGroupPython] Ag_element006  label="Ag_element : 004"  # scripted group (container) (typed FeaturePython)
  n = 1
  ref = Ag_element
FEATURE [App::DocumentObjectGroupPython] G4_Ag  # scripted group (container) (typed FeaturePython)
  Dunit = g/cm3
  Dvalue = 10.5
  Group = -> [Ag_element006]
  conduct = 2
  density = 1
  expand = 3
  formula = Ag
  name = G4_Ag
  specific = 4
FEATURE [App::DocumentObjectGroupPython] Cd_element003  label="Cd_element : 003"  # scripted group (container) (typed FeaturePython)
  n = 1
  ref = Cd_element
FEATURE [App::DocumentObjectGroupPython] G4_Cd  # scripted group (container) (typed FeaturePython)
  Dunit = g/cm3
  Dvalue = 8.65
  Group = -> [Cd_element003]
  conduct = 2
  density = 1
  expand = 3
  formula = Cd
  name = G4_Cd
  specific = 4
FEATURE [App::DocumentObjectGroupPython] In_element001  label="In_element : 1"  # scripted group (container) (typed FeaturePython)
  n = 1
  ref = In_element
FEATURE [App::DocumentObjectGroupPython] G4_In  # scripted group (container) (typed FeaturePython)
  Dunit = g/cm3
  Dvalue = 7.31
  Group = -> [In_element001]
  conduct = 2
  density = 1
  expand = 3
  formula = In
  name = G4_In
  specific = 4
FEATURE [App::DocumentObjectGroupPython] Sn_element001  label="Sn_element : 1"  # scripted group (container) (typed FeaturePython)
  n = 1
  ref = Sn_element
FEATURE [App::DocumentObjectGroupPython] G4_Sn  # scripted group (container) (typed FeaturePython)
  Dunit = g/cm3
  Dvalue = 7.31
  Group = -> [Sn_element001]
  conduct = 2
  density = 1
  expand = 3
  formula = Sn
  name = G4_Sn
  specific = 4
FEATURE [App::DocumentObjectGroupPython] Sb_element001  label="Sb_element : 1"  # scripted group (container) (typed FeaturePython)
  n = 1
  ref = Sb_element
FEATURE [App::DocumentObjectGroupPython] G4_Sb  # scripted group (container) (typed FeaturePython)
  Dunit = g/cm3
  Dvalue = 6.691
  Group = -> [Sb_element001]
  conduct = 2
  density = 1
  expand = 3
  formula = Sb
  name = G4_Sb
  specific = 4
FEATURE [App::DocumentObjectGroupPython] Te_element002  label="Te_element : 002"  # scripted group (container) (typed FeaturePython)
  n = 1
  ref = Te_element
FEATURE [App::DocumentObjectGroupPython] G4_Te  # scripted group (container) (typed FeaturePython)
  Dunit = g/cm3
  Dvalue = 6.24
  Group = -> [Te_element002]
  conduct = 2
  density = 1
  expand = 3
  formula = Te
  name = G4_Te
  specific = 4
FEATURE [App::DocumentObjectGroupPython] I_element010  label="I_element : 006"  # scripted group (container) (typed FeaturePython)
  n = 1
  ref = I_element
FEATURE [App::DocumentObjectGroupPython] G4_I  # scripted group (container) (typed FeaturePython)
  Dunit = g/cm3
  Dvalue = 4.93
  Group = -> [I_element010]
  conduct = 2
  density = 1
  expand = 3
  formula = I
  name = G4_I
  specific = 4
FEATURE [App::DocumentObjectGroupPython] Xe_element001  label="Xe_element : 1"  # scripted group (container) (typed FeaturePython)
  n = 1
  ref = Xe_element
FEATURE [App::DocumentObjectGroupPython] G4_Xe  # scripted group (container) (typed FeaturePython)
  Dunit = g/cm3
  Dvalue = 0.00548536
  Group = -> [Xe_element001]
  conduct = 2
  density = 1
  expand = 3
  formula = Xe
  name = G4_Xe
  specific = 4
FEATURE [App::DocumentObjectGroupPython] Cs_element003  label="Cs_element : 003"  # scripted group (container) (typed FeaturePython)
  n = 1
  ref = Cs_element
FEATURE [App::DocumentObjectGroupPython] G4_Cs  # scripted group (container) (typed FeaturePython)
  Dunit = g/cm3
  Dvalue = 1.873
  Group = -> [Cs_element003]
  conduct = 2
  density = 1
  expand = 3
  formula = Cs
  name = G4_Cs
  specific = 4
FEATURE [App::DocumentObjectGroupPython] Ba_element003  label="Ba_element : 003"  # scripted group (container) (typed FeaturePython)
  n = 1
  ref = Ba_element
FEATURE [App::DocumentObjectGroupPython] G4_Ba  # scripted group (container) (typed FeaturePython)
  Dunit = g/cm3
  Dvalue = 3.5
  Group = -> [Ba_element003]
  conduct = 2
  density = 1
  expand = 3
  formula = Ba
  name = G4_Ba
  specific = 4
FEATURE [App::DocumentObjectGroupPython] La_element003  label="La_element : 003"  # scripted group (container) (typed FeaturePython)
  n = 1
  ref = La_element
FEATURE [App::DocumentObjectGroupPython] G4_La  # scripted group (container) (typed FeaturePython)
  Dunit = g/cm3
  Dvalue = 6.154
  Group = -> [La_element003]
  conduct = 2
  density = 1
  expand = 3
  formula = La
  name = G4_La
  specific = 4
FEATURE [App::DocumentObjectGroupPython] Ce_element002  label="Ce_element : 1"  # scripted group (container) (typed FeaturePython)
  n = 1
  ref = Ce_element
FEATURE [App::DocumentObjectGroupPython] G4_Ce  # scripted group (container) (typed FeaturePython)
  Dunit = g/cm3
  Dvalue = 6.657
  Group = -> [Ce_element002]
  conduct = 2
  density = 1
  expand = 3
  formula = Ce
  name = G4_Ce
  specific = 4
FEATURE [App::DocumentObjectGroupPython] Pr_element001  label="Pr_element : 1"  # scripted group (container) (typed FeaturePython)
  n = 1
  ref = Pr_element
FEATURE [App::DocumentObjectGroupPython] G4_Pr  # scripted group (container) (typed FeaturePython)
  Dunit = g/cm3
  Dvalue = 6.71
  Group = -> [Pr_element001]
  conduct = 2
  density = 1
  expand = 3
  formula = Pr
  name = G4_Pr
  specific = 4
FEATURE [App::DocumentObjectGroupPython] Nd_element001  label="Nd_element : 1"  # scripted group (container) (typed FeaturePython)
  n = 1
  ref = Nd_element
FEATURE [App::DocumentObjectGroupPython] G4_Nd  # scripted group (container) (typed FeaturePython)
  Dunit = g/cm3
  Dvalue = 6.9
  Group = -> [Nd_element001]
  conduct = 2
  density = 1
  expand = 3
  formula = Nd
  name = G4_Nd
  specific = 4
FEATURE [App::DocumentObjectGroupPython] Pm_element001  label="Pm_element : 1"  # scripted group (container) (typed FeaturePython)
  n = 1
  ref = Pm_element
FEATURE [App::DocumentObjectGroupPython] G4_Pm  # scripted group (container) (typed FeaturePython)
  Dunit = g/cm3
  Dvalue = 7.22
  Group = -> [Pm_element001]
  conduct = 2
  density = 1
  expand = 3
  formula = Pm
  name = G4_Pm
  specific = 4
FEATURE [App::DocumentObjectGroupPython] Sm_element001  label="Sm_element : 1"  # scripted group (container) (typed FeaturePython)
  n = 1
  ref = Sm_element
FEATURE [App::DocumentObjectGroupPython] G4_Sm  # scripted group (container) (typed FeaturePython)
  Dunit = g/cm3
  Dvalue = 7.46
  Group = -> [Sm_element001]
  conduct = 2
  density = 1
  expand = 3
  formula = Sm
  name = G4_Sm
  specific = 4
FEATURE [App::DocumentObjectGroupPython] Eu_element001  label="Eu_element : 1"  # scripted group (container) (typed FeaturePython)
  n = 1
  ref = Eu_element
FEATURE [App::DocumentObjectGroupPython] G4_Eu  # scripted group (container) (typed FeaturePython)
  Dunit = g/cm3
  Dvalue = 5.243
  Group = -> [Eu_element001]
  conduct = 2
  density = 1
  expand = 3
  formula = Eu
  name = G4_Eu
  specific = 4
FEATURE [App::DocumentObjectGroupPython] Gd_element002  label="Gd_element : 1"  # scripted group (container) (typed FeaturePython)
  n = 1
  ref = Gd_element
FEATURE [App::DocumentObjectGroupPython] G4_Gd  # scripted group (container) (typed FeaturePython)
  Dunit = g/cm3
  Dvalue = 7.9004
  Group = -> [Gd_element002]
  conduct = 2
  density = 1
  expand = 3
  formula = Gd
  name = G4_Gd
  specific = 4
FEATURE [App::DocumentObjectGroupPython] Tb_element001  label="Tb_element : 1"  # scripted group (container) (typed FeaturePython)
  n = 1
  ref = Tb_element
FEATURE [App::DocumentObjectGroupPython] G4_Tb  # scripted group (container) (typed FeaturePython)
  Dunit = g/cm3
  Dvalue = 8.229
  Group = -> [Tb_element001]
  conduct = 2
  density = 1
  expand = 3
  formula = Tb
  name = G4_Tb
  specific = 4
FEATURE [App::DocumentObjectGroupPython] Dy_element001  label="Dy_element : 1"  # scripted group (container) (typed FeaturePython)
  n = 1
  ref = Dy_element
FEATURE [App::DocumentObjectGroupPython] G4_Dy  # scripted group (container) (typed FeaturePython)
  Dunit = g/cm3
  Dvalue = 8.55
  Group = -> [Dy_element001]
  conduct = 2
  density = 1
  expand = 3
  formula = Dy
  name = G4_Dy
  specific = 4
FEATURE [App::DocumentObjectGroupPython] Ho_element001  label="Ho_element : 1"  # scripted group (container) (typed FeaturePython)
  n = 1
  ref = Ho_element
FEATURE [App::DocumentObjectGroupPython] G4_Ho  # scripted group (container) (typed FeaturePython)
  Dunit = g/cm3
  Dvalue = 8.795
  Group = -> [Ho_element001]
  conduct = 2
  density = 1
  expand = 3
  formula = Ho
  name = G4_Ho
  specific = 4
FEATURE [App::DocumentObjectGroupPython] Er_element001  label="Er_element : 1"  # scripted group (container) (typed FeaturePython)
  n = 1
  ref = Er_element
FEATURE [App::DocumentObjectGroupPython] G4_Er  # scripted group (container) (typed FeaturePython)
  Dunit = g/cm3
  Dvalue = 9.066
  Group = -> [Er_element001]
  conduct = 2
  density = 1
  expand = 3
  formula = Er
  name = G4_Er
  specific = 4
FEATURE [App::DocumentObjectGroupPython] Tm_element001  label="Tm_element : 1"  # scripted group (container) (typed FeaturePython)
  n = 1
  ref = Tm_element
FEATURE [App::DocumentObjectGroupPython] G4_Tm  # scripted group (container) (typed FeaturePython)
  Dunit = g/cm3
  Dvalue = 9.321
  Group = -> [Tm_element001]
  conduct = 2
  density = 1
  expand = 3
  formula = Tm
  name = G4_Tm
  specific = 4
FEATURE [App::DocumentObjectGroupPython] Yb_element001  label="Yb_element : 1"  # scripted group (container) (typed FeaturePython)
  n = 1
  ref = Yb_element
FEATURE [App::DocumentObjectGroupPython] G4_Yb  # scripted group (container) (typed FeaturePython)
  Dunit = g/cm3
  Dvalue = 6.73
  Group = -> [Yb_element001]
  conduct = 2
  density = 1
  expand = 3
  formula = Yb
  name = G4_Yb
  specific = 4
FEATURE [App::DocumentObjectGroupPython] Lu_element001  label="Lu_element : 1"  # scripted group (container) (typed FeaturePython)
  n = 1
  ref = Lu_element
FEATURE [App::DocumentObjectGroupPython] G4_Lu  # scripted group (container) (typed FeaturePython)
  Dunit = g/cm3
  Dvalue = 9.84
  Group = -> [Lu_element001]
  conduct = 2
  density = 1
  expand = 3
  formula = Lu
  name = G4_Lu
  specific = 4
FEATURE [App::DocumentObjectGroupPython] Hf_element001  label="Hf_element : 1"  # scripted group (container) (typed FeaturePython)
  n = 1
  ref = Hf_element
FEATURE [App::DocumentObjectGroupPython] G4_Hf  # scripted group (container) (typed FeaturePython)
  Dunit = g/cm3
  Dvalue = 13.31
  Group = -> [Hf_element001]
  conduct = 2
  density = 1
  expand = 3
  formula = Hf
  name = G4_Hf
  specific = 4
FEATURE [App::DocumentObjectGroupPython] Ta_element001  label="Ta_element : 1"  # scripted group (container) (typed FeaturePython)
  n = 1
  ref = Ta_element
FEATURE [App::DocumentObjectGroupPython] G4_Ta  # scripted group (container) (typed FeaturePython)
  Dunit = g/cm3
  Dvalue = 16.654
  Group = -> [Ta_element001]
  conduct = 2
  density = 1
  expand = 3
  formula = Ta
  name = G4_Ta
  specific = 4
FEATURE [App::DocumentObjectGroupPython] W_element004  label="W_element : 004"  # scripted group (container) (typed FeaturePython)
  n = 1
  ref = W_element
FEATURE [App::DocumentObjectGroupPython] G4_W  # scripted group (container) (typed FeaturePython)
  Dunit = g/cm3
  Dvalue = 19.3
  Group = -> [W_element004]
  conduct = 2
  density = 1
  expand = 3
  formula = W
  name = G4_W
  specific = 4
FEATURE [App::DocumentObjectGroupPython] Re_element001  label="Re_element : 1"  # scripted group (container) (typed FeaturePython)
  n = 1
  ref = Re_element
FEATURE [App::DocumentObjectGroupPython] G4_Re  # scripted group (container) (typed FeaturePython)
  Dunit = g/cm3
  Dvalue = 21.02
  Group = -> [Re_element001]
  conduct = 2
  density = 1
  expand = 3
  formula = Re
  name = G4_Re
  specific = 4
FEATURE [App::DocumentObjectGroupPython] Os_element001  label="Os_element : 1"  # scripted group (container) (typed FeaturePython)
  n = 1
  ref = Os_element
FEATURE [App::DocumentObjectGroupPython] G4_Os  # scripted group (container) (typed FeaturePython)
  Dunit = g/cm3
  Dvalue = 22.57
  Group = -> [Os_element001]
  conduct = 2
  density = 1
  expand = 3
  formula = Os
  name = G4_Os
  specific = 4
FEATURE [App::DocumentObjectGroupPython] Ir_element001  label="Ir_element : 1"  # scripted group (container) (typed FeaturePython)
  n = 1
  ref = Ir_element
FEATURE [App::DocumentObjectGroupPython] G4_Ir  # scripted group (container) (typed FeaturePython)
  Dunit = g/cm3
  Dvalue = 22.42
  Group = -> [Ir_element001]
  conduct = 2
  density = 1
  expand = 3
  formula = Ir
  name = G4_Ir
  specific = 4
FEATURE [App::DocumentObjectGroupPython] Pt_element001  label="Pt_element : 1"  # scripted group (container) (typed FeaturePython)
  n = 1
  ref = Pt_element
FEATURE [App::DocumentObjectGroupPython] G4_Pt  # scripted group (container) (typed FeaturePython)
  Dunit = g/cm3
  Dvalue = 21.45
  Group = -> [Pt_element001]
  conduct = 2
  density = 1
  expand = 3
  formula = Pt
  name = G4_Pt
  specific = 4
FEATURE [App::DocumentObjectGroupPython] Au_element001  label="Au_element : 1"  # scripted group (container) (typed FeaturePython)
  n = 1
  ref = Au_element
FEATURE [App::DocumentObjectGroupPython] G4_Au  # scripted group (container) (typed FeaturePython)
  Dunit = g/cm3
  Dvalue = 19.32
  Group = -> [Au_element001]
  conduct = 2
  density = 1
  expand = 3
  formula = Au
  name = G4_Au
  specific = 4
FEATURE [App::DocumentObjectGroupPython] Hg_element002  label="Hg_element : 002"  # scripted group (container) (typed FeaturePython)
  n = 1
  ref = Hg_element
FEATURE [App::DocumentObjectGroupPython] G4_Hg  # scripted group (container) (typed FeaturePython)
  Dunit = g/cm3
  Dvalue = 13.546
  Group = -> [Hg_element002]
  conduct = 2
  density = 1
  expand = 3
  formula = Hg
  name = G4_Hg
  specific = 4
FEATURE [App::DocumentObjectGroupPython] Tl_element002  label="Tl_element : 002"  # scripted group (container) (typed FeaturePython)
  n = 1
  ref = Tl_element
FEATURE [App::DocumentObjectGroupPython] G4_Tl  # scripted group (container) (typed FeaturePython)
  Dunit = g/cm3
  Dvalue = 11.72
  Group = -> [Tl_element002]
  conduct = 2
  density = 1
  expand = 3
  formula = Tl
  name = G4_Tl
  specific = 4
FEATURE [App::DocumentObjectGroupPython] Pb_element003  label="Pb_element : 1"  # scripted group (container) (typed FeaturePython)
  n = 1
  ref = Pb_element
FEATURE [App::DocumentObjectGroupPython] G4_Pb  # scripted group (container) (typed FeaturePython)
  Dunit = g/cm3
  Dvalue = 11.35
  Group = -> [Pb_element003]
  conduct = 2
  density = 1
  expand = 3
  formula = Pb
  name = G4_Pb
  specific = 4
FEATURE [App::DocumentObjectGroupPython] Bi_element002  label="Bi_element : 1"  # scripted group (container) (typed FeaturePython)
  n = 1
  ref = Bi_element
FEATURE [App::DocumentObjectGroupPython] G4_Bi  # scripted group (container) (typed FeaturePython)
  Dunit = g/cm3
  Dvalue = 9.747
  Group = -> [Bi_element002]
  conduct = 2
  density = 1
  expand = 3
  formula = Bi
  name = G4_Bi
  specific = 4
FEATURE [App::DocumentObjectGroupPython] Po_element001  label="Po_element : 1"  # scripted group (container) (typed FeaturePython)
  n = 1
  ref = Po_element
FEATURE [App::DocumentObjectGroupPython] G4_Po  # scripted group (container) (typed FeaturePython)
  Dunit = g/cm3
  Dvalue = 9.32
  Group = -> [Po_element001]
  conduct = 2
  density = 1
  expand = 3
  formula = Po
  name = G4_Po
  specific = 4
FEATURE [App::DocumentObjectGroupPython] At_element001  label="At_element : 1"  # scripted group (container) (typed FeaturePython)
  n = 1
  ref = At_element
FEATURE [App::DocumentObjectGroupPython] G4_At  # scripted group (container) (typed FeaturePython)
  Dunit = g/cm3
  Dvalue = 9.32
  Group = -> [At_element001]
  conduct = 2
  density = 1
  expand = 3
  formula = At
  name = G4_At
  specific = 4
FEATURE [App::DocumentObjectGroupPython] Rn_element001  label="Rn_element : 1"  # scripted group (container) (typed FeaturePython)
  n = 1
  ref = Rn_element
FEATURE [App::DocumentObjectGroupPython] G4_Rn  # scripted group (container) (typed FeaturePython)
  Dunit = g/cm3
  Dvalue = 0.00900662
  Group = -> [Rn_element001]
  conduct = 2
  density = 1
  expand = 3
  formula = Rn
  name = G4_Rn
  specific = 4
FEATURE [App::DocumentObjectGroupPython] Fr_element001  label="Fr_element : 1"  # scripted group (container) (typed FeaturePython)
  n = 1
  ref = Fr_element
FEATURE [App::DocumentObjectGroupPython] G4_Fr  # scripted group (container) (typed FeaturePython)
  Dunit = g/cm3
  Dvalue = 1
  Group = -> [Fr_element001]
  conduct = 2
  density = 1
  expand = 3
  formula = Fr
  name = G4_Fr
  specific = 4
FEATURE [App::DocumentObjectGroupPython] Ra_element001  label="Ra_element : 1"  # scripted group (container) (typed FeaturePython)
  n = 1
  ref = Ra_element
FEATURE [App::DocumentObjectGroupPython] G4_Ra  # scripted group (container) (typed FeaturePython)
  Dunit = g/cm3
  Dvalue = 5
  Group = -> [Ra_element001]
  conduct = 2
  density = 1
  expand = 3
  formula = Ra
  name = G4_Ra
  specific = 4
FEATURE [App::DocumentObjectGroupPython] Ac_element001  label="Ac_element : 1"  # scripted group (container) (typed FeaturePython)
  n = 1
  ref = Ac_element
FEATURE [App::DocumentObjectGroupPython] G4_Ac  # scripted group (container) (typed FeaturePython)
  Dunit = g/cm3
  Dvalue = 10.07
  Group = -> [Ac_element001]
  conduct = 2
  density = 1
  expand = 3
  formula = Ac
  name = G4_Ac
  specific = 4
FEATURE [App::DocumentObjectGroupPython] Th_element001  label="Th_element : 1"  # scripted group (container) (typed FeaturePython)
  n = 1
  ref = Th_element
FEATURE [App::DocumentObjectGroupPython] G4_Th  # scripted group (container) (typed FeaturePython)
  Dunit = g/cm3
  Dvalue = 11.72
  Group = -> [Th_element001]
  conduct = 2
  density = 1
  expand = 3
  formula = Th
  name = G4_Th
  specific = 4
FEATURE [App::DocumentObjectGroupPython] Pa_element001  label="Pa_element : 1"  # scripted group (container) (typed FeaturePython)
  n = 1
  ref = Pa_element
FEATURE [App::DocumentObjectGroupPython] G4_Pa  # scripted group (container) (typed FeaturePython)
  Dunit = g/cm3
  Dvalue = 15.37
  Group = -> [Pa_element001]
  conduct = 2
  density = 1
  expand = 3
  formula = Pa
  name = G4_Pa
  specific = 4
FEATURE [App::DocumentObjectGroupPython] U_element004  label="U_element : 004"  # scripted group (container) (typed FeaturePython)
  n = 1
  ref = U_element
FEATURE [App::DocumentObjectGroupPython] G4_U  # scripted group (container) (typed FeaturePython)
  Dunit = g/cm3
  Dvalue = 18.95
  Group = -> [U_element004]
  conduct = 2
  density = 1
  expand = 3
  formula = U
  name = G4_U
  specific = 4
FEATURE [App::DocumentObjectGroupPython] Np_element001  label="Np_element : 1"  # scripted group (container) (typed FeaturePython)
  n = 1
  ref = Np_element
FEATURE [App::DocumentObjectGroupPython] G4_Np  # scripted group (container) (typed FeaturePython)
  Dunit = g/cm3
  Dvalue = 20.25
  Group = -> [Np_element001]
  conduct = 2
  density = 1
  expand = 3
  formula = Np
  name = G4_Np
  specific = 4
FEATURE [App::DocumentObjectGroupPython] Pu_element002  label="Pu_element : 002"  # scripted group (container) (typed FeaturePython)
  n = 1
  ref = Pu_element
FEATURE [App::DocumentObjectGroupPython] G4_Pu  # scripted group (container) (typed FeaturePython)
  Dunit = g/cm3
  Dvalue = 19.84
  Group = -> [Pu_element002]
  conduct = 2
  density = 1
  expand = 3
  formula = Pu
  name = G4_Pu
  specific = 4
FEATURE [App::DocumentObjectGroupPython] Am_element001  label="Am_element : 1"  # scripted group (container) (typed FeaturePython)
  n = 1
  ref = Am_element
FEATURE [App::DocumentObjectGroupPython] G4_Am  # scripted group (container) (typed FeaturePython)
  Dunit = g/cm3
  Dvalue = 13.67
  Group = -> [Am_element001]
  conduct = 2
  density = 1
  expand = 3
  formula = Am
  name = G4_Am
  specific = 4
FEATURE [App::DocumentObjectGroupPython] Cm_element001  label="Cm_element : 1"  # scripted group (container) (typed FeaturePython)
  n = 1
  ref = Cm_element
FEATURE [App::DocumentObjectGroupPython] G4_Cm  # scripted group (container) (typed FeaturePython)
  Dunit = g/cm3
  Dvalue = 13.51
  Group = -> [Cm_element001]
  conduct = 2
  density = 1
  expand = 3
  formula = Cm
  name = G4_Cm
  specific = 4
FEATURE [App::DocumentObjectGroupPython] Bk_element001  label="Bk_element : 1"  # scripted group (container) (typed FeaturePython)
  n = 1
  ref = Bk_element
FEATURE [App::DocumentObjectGroupPython] G4_Bk  # scripted group (container) (typed FeaturePython)
  Dunit = g/cm3
  Dvalue = 14
  Group = -> [Bk_element001]
  conduct = 2
  density = 1
  expand = 3
  formula = Bk
  name = G4_Bk
  specific = 4
FEATURE [App::DocumentObjectGroupPython] Cf_element001  label="Cf_element : 1"  # scripted group (container) (typed FeaturePython)
  n = 1
  ref = Cf_element
FEATURE [App::DocumentObjectGroupPython] G4_Cf  # scripted group (container) (typed FeaturePython)
  Dunit = g/cm3
  Dvalue = 10
  Group = -> [Cf_element001]
  conduct = 2
  density = 1
  expand = 3
  formula = Cf
  name = G4_Cf
  specific = 4
FEATURE [App::DocumentObjectGroupPython] Element  # scripted group (container) (typed FeaturePython)
  Group = -> [G4_H,G4_He,G4_Li,G4_Be,G4_B,G4_C,G4_N,G4_O,G4_F,G4_Ne,G4_Na,G4_Mg,G4_Al,G4_Si,G4_P,G4_S,G4_Cl,G4_Ar,G4_K,G4_Ca,G4_Sc,G4_Ti,G4_V,G4_Cr,G4_Mn,G4_Fe,G4_Co,G4_Ni,G4_Cu,G4_Zn,G4_Ga,G4_Ge,G4_As,G4_Se,G4_Br,G4_Kr,G4_Rb,G4_Sr,G4_Y,G4_Zr,G4_Nb,G4_Mo,G4_Tc,G4_Ru,G4_Rh,G4_Pd,G4_Ag,G4_Cd,G4_In,G4_Sn,G4_Sb,G4_Te,G4_I,G4_Xe,G4_Cs,G4_Ba,G4_La,G4_Ce,G4_Pr,G4_Nd,G4_Pm,G4_Sm,G4_Eu,G4_Gd,G4_Tb,G4_Dy,G4_Ho,G4_Er,+30 more]
FEATURE [App::DocumentObjectGroupPython] H_element114  label="H_element : 063"  # scripted group (container) (typed FeaturePython)
  n = 2
  ref = H_element
FEATURE [App::DocumentObjectGroupPython] G4_lH2  # scripted group (container) (typed FeaturePython)
  Dunit = g/cm3
  Dvalue = 0.0708
  Group = -> [H_element114]
  conduct = 2
  density = 1
  expand = 3
  formula = G4_lH2
  name = G4_lH2
  specific = 4
FEATURE [App::DocumentObjectGroupPython] N_element049  label="N_element : 022"  # scripted group (container) (typed FeaturePython)
  n = 2
  ref = N_element
FEATURE [App::DocumentObjectGroupPython] G4_lN2  # scripted group (container) (typed FeaturePython)
  Dunit = g/cm3
  Dvalue = 0.807
  Group = -> [N_element049]
  conduct = 2
  density = 1
  expand = 3
  formula = G4_lN2
  name = G4_lN2
  specific = 4
FEATURE [App::DocumentObjectGroupPython] O_element106  label="O_element : 060"  # scripted group (container) (typed FeaturePython)
  n = 2
  ref = O_element
FEATURE [App::DocumentObjectGroupPython] G4_lO2  # scripted group (container) (typed FeaturePython)
  Dunit = g/cm3
  Dvalue = 1.141
  Group = -> [O_element106]
  conduct = 2
  density = 1
  expand = 3
  formula = G4_lO2
  name = G4_lO2
  specific = 4
FEATURE [App::DocumentObjectGroupPython] Ar  label="Ar : 1"  # scripted group (container) (typed FeaturePython)
  n = 1
  ref = Ar
FEATURE [App::DocumentObjectGroupPython] G4_lAr  # scripted group (container) (typed FeaturePython)
  Dunit = g/cm3
  Dvalue = 1.396
  Group = -> [Ar]
  conduct = 2
  density = 1
  expand = 3
  formula = G4_lAr
  name = G4_lAr
  specific = 4
FEATURE [App::DocumentObjectGroupPython] Br  label="Br : 1"  # scripted group (container) (typed FeaturePython)
  n = 1
  ref = Br
FEATURE [App::DocumentObjectGroupPython] G4_lBr  # scripted group (container) (typed FeaturePython)
  Dunit = g/cm3
  Dvalue = 3.1028
  Group = -> [Br]
  conduct = 2
  density = 1
  expand = 3
  formula = G4_lBr
  name = G4_lBr
  specific = 4
FEATURE [App::DocumentObjectGroupPython] Kr  label="Kr : 1"  # scripted group (container) (typed FeaturePython)
  n = 1
  ref = Kr
FEATURE [App::DocumentObjectGroupPython] G4_lKr  # scripted group (container) (typed FeaturePython)
  Dunit = g/cm3
  Dvalue = 2.418
  Group = -> [Kr]
  conduct = 2
  density = 1
  expand = 3
  formula = G4_lKr
  name = G4_lKr
  specific = 4
FEATURE [App::DocumentObjectGroupPython] Xe  label="Xe : 1"  # scripted group (container) (typed FeaturePython)
  n = 1
  ref = Xe
FEATURE [App::DocumentObjectGroupPython] G4_lXe  # scripted group (container) (typed FeaturePython)
  Dunit = g/cm3
  Dvalue = 2.953
  Group = -> [Xe]
  conduct = 2
  density = 1
  expand = 3
  formula = G4_lXe
  name = G4_lXe
  specific = 4
FEATURE [App::DocumentObjectGroupPython] O_element107  label="O_element : 061"  # scripted group (container) (typed FeaturePython)
  n = 4
  ref = O_element
FEATURE [App::DocumentObjectGroupPython] Pb_element004  label="Pb_element : 002"  # scripted group (container) (typed FeaturePython)
  n = 1
  ref = Pb_element
FEATURE [App::DocumentObjectGroupPython] W_element005  label="W_element : 005"  # scripted group (container) (typed FeaturePython)
  n = 1
  ref = W_element
FEATURE [App::DocumentObjectGroupPython] G4_PbWO4  # scripted group (container) (typed FeaturePython)
  Dunit = g/cm3
  Dvalue = 8.28
  Group = -> [O_element107,Pb_element004,W_element005]
  conduct = 2
  density = 1
  expand = 3
  formula = G4_PbWO4
  name = G4_PbWO4
  specific = 4
FEATURE [App::DocumentObjectGroupPython] alactic  label="alactic : 1"  # scripted group (container) (typed FeaturePython)
  n = 1
  ref = alactic
FEATURE [App::DocumentObjectGroupPython] G4_Galactic  # scripted group (container) (typed FeaturePython)
  Dunit = g/cm3
  Dvalue = 0
  Group = -> [alactic]
  conduct = 2
  density = 1
  expand = 3
  formula = G4_Galactic
  name = G4_Galactic
  specific = 4
FEATURE [App::DocumentObjectGroupPython] RAPHITE_POROUS  label="RAPHITE_POROUS : 1"  # scripted group (container) (typed FeaturePython)
  n = 1
  ref = RAPHITE_POROUS
FEATURE [App::DocumentObjectGroupPython] G4_GRAPHITE_POROUS  # scripted group (container) (typed FeaturePython)
  Dunit = g/cm3
  Dvalue = 1.7
  Group = -> [RAPHITE_POROUS]
  conduct = 2
  density = 1
  expand = 3
  formula = G4_GRAPHITE_POROUS
  name = G4_GRAPHITE_POROUS
  specific = 4
FEATURE [App::DocumentObjectGroupPython] H_element115  label="H_element : 0.150"  # scripted group (container) (typed FeaturePython)
  n = 0.080538
FEATURE [App::DocumentObjectGroupPython] C_element125  label="C_element : 0.600"  # scripted group (container) (typed FeaturePython)
  n = 0.599848
FEATURE [App::DocumentObjectGroupPython] O_element108  label="O_element : 0.320"  # scripted group (container) (typed FeaturePython)
  n = 0.319614
FEATURE [App::DocumentObjectGroupPython] G4_LUCITE  # scripted group (container) (typed FeaturePython)
  Dunit = g/cm3
  Dvalue = 1.19
  Group = -> [H_element115,C_element125,O_element108]
  conduct = 2
  density = 1
  expand = 3
  formula = G4_LUCITE
  name = G4_LUCITE
  specific = 4
FEATURE [App::DocumentObjectGroupPython] Cu_element002  label="Cu_element : 62"  # scripted group (container) (typed FeaturePython)
  n = 62
  ref = Cu_element
FEATURE [App::DocumentObjectGroupPython] Zn_element002  label="Zn_element : 35"  # scripted group (container) (typed FeaturePython)
  n = 35
  ref = Zn_element
FEATURE [App::DocumentObjectGroupPython] Pb_element005  label="Pb_element : 3"  # scripted group (container) (typed FeaturePython)
  n = 3
  ref = Pb_element
FEATURE [App::DocumentObjectGroupPython] G4_BRASS  # scripted group (container) (typed FeaturePython)
  Dunit = g/cm3
  Dvalue = 8.52
  Group = -> [Cu_element002,Zn_element002,Pb_element005]
  conduct = 2
  density = 1
  expand = 3
  formula = G4_BRASS
  name = G4_BRASS
  specific = 4
FEATURE [App::DocumentObjectGroupPython] Cu_element003  label="Cu_element : 89"  # scripted group (container) (typed FeaturePython)
  n = 89
  ref = Cu_element
FEATURE [App::DocumentObjectGroupPython] Zn_element003  label="Zn_element : 9"  # scripted group (container) (typed FeaturePython)
  n = 9
  ref = Zn_element
FEATURE [App::DocumentObjectGroupPython] Pb_element006  label="Pb_element : 2"  # scripted group (container) (typed FeaturePython)
  n = 2
  ref = Pb_element
FEATURE [App::DocumentObjectGroupPython] G4_BRONZE  # scripted group (container) (typed FeaturePython)
  Dunit = g/cm3
  Dvalue = 8.82
  Group = -> [Cu_element003,Zn_element003,Pb_element006]
  conduct = 2
  density = 1
  expand = 3
  formula = G4_BRONZE
  name = G4_BRONZE
  specific = 4
FEATURE [App::DocumentObjectGroupPython] Fe_element008  label="Fe_element : 74"  # scripted group (container) (typed FeaturePython)
  n = 74
  ref = Fe_element
FEATURE [App::DocumentObjectGroupPython] Cr_element002  label="Cr_element : 18"  # scripted group (container) (typed FeaturePython)
  n = 18
  ref = Cr_element
FEATURE [App::DocumentObjectGroupPython] Ni_element002  label="Ni_element : 8"  # scripted group (container) (typed FeaturePython)
  n = 8
  ref = Ni_element
FEATURE [App::DocumentObjectGroupPython] G4_STAINLESS_STEEL  label="G4_STAINLESS-STEEL"  # scripted group (container) (typed FeaturePython)
  Dunit = g/cm3
  Dvalue = 8
  Group = -> [Fe_element008,Cr_element002,Ni_element002]
  conduct = 2
  density = 1
  expand = 3
  formula = G4_STAINLESS-STEEL
  name = G4_STAINLESS-STEEL
  specific = 4
FEATURE [App::DocumentObjectGroupPython] H_element116  label="H_element : 064"  # scripted group (container) (typed FeaturePython)
  n = 18
  ref = H_element
FEATURE [App::DocumentObjectGroupPython] C_element126  label="C_element : 071"  # scripted group (container) (typed FeaturePython)
  n = 12
  ref = C_element
FEATURE [App::DocumentObjectGroupPython] O_element109  label="O_element : 062"  # scripted group (container) (typed FeaturePython)
  n = 7
  ref = O_element
FEATURE [App::DocumentObjectGroupPython] G4_CR39  # scripted group (container) (typed FeaturePython)
  Dunit = g/cm3
  Dvalue = 1.32
  Group = -> [H_element116,C_element126,O_element109]
  conduct = 2
  density = 1
  expand = 3
  formula = G4_CR39
  name = G4_CR39
  specific = 4
FEATURE [App::DocumentObjectGroupPython] H_element117  label="H_element : 38"  # scripted group (container) (typed FeaturePython)
  n = 38
  ref = H_element
FEATURE [App::DocumentObjectGroupPython] C_element127  label="C_element : 072"  # scripted group (container) (typed FeaturePython)
  n = 18
  ref = C_element
FEATURE [App::DocumentObjectGroupPython] O_element110  label="O_element : 063"  # scripted group (container) (typed FeaturePython)
  n = 1
  ref = O_element
FEATURE [App::DocumentObjectGroupPython] G4_OCTADECANOL  # scripted group (container) (typed FeaturePython)
  Dunit = g/cm3
  Dvalue = 0.812
  Group = -> [H_element117,C_element127,O_element110]
  conduct = 2
  density = 1
  expand = 3
  formula = G4_OCTADECANOL
  name = G4_OCTADECANOL
  specific = 4
FEATURE [App::DocumentObjectGroupPython] HEP  # scripted group (container) (typed FeaturePython)
  Group = -> [G4_lH2,G4_lN2,G4_lO2,G4_lAr,G4_lBr,G4_lKr,G4_lXe,G4_PbWO4,G4_Galactic,G4_GRAPHITE_POROUS,G4_LUCITE,G4_BRASS,G4_BRONZE,G4_STAINLESS_STEEL,G4_CR39,G4_OCTADECANOL]
FEATURE [App::DocumentObjectGroupPython] C_element128  label="C_element : 073"  # scripted group (container) (typed FeaturePython)
  n = 14
  ref = C_element
FEATURE [App::DocumentObjectGroupPython] H_element118  label="H_element : 065"  # scripted group (container) (typed FeaturePython)
  n = 10
  ref = H_element
FEATURE [App::DocumentObjectGroupPython] O_element111  label="O_element : 064"  # scripted group (container) (typed FeaturePython)
  n = 2
  ref = O_element
FEATURE [App::DocumentObjectGroupPython] N_element050  label="N_element : 023"  # scripted group (container) (typed FeaturePython)
  n = 2
  ref = N_element
FEATURE [App::DocumentObjectGroupPython] G4_KEVLAR  # scripted group (container) (typed FeaturePython)
  Dunit = g/cm3
  Dvalue = 1.44
  Group = -> [C_element128,H_element118,O_element111,N_element050]
  conduct = 2
  density = 1
  expand = 3
  formula = G4_KEVLAR
  name = G4_KEVLAR
  specific = 4
FEATURE [App::DocumentObjectGroupPython] C_element129  label="C_element : 074"  # scripted group (container) (typed FeaturePython)
  n = 10
  ref = C_element
FEATURE [App::DocumentObjectGroupPython] H_element119  label="H_element : 066"  # scripted group (container) (typed FeaturePython)
  n = 8
  ref = H_element
FEATURE [App::DocumentObjectGroupPython] O_element112  label="O_element : 065"  # scripted group (container) (typed FeaturePython)
  n = 4
  ref = O_element
FEATURE [App::DocumentObjectGroupPython] G4_DACRON  # scripted group (container) (typed FeaturePython)
  Dunit = g/cm3
  Dvalue = 1.4
  Group = -> [C_element129,H_element119,O_element112]
  conduct = 2
  density = 1
  expand = 3
  formula = G4_DACRON
  name = G4_DACRON
  specific = 4
FEATURE [App::DocumentObjectGroupPython] C_element130  label="C_element : 075"  # scripted group (container) (typed FeaturePython)
  n = 4
  ref = C_element
FEATURE [App::DocumentObjectGroupPython] H_element120  label="H_element : 067"  # scripted group (container) (typed FeaturePython)
  n = 5
  ref = H_element
FEATURE [App::DocumentObjectGroupPython] Cl_element030  label="Cl_element : 016"  # scripted group (container) (typed FeaturePython)
  n = 1
  ref = Cl_element
FEATURE [App::DocumentObjectGroupPython] G4_NEOPRENE  # scripted group (container) (typed FeaturePython)
  Dunit = g/cm3
  Dvalue = 1.23
  Group = -> [C_element130,H_element120,Cl_element030]
  conduct = 2
  density = 1
  expand = 3
  formula = G4_NEOPRENE
  name = G4_NEOPRENE
  specific = 4
FEATURE [App::DocumentObjectGroupPython] Space  # scripted group (container) (typed FeaturePython)
  Group = -> [G4_KEVLAR,G4_DACRON,G4_NEOPRENE]
FEATURE [App::DocumentObjectGroupPython] H_element121  label="H_element : 068"  # scripted group (container) (typed FeaturePython)
  n = 5
  ref = H_element
FEATURE [App::DocumentObjectGroupPython] C_element131  label="C_element : 076"  # scripted group (container) (typed FeaturePython)
  n = 4
  ref = C_element
FEATURE [App::DocumentObjectGroupPython] N_element051  label="N_element : 3"  # scripted group (container) (typed FeaturePython)
  n = 3
  ref = N_element
FEATURE [App::DocumentObjectGroupPython] O_element113  label="O_element : 066"  # scripted group (container) (typed FeaturePython)
  n = 1
  ref = O_element
FEATURE [App::DocumentObjectGroupPython] G4_CYTOSINE  # scripted group (container) (typed FeaturePython)
  Dunit = g/cm3
  Dvalue = 1.55
  Group = -> [H_element121,C_element131,N_element051,O_element113]
  conduct = 2
  density = 1
  expand = 3
  formula = G4_CYTOSINE
  name = G4_CYTOSINE
  specific = 4
FEATURE [App::DocumentObjectGroupPython] H_element122  label="H_element : 069"  # scripted group (container) (typed FeaturePython)
  n = 6
  ref = H_element
FEATURE [App::DocumentObjectGroupPython] C_element132  label="C_element : 077"  # scripted group (container) (typed FeaturePython)
  n = 5
  ref = C_element
FEATURE [App::DocumentObjectGroupPython] N_element052  label="N_element : 024"  # scripted group (container) (typed FeaturePython)
  n = 2
  ref = N_element
FEATURE [App::DocumentObjectGroupPython] O_element114  label="O_element : 067"  # scripted group (container) (typed FeaturePython)
  n = 2
  ref = O_element
FEATURE [App::DocumentObjectGroupPython] G4_THYMINE  # scripted group (container) (typed FeaturePython)
  Dunit = g/cm3
  Dvalue = 1.23
  Group = -> [H_element122,C_element132,N_element052,O_element114]
  conduct = 2
  density = 1
  expand = 3
  formula = G4_THYMINE
  name = G4_THYMINE
  specific = 4
FEATURE [App::DocumentObjectGroupPython] H_element123  label="H_element : 070"  # scripted group (container) (typed FeaturePython)
  n = 4
  ref = H_element
FEATURE [App::DocumentObjectGroupPython] C_element133  label="C_element : 078"  # scripted group (container) (typed FeaturePython)
  n = 4
  ref = C_element
FEATURE [App::DocumentObjectGroupPython] N_element053  label="N_element : 025"  # scripted group (container) (typed FeaturePython)
  n = 2
  ref = N_element
FEATURE [App::DocumentObjectGroupPython] O_element115  label="O_element : 068"  # scripted group (container) (typed FeaturePython)
  n = 2
  ref = O_element
FEATURE [App::DocumentObjectGroupPython] G4_URACIL  # scripted group (container) (typed FeaturePython)
  Dunit = g/cm3
  Dvalue = 1.32
  Group = -> [H_element123,C_element133,N_element053,O_element115]
  conduct = 2
  density = 1
  expand = 3
  formula = G4_URACIL
  name = G4_URACIL
  specific = 4
FEATURE [App::DocumentObjectGroupPython] H_element124  label="H_element : 071"  # scripted group (container) (typed FeaturePython)
  n = 4
  ref = H_element
FEATURE [App::DocumentObjectGroupPython] C_element134  label="C_element : 079"  # scripted group (container) (typed FeaturePython)
  n = 5
  ref = C_element
FEATURE [App::DocumentObjectGroupPython] N_element054  label="N_element : 026"  # scripted group (container) (typed FeaturePython)
  n = 5
  ref = N_element
FEATURE [App::DocumentObjectGroupPython] G4_DNA_ADENINE  # scripted group (container) (typed FeaturePython)
  Dunit = g/cm3
  Dvalue = 1
  Group = -> [H_element124,C_element134,N_element054]
  conduct = 2
  density = 1
  expand = 3
  formula = G4_DNA_ADENINE
  name = G4_DNA_ADENINE
  specific = 4
FEATURE [App::DocumentObjectGroupPython] H_element125  label="H_element : 072"  # scripted group (container) (typed FeaturePython)
  n = 4
  ref = H_element
FEATURE [App::DocumentObjectGroupPython] C_element135  label="C_element : 080"  # scripted group (container) (typed FeaturePython)
  n = 5
  ref = C_element
FEATURE [App::DocumentObjectGroupPython] N_element055  label="N_element : 027"  # scripted group (container) (typed FeaturePython)
  n = 5
  ref = N_element
FEATURE [App::DocumentObjectGroupPython] O_element116  label="O_element : 069"  # scripted group (container) (typed FeaturePython)
  n = 1
  ref = O_element
FEATURE [App::DocumentObjectGroupPython] G4_DNA_GUANINE  # scripted group (container) (typed FeaturePython)
  Dunit = g/cm3
  Dvalue = 1
  Group = -> [H_element125,C_element135,N_element055,O_element116]
  conduct = 2
  density = 1
  expand = 3
  formula = G4_DNA_GUANINE
  name = G4_DNA_GUANINE
  specific = 4
FEATURE [App::DocumentObjectGroupPython] H_element126  label="H_element : 073"  # scripted group (container) (typed FeaturePython)
  n = 4
  ref = H_element
FEATURE [App::DocumentObjectGroupPython] C_element136  label="C_element : 081"  # scripted group (container) (typed FeaturePython)
  n = 4
  ref = C_element
FEATURE [App::DocumentObjectGroupPython] N_element056  label="N_element : 028"  # scripted group (container) (typed FeaturePython)
  n = 3
  ref = N_element
FEATURE [App::DocumentObjectGroupPython] O_element117  label="O_element : 070"  # scripted group (container) (typed FeaturePython)
  n = 1
  ref = O_element
FEATURE [App::DocumentObjectGroupPython] G4_DNA_CYTOSINE  # scripted group (container) (typed FeaturePython)
  Dunit = g/cm3
  Dvalue = 1
  Group = -> [H_element126,C_element136,N_element056,O_element117]
  conduct = 2
  density = 1
  expand = 3
  formula = G4_DNA_CYTOSINE
  name = G4_DNA_CYTOSINE
  specific = 4
FEATURE [App::DocumentObjectGroupPython] H_element127  label="H_element : 074"  # scripted group (container) (typed FeaturePython)
  n = 5
  ref = H_element
FEATURE [App::DocumentObjectGroupPython] C_element137  label="C_element : 082"  # scripted group (container) (typed FeaturePython)
  n = 5
  ref = C_element
FEATURE [App::DocumentObjectGroupPython] N_element057  label="N_element : 029"  # scripted group (container) (typed FeaturePython)
  n = 2
  ref = N_element
FEATURE [App::DocumentObjectGroupPython] O_element118  label="O_element : 071"  # scripted group (container) (typed FeaturePython)
  n = 2
  ref = O_element
FEATURE [App::DocumentObjectGroupPython] G4_DNA_THYMINE  # scripted group (container) (typed FeaturePython)
  Dunit = g/cm3
  Dvalue = 1
  Group = -> [H_element127,C_element137,N_element057,O_element118]
  conduct = 2
  density = 1
  expand = 3
  formula = G4_DNA_THYMINE
  name = G4_DNA_THYMINE
  specific = 4
FEATURE [App::DocumentObjectGroupPython] H_element128  label="H_element : 075"  # scripted group (container) (typed FeaturePython)
  n = 3
  ref = H_element
FEATURE [App::DocumentObjectGroupPython] C_element138  label="C_element : 083"  # scripted group (container) (typed FeaturePython)
  n = 4
  ref = C_element
FEATURE [App::DocumentObjectGroupPython] N_element058  label="N_element : 030"  # scripted group (container) (typed FeaturePython)
  n = 2
  ref = N_element
FEATURE [App::DocumentObjectGroupPython] O_element119  label="O_element : 072"  # scripted group (container) (typed FeaturePython)
  n = 2
  ref = O_element
FEATURE [App::DocumentObjectGroupPython] G4_DNA_URACIL  # scripted group (container) (typed FeaturePython)
  Dunit = g/cm3
  Dvalue = 1
  Group = -> [H_element128,C_element138,N_element058,O_element119]
  conduct = 2
  density = 1
  expand = 3
  formula = G4_DNA_URACIL
  name = G4_DNA_URACIL
  specific = 4
FEATURE [App::DocumentObjectGroupPython] H_element129  label="H_element : 076"  # scripted group (container) (typed FeaturePython)
  n = 10
  ref = H_element
FEATURE [App::DocumentObjectGroupPython] C_element139  label="C_element : 084"  # scripted group (container) (typed FeaturePython)
  n = 10
  ref = C_element
FEATURE [App::DocumentObjectGroupPython] N_element059  label="N_element : 031"  # scripted group (container) (typed FeaturePython)
  n = 5
  ref = N_element
FEATURE [App::DocumentObjectGroupPython] O_element120  label="O_element : 073"  # scripted group (container) (typed FeaturePython)
  n = 4
  ref = O_element
FEATURE [App::DocumentObjectGroupPython] G4_DNA_ADENOSINE  # scripted group (container) (typed FeaturePython)
  Dunit = g/cm3
  Dvalue = 1
  Group = -> [H_element129,C_element139,N_element059,O_element120]
  conduct = 2
  density = 1
  expand = 3
  formula = G4_DNA_ADENOSINE
  name = G4_DNA_ADENOSINE
  specific = 4
FEATURE [App::DocumentObjectGroupPython] H_element130  label="H_element : 077"  # scripted group (container) (typed FeaturePython)
  n = 10
  ref = H_element
FEATURE [App::DocumentObjectGroupPython] C_element140  label="C_element : 085"  # scripted group (container) (typed FeaturePython)
  n = 10
  ref = C_element
FEATURE [App::DocumentObjectGroupPython] N_element060  label="N_element : 032"  # scripted group (container) (typed FeaturePython)
  n = 5
  ref = N_element
FEATURE [App::DocumentObjectGroupPython] O_element121  label="O_element : 074"  # scripted group (container) (typed FeaturePython)
  n = 5
  ref = O_element
FEATURE [App::DocumentObjectGroupPython] G4_DNA_GUANOSINE  # scripted group (container) (typed FeaturePython)
  Dunit = g/cm3
  Dvalue = 1
  Group = -> [H_element130,C_element140,N_element060,O_element121]
  conduct = 2
  density = 1
  expand = 3
  formula = G4_DNA_GUANOSINE
  name = G4_DNA_GUANOSINE
  specific = 4
FEATURE [App::DocumentObjectGroupPython] H_element131  label="H_element : 078"  # scripted group (container) (typed FeaturePython)
  n = 10
  ref = H_element
FEATURE [App::DocumentObjectGroupPython] C_element141  label="C_element : 086"  # scripted group (container) (typed FeaturePython)
  n = 9
  ref = C_element
FEATURE [App::DocumentObjectGroupPython] N_element061  label="N_element : 033"  # scripted group (container) (typed FeaturePython)
  n = 3
  ref = N_element
FEATURE [App::DocumentObjectGroupPython] O_element122  label="O_element : 075"  # scripted group (container) (typed FeaturePython)
  n = 5
  ref = O_element
FEATURE [App::DocumentObjectGroupPython] G4_DNA_CYTIDINE  # scripted group (container) (typed FeaturePython)
  Dunit = g/cm3
  Dvalue = 1
  Group = -> [H_element131,C_element141,N_element061,O_element122]
  conduct = 2
  density = 1
  expand = 3
  formula = G4_DNA_CYTIDINE
  name = G4_DNA_CYTIDINE
  specific = 4
FEATURE [App::DocumentObjectGroupPython] H_element132  label="H_element : 079"  # scripted group (container) (typed FeaturePython)
  n = 9
  ref = H_element
FEATURE [App::DocumentObjectGroupPython] C_element142  label="C_element : 087"  # scripted group (container) (typed FeaturePython)
  n = 9
  ref = C_element
FEATURE [App::DocumentObjectGroupPython] N_element062  label="N_element : 034"  # scripted group (container) (typed FeaturePython)
  n = 2
  ref = N_element
FEATURE [App::DocumentObjectGroupPython] O_element123  label="O_element : 076"  # scripted group (container) (typed FeaturePython)
  n = 6
  ref = O_element
FEATURE [App::DocumentObjectGroupPython] G4_DNA_URIDINE  # scripted group (container) (typed FeaturePython)
  Dunit = g/cm3
  Dvalue = 1
  Group = -> [H_element132,C_element142,N_element062,O_element123]
  conduct = 2
  density = 1
  expand = 3
  formula = G4_DNA_URIDINE
  name = G4_DNA_URIDINE
  specific = 4
FEATURE [App::DocumentObjectGroupPython] H_element133  label="H_element : 080"  # scripted group (container) (typed FeaturePython)
  n = 11
  ref = H_element
FEATURE [App::DocumentObjectGroupPython] C_element143  label="C_element : 088"  # scripted group (container) (typed FeaturePython)
  n = 10
  ref = C_element
FEATURE [App::DocumentObjectGroupPython] N_element063  label="N_element : 035"  # scripted group (container) (typed FeaturePython)
  n = 2
  ref = N_element
FEATURE [App::DocumentObjectGroupPython] O_element124  label="O_element : 077"  # scripted group (container) (typed FeaturePython)
  n = 6
  ref = O_element
FEATURE [App::DocumentObjectGroupPython] G4_DNA_METHYLURIDINE  # scripted group (container) (typed FeaturePython)
  Dunit = g/cm3
  Dvalue = 1
  Group = -> [H_element133,C_element143,N_element063,O_element124]
  conduct = 2
  density = 1
  expand = 3
  formula = G4_DNA_METHYLURIDINE
  name = G4_DNA_METHYLURIDINE
  specific = 4
FEATURE [App::DocumentObjectGroupPython] P_element014  label="P_element : 003"  # scripted group (container) (typed FeaturePython)
  n = 1
  ref = P_element
FEATURE [App::DocumentObjectGroupPython] O_element125  label="O_element : 078"  # scripted group (container) (typed FeaturePython)
  n = 3
  ref = O_element
FEATURE [App::DocumentObjectGroupPython] G4_DNA_MONOPHOSPHATE  # scripted group (container) (typed FeaturePython)
  Dunit = g/cm3
  Dvalue = 1
  Group = -> [P_element014,O_element125]
  conduct = 2
  density = 1
  expand = 3
  formula = G4_DNA_MONOPHOSPHATE
  name = G4_DNA_MONOPHOSPHATE
  specific = 4
FEATURE [App::DocumentObjectGroupPython] H_element134  label="H_element : 081"  # scripted group (container) (typed FeaturePython)
  n = 10
  ref = H_element
FEATURE [App::DocumentObjectGroupPython] C_element144  label="C_element : 089"  # scripted group (container) (typed FeaturePython)
  n = 10
  ref = C_element
FEATURE [App::DocumentObjectGroupPython] N_element064  label="N_element : 036"  # scripted group (container) (typed FeaturePython)
  n = 5
  ref = N_element
FEATURE [App::DocumentObjectGroupPython] O_element126  label="O_element : 079"  # scripted group (container) (typed FeaturePython)
  n = 7
  ref = O_element
FEATURE [App::DocumentObjectGroupPython] P_element015  label="P_element : 004"  # scripted group (container) (typed FeaturePython)
  n = 1
  ref = P_element
FEATURE [App::DocumentObjectGroupPython] G4_DNA_A  # scripted group (container) (typed FeaturePython)
  Dunit = g/cm3
  Dvalue = 1
  Group = -> [H_element134,C_element144,N_element064,O_element126,P_element015]
  conduct = 2
  density = 1
  expand = 3
  formula = G4_DNA_A
  name = G4_DNA_A
  specific = 4
FEATURE [App::DocumentObjectGroupPython] H_element135  label="H_element : 082"  # scripted group (container) (typed FeaturePython)
  n = 10
  ref = H_element
FEATURE [App::DocumentObjectGroupPython] C_element145  label="C_element : 090"  # scripted group (container) (typed FeaturePython)
  n = 10
  ref = C_element
FEATURE [App::DocumentObjectGroupPython] N_element065  label="N_element : 037"  # scripted group (container) (typed FeaturePython)
  n = 5
  ref = N_element
FEATURE [App::DocumentObjectGroupPython] O_element127  label="O_element : 8"  # scripted group (container) (typed FeaturePython)
  n = 8
  ref = O_element
FEATURE [App::DocumentObjectGroupPython] P_element016  label="P_element : 005"  # scripted group (container) (typed FeaturePython)
  n = 1
  ref = P_element
FEATURE [App::DocumentObjectGroupPython] G4_DNA_G  # scripted group (container) (typed FeaturePython)
  Dunit = g/cm3
  Dvalue = 1
  Group = -> [H_element135,C_element145,N_element065,O_element127,P_element016]
  conduct = 2
  density = 1
  expand = 3
  formula = G4_DNA_G
  name = G4_DNA_G
  specific = 4
FEATURE [App::DocumentObjectGroupPython] H_element136  label="H_element : 083"  # scripted group (container) (typed FeaturePython)
  n = 10
  ref = H_element
FEATURE [App::DocumentObjectGroupPython] C_element146  label="C_element : 091"  # scripted group (container) (typed FeaturePython)
  n = 9
  ref = C_element
FEATURE [App::DocumentObjectGroupPython] N_element066  label="N_element : 038"  # scripted group (container) (typed FeaturePython)
  n = 3
  ref = N_element
FEATURE [App::DocumentObjectGroupPython] O_element128  label="O_element : 080"  # scripted group (container) (typed FeaturePython)
  n = 8
  ref = O_element
FEATURE [App::DocumentObjectGroupPython] P_element017  label="P_element : 006"  # scripted group (container) (typed FeaturePython)
  n = 1
  ref = P_element
FEATURE [App::DocumentObjectGroupPython] G4_DNA_C  # scripted group (container) (typed FeaturePython)
  Dunit = g/cm3
  Dvalue = 1
  Group = -> [H_element136,C_element146,N_element066,O_element128,P_element017]
  conduct = 2
  density = 1
  expand = 3
  formula = G4_DNA_C
  name = G4_DNA_C
  specific = 4
FEATURE [App::DocumentObjectGroupPython] H_element137  label="H_element : 084"  # scripted group (container) (typed FeaturePython)
  n = 9
  ref = H_element
FEATURE [App::DocumentObjectGroupPython] C_element147  label="C_element : 092"  # scripted group (container) (typed FeaturePython)
  n = 9
  ref = C_element
FEATURE [App::DocumentObjectGroupPython] N_element067  label="N_element : 039"  # scripted group (container) (typed FeaturePython)
  n = 2
  ref = N_element
FEATURE [App::DocumentObjectGroupPython] O_element129  label="O_element : 9"  # scripted group (container) (typed FeaturePython)
  n = 9
  ref = O_element
FEATURE [App::DocumentObjectGroupPython] P_element018  label="P_element : 007"  # scripted group (container) (typed FeaturePython)
  n = 1
  ref = P_element
FEATURE [App::DocumentObjectGroupPython] G4_DNA_U  # scripted group (container) (typed FeaturePython)
  Dunit = g/cm3
  Dvalue = 1
  Group = -> [H_element137,C_element147,N_element067,O_element129,P_element018]
  conduct = 2
  density = 1
  expand = 3
  formula = G4_DNA_U
  name = G4_DNA_U
  specific = 4
FEATURE [App::DocumentObjectGroupPython] H_element138  label="H_element : 085"  # scripted group (container) (typed FeaturePython)
  n = 11
  ref = H_element
FEATURE [App::DocumentObjectGroupPython] C_element148  label="C_element : 093"  # scripted group (container) (typed FeaturePython)
  n = 10
  ref = C_element
FEATURE [App::DocumentObjectGroupPython] N_element068  label="N_element : 040"  # scripted group (container) (typed FeaturePython)
  n = 2
  ref = N_element
FEATURE [App::DocumentObjectGroupPython] O_element130  label="O_element : 081"  # scripted group (container) (typed FeaturePython)
  n = 9
  ref = O_element
FEATURE [App::DocumentObjectGroupPython] P_element019  label="P_element : 008"  # scripted group (container) (typed FeaturePython)
  n = 1
  ref = P_element
FEATURE [App::DocumentObjectGroupPython] G4_DNA_MU  # scripted group (container) (typed FeaturePython)
  Dunit = g/cm3
  Dvalue = 1
  Group = -> [H_element138,C_element148,N_element068,O_element130,P_element019]
  conduct = 2
  density = 1
  expand = 3
  formula = G4_DNA_MU
  name = G4_DNA_MU
  specific = 4
FEATURE [App::DocumentObjectGroupPython] BioChemical  # scripted group (container) (typed FeaturePython)
  Group = -> [G4_CYTOSINE,G4_THYMINE,G4_URACIL,G4_DNA_ADENINE,G4_DNA_GUANINE,G4_DNA_CYTOSINE,G4_DNA_THYMINE,G4_DNA_URACIL,G4_DNA_ADENOSINE,G4_DNA_GUANOSINE,G4_DNA_CYTIDINE,G4_DNA_URIDINE,G4_DNA_METHYLURIDINE,G4_DNA_MONOPHOSPHATE,G4_DNA_A,G4_DNA_G,G4_DNA_C,G4_DNA_U,G4_DNA_MU]
FEATURE [App::DocumentObjectGroupPython] G4Materials  # scripted group (container) (typed FeaturePython)
  Group = -> [NIST,Element,HEP,Space,BioChemical]
  version = 1
FEATURE [App::DocumentObjectGroupPython] Geant4  # scripted group (container) (typed FeaturePython)
  Group = -> [G4Isotopes,G4Elements,G4Materials]
FEATURE [App::DocumentObjectGroupPython] Materials  # scripted group (container) (typed FeaturePython)
  Group = -> [Geant4]
FEATURE [Part::FeaturePython] GDMLBox_WorldBox  # WARN: FeaturePython — macro-defined, semantics opaque (R4)
  lunit = 2
  material = 5
  x = 200
  y = 200
  z = 200
FEATURE [Sketcher::SketchObject] Sketch
  FullyConstrained = false
  Placement = pos=(0,0,0) rot=(1,0,0;1.5708rad)
  sketch-geometry (29):
    g0: LineSegment StartX=40 StartY=9.87547 StartZ=0 EndX=60 EndY=9.87547 EndZ=0
    g1: LineSegment StartX=60 StartY=9.87547 StartZ=0 EndX=60 EndY=-10.1245 EndZ=0
    g2: LineSegment StartX=60 StartY=-10.1245 StartZ=0 EndX=40 EndY=-10.1245 EndZ=0
    g3: LineSegment StartX=40 StartY=-10.1245 StartZ=0 EndX=40 EndY=9.87547 EndZ=0
    g4-g16: Circle x13 (B-spline internal-alignment scaffolding for g17; pole/knot coordinates omitted)
    g17: BSplineCurve PolesCount=13 KnotsCount=11 Degree=3 IsPeriodic=0
    g18-g28: GeomPoint x11 (B-spline internal-alignment scaffolding for g17; pole/knot coordinates omitted)
  constraints (13):
    c: Coincident(g0,g1)
    c: Coincident(g1,g2)
    c: Coincident(g2,g3)
    c: Coincident(g3,g0)
    c: Horizontal(g0)
    c: Horizontal(g2)
    c: Vertical(g1)
    c: Vertical(g3)
    c: Weight(g4) = 1
    c: Equal(g4, g5-g16) x12
    c: InternalAlignment(g4-g16 -> g17) x13
    c: InternalAlignment(g18-g28 -> g17) x11
    c: Coincident(g17,g17)
FEATURE [Part::Revolution] Revolve
  Angle = 180
  Axis = (0,0,1)
  Base = (0,0,0)
  FaceMakerClass = Part::FaceMakerBullseye
  Solid = true
  Source = -> Sketch
  Symmetric = false
  material = 6
FEATURE [App::Part] Part
  Group = -> [Sketch,Revolve]
  Origin = -> Origin001
FEATURE [App::Part] worldVOL
  Group = -> [GDMLBox_WorldBox,Part]
  Origin = -> Origin
